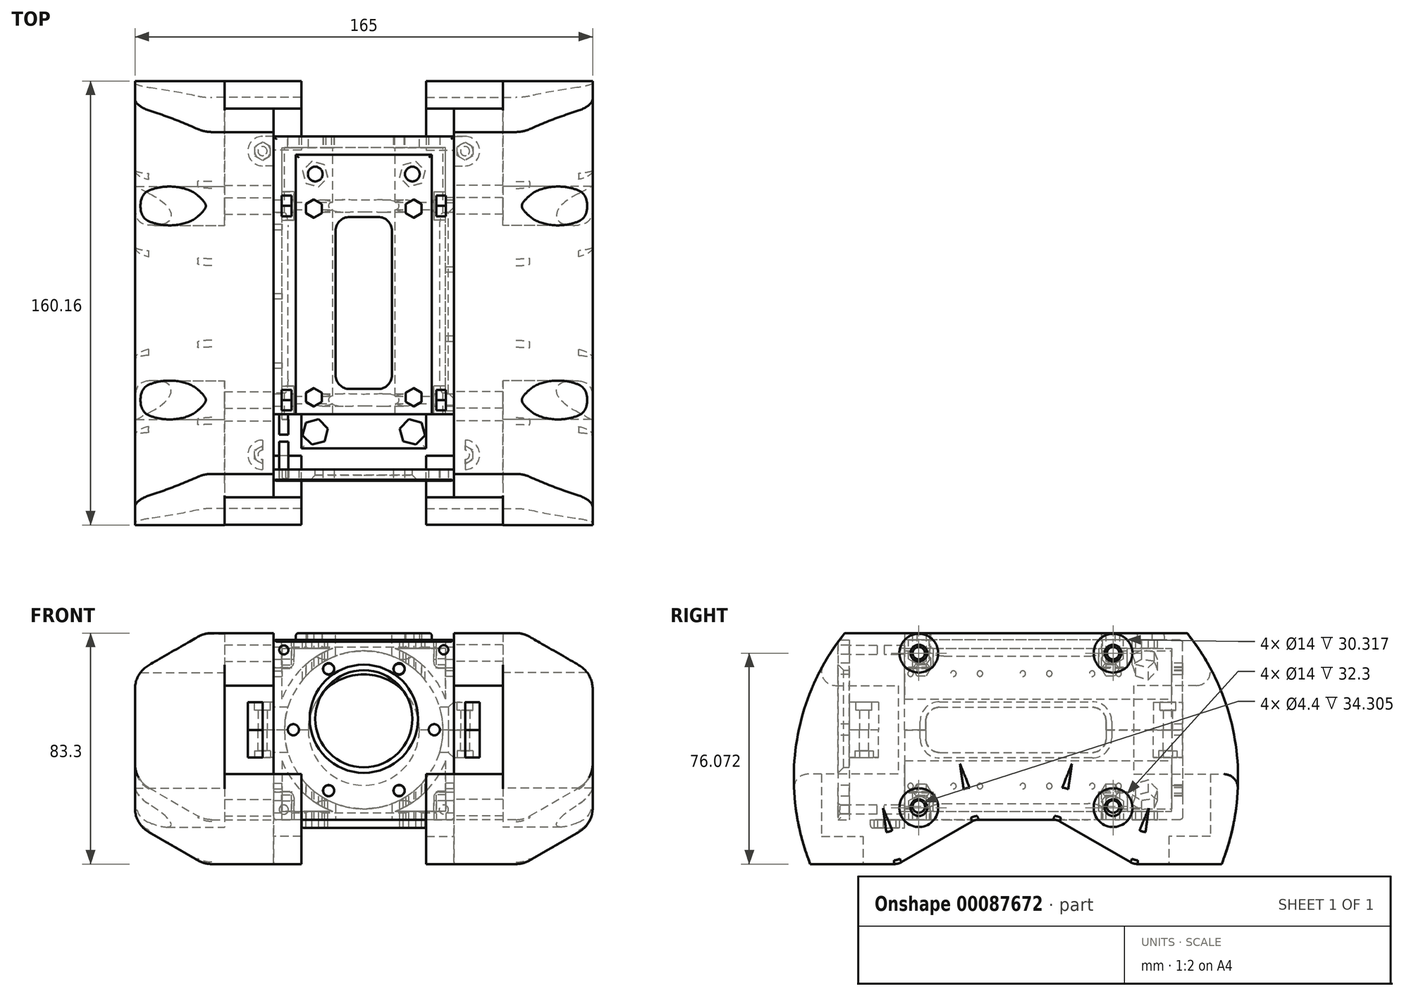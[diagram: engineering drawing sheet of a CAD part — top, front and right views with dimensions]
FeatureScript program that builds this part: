
annotation { "Feature Type Name" : "Feature", "Feature Type Description" : "" }
export const myFeature = defineFeature(function(context is Context, id is Id, definition is map)
    precondition{}
    {
        {
            assignVariable(context, id + "F0", {"name" : "M3_HEX_WIDTH", "anyValue" : 5.5});
        }
        {
            assignVariable(context, id + "F1", {"name" : "M3_HEX_HEIGHT", "anyValue" : 2.4});
        }
        {
            assignVariable(context, id + "F2", {"name" : "MIN_WALL_THICKNESS", "anyValue" : 3});
        }
        {
            assignVariable(context, id + "F3", {"name" : "BACK_LIP_THICKNESS", "anyValue" : 4});
        }
        {
            assignVariable(context, id + "F4", {"name" : "FRONT_PLATE_THICKNESS", "anyValue" : 4});
        }
        {
            assignVariable(context, id + "F5", {"name" : "CASE_WIDTH", "anyValue" : 65});
        }
        {
            assignVariable(context, id + "F6", {"name" : "BASE_TOP_INTERFERENCE", "anyValue" : 0.2});
        }
        {
            assignVariable(context, id + "F7", {"name" : "SIDE_BOSS_HEIGHT", "anyValue" : 20});
        }
        {
            assignVariable(context, id + "F8", {"name" : "M3_SOCKET_HEAD_HEIGHT", "anyValue" : 3});
        }
        {
            var Q0;
            Q0=qCreatedBy(makeId("Top.planeOp"),FACE);
            var sketch = newSketch(context, id + "F9", { "sketchPlane" : qUnion([Q0])});
            skLineSegment(sketch, "E0.bottom", {"start": v(32.5, 60.08) * mm, "end": v(-32.5, 60.08) * mm});
            skLineSegment(sketch, "E0.top", {"start": v(32.5, -60.08) * mm, "end": v(-32.5, -60.08) * mm});
            skLineSegment(sketch, "E0.left", {"start": v(32.5, 60.08) * mm, "end": v(32.5, -60.08) * mm});
            skLineSegment(sketch, "E0.right", {"start": v(-32.5, 60.08) * mm, "end": v(-32.5, -60.08) * mm});
            skPoint(sketch, "E0.middle", {"position": v(0, 0) * mm});
            skSolve(sketch);
        }
        {
            var Q0;
            Q0=makeQuery(id+"F9.imprint","IMPRINT",FACE,{"disambiguationData":[TD([[makeQuery(id+"F9.imprint","IMPRINT",EDGE,{"derivedFrom":sQuery(id+"F9.wireOp",EDGE,"E0.bottom")}),1.0]])]});
            extrude(context, id + "F10", {"entities" : qUnion([Q0]), "depth" : ((getVariable(context, 'CASE_WIDTH') - getVariable(context, 'BASE_TOP_INTERFERENCE')) / 2) * mm});
        }
        {
            var Q0;
            Q0=makeQuery(id+"F10.opExtrude","SWEPT_FACE",FACE,{"disambiguationData":[OSD([sQuery(id+"F9.wireOp",EDGE,"E0.bottom")])]});
            cPlane(context, id + "F11", {"entities" : qUnion([Q0]), "cplaneType" : CPlaneType.OFFSET, "offset" : (getVariable(context, 'BACK_LIP_THICKNESS')) * mm, "oppositeDirection" : true, "width" : 150 * mm, "height" : 150 * mm});
        }
        {
            var Q0;
            Q0=qCreatedBy(id+"F11.planeOp",FACE);
            var sketch = newSketch(context, id + "F12", { "sketchPlane" : qUnion([Q0])});
            skLineSegment(sketch, "E1", {"start": v(0, 32.4) * mm, "end": v(0, 32.5) * mm, "construction": true});
            skCircle(sketch, "E2", {"center": v(0, 32.5) * mm, "radius": 28.57 * mm});
            skLineSegment(sketch, "E3.1", {"start": v(-32.5, 32.4) * mm, "end": v(32.5, 32.4) * mm, "construction": true});
            skSolve(sketch);
        }
        {
            var Q0;
            Q0=makeQuery(id+"F12.imprint","IMPRINT",FACE,{"disambiguationData":[TD([[makeQuery(id+"F12.imprint","IMPRINT",EDGE,{"derivedFrom":sQuery(id+"F12.wireOp",EDGE,"E2")}),1.0]])]});
            extrude(context, id + "F13", {"entities" : qUnion([Q0]), "operationType" : NewBodyOperationType.REMOVE, "endBound" : BoundingType.THROUGH_ALL, "oppositeDirection" : true, "depth" : 25 * mm});
        }
        {
            var Q0;
            Q0=makeQuery(id+"F10.opExtrude","SWEPT_FACE",FACE,{"disambiguationData":[OSD([sQuery(id+"F9.wireOp",EDGE,"E0.bottom")])]});
            var sketch = newSketch(context, id + "F14", { "sketchPlane" : qUnion([Q0])});
            skCircle(sketch, "E4", {"center": v(0, 32.4) * mm, "radius": 20 * mm});
            skSolve(sketch);
        }
        {
            var Q0;
            {var subQ0=sQuery(id+"F14.wireOp",EDGE,"E4");var subQ1=makeQuery(id+"F10.opExtrude","CAP_EDGE",EDGE,{"disambiguationData":[OSD([sQuery(id+"F9.wireOp",EDGE,"E0.bottom")])],"isStart":false});var subQ2=makeQuery(id+"F14.imprint","INTERSECT",VERTEX,{"disambiguationData":[OD(0.0)],"derivedFrom":[subQ1,subQ0]});Q0=makeQuery(id+"F14.imprint","IMPRINT",FACE,{"disambiguationData":[TD([[makeQuery(id+"F14.imprint","IMPRINT",EDGE,{"disambiguationData":[TD([[subQ2,-1.0]])],"derivedFrom":subQ0}),1.0]])]});}
            extrude(context, id + "F15", {"entities" : qUnion([Q0]), "operationType" : NewBodyOperationType.REMOVE, "endBound" : BoundingType.THROUGH_ALL, "oppositeDirection" : true, "depth" : 25 * mm});
        }
        {
            var Q0;
            Q0=makeQuery(id+"F13.boolean.opBoolean","COPY",FACE,{"derivedFrom":makeQuery(id+"F13.opExtrude","CAP_FACE",FACE,{"disambiguationData":[OSD([sQuery(id+"F12.wireOp",EDGE,"E2")])],"isStart":true})});
            var sketch = newSketch(context, id + "F16", { "sketchPlane" : qUnion([Q0])});
            skLineSegment(sketch, "E5", {"start": v(20, 32.4) * mm, "end": v(-20, 32.4) * mm, "construction": true});
            skLineSegment(sketch, "E6", {"start": v(0, 32.4) * mm, "end": v(0, 32.5) * mm});
            skPoint(sketch, "E6.endSnap0", {"position": v(0, 32.4) * mm});
            skCircle(sketch, "E7", {"center": v(0, 32.5) * mm, "radius": 25.4 * mm, "construction": true});
            skCircle(sketch, "E8", {"center": v(-12.66, 10.48) * mm, "radius": 2 * mm});
            skCircle(sketch, "E9.1.0", {"center": v(12.74, 10.53) * mm, "radius": 2 * mm});
            skCircle(sketch, "E9.2.0", {"center": v(25.4, 32.55) * mm, "radius": 2 * mm});
            skCircle(sketch, "E10.1.3.0", {"center": v(12.66, 54.52) * mm, "radius": 2 * mm});
            skCircle(sketch, "E10.1.4.0", {"center": v(-12.74, 54.47) * mm, "radius": 2 * mm});
            skCircle(sketch, "E10.1.5.0", {"center": v(-25.4, 32.45) * mm, "radius": 2 * mm});
            skLineSegment(sketch, "E11", {"start": v(0, 32.4) * mm, "end": v(0, 21) * mm, "construction": true});
            skLineSegment(sketch, "E12", {"start": v(0, 32.4) * mm, "end": v(-12.66, 10.48) * mm, "construction": true});
            skSolve(sketch);
        }
        {
            var Q0;
            Q0 = qSketchRegion(id + "F16", true);
            extrude(context, id + "F17", {"entities" : qUnion([Q0]), "operationType" : NewBodyOperationType.REMOVE, "endBound" : BoundingType.THROUGH_ALL, "oppositeDirection" : true, "depth" : 25 * mm});
        }
        {
            var Q0;
            {var subQ0=sQuery(id+"F9.wireOp",EDGE,"E0.left");var subQ2=sQuery(id+"F9.wireOp",EDGE,"E0.top");var subQ3=sQuery(id+"F9.wireOp",EDGE,"E0.bottom");Q0=makeQuery(id+"F15.boolean.opBoolean","SPLIT",FACE,{"disambiguationData":[TD([makeQuery(id+"F10.opExtrude","SWEPT_FACE",FACE,{"disambiguationData":[OSD([subQ0])]})])],"derivedFrom":makeQuery(id+"F10.opExtrude","CAP_FACE",FACE,{"disambiguationData":[OSD([subQ3,subQ2,subQ0,sQuery(id+"F9.wireOp",EDGE,"E0.right")])],"isStart":false})});}
            var sketch = newSketch(context, id + "F18", { "sketchPlane" : qUnion([Q0])});
            skLineSegment(sketch, "E13.0", {"start": v(-32.5, 60.08) * mm, "end": v(-32.5, -60.08) * mm, "construction": true});
            skLineSegment(sketch, "E14", {"start": v(32.5, -54.77) * mm, "end": v(-32.5, -54.77) * mm, "construction": true});
            skLineSegment(sketch, "E15", {"start": v(32.5, -49.48) * mm, "end": v(32.5, -54.77) * mm});
            skLineSegment(sketch, "E16", {"start": v(32.5, -49.48) * mm, "end": v(36.5, -49.48) * mm});
            skLineSegment(sketch, "E17.MirrorCS", {"start": v(32.5, -60.07) * mm, "end": v(36.5, -60.07) * mm});
            skLineSegment(sketch, "E18.MirrorCS", {"start": v(32.5, -60.08) * mm, "end": v(32.5, -54.77) * mm});
            skArc(sketch, "E19", {"start": v(36.5, -49.48) * mm, "mid": v(41.8, -54.78) * mm, "end": v(36.5, -60.08) * mm});
            skLineSegment(sketch, "E20", {"start": v(0, -60.07) * mm, "end": v(0, 0) * mm, "construction": true});
            skPoint(sketch, "E20.endSnap0", {"position": v(0, 0) * mm});
            skLineSegment(sketch, "E21.MirrorCS", {"start": v(-32.5, -49.48) * mm, "end": v(-36.5, -49.48) * mm});
            skArc(sketch, "E22.MirrorCS", {"start": v(-36.5, -49.48) * mm, "mid": v(-41.8, -54.78) * mm, "end": v(-36.5, -60.08) * mm});
            skLineSegment(sketch, "E23.MirrorCS", {"start": v(-32.5, -49.48) * mm, "end": v(-32.5, -54.77) * mm});
            skLineSegment(sketch, "E24.MirrorCS", {"start": v(-32.5, -60.08) * mm, "end": v(-32.5, -54.77) * mm});
            skLineSegment(sketch, "E25.MirrorCS", {"start": v(-32.5, -60.08) * mm, "end": v(-36.5, -60.08) * mm});
            skLineSegment(sketch, "E26", {"start": v(32.5, -60.07) * mm, "end": v(-32.5, -60.07) * mm, "construction": true});
            skLineSegment(sketch, "E27", {"start": v(0, 0) * mm, "end": v(32.5, 0) * mm, "construction": true});
            skLineSegment(sketch, "E28.MirrorCS", {"start": v(32.5, 49.48) * mm, "end": v(36.5, 49.48) * mm});
            skLineSegment(sketch, "E29.MirrorCS", {"start": v(32.5, 60.07) * mm, "end": v(36.5, 60.07) * mm});
            skArc(sketch, "E30.MirrorCS", {"start": v(36.5, 49.48) * mm, "mid": v(41.8, 54.77) * mm, "end": v(36.5, 60.07) * mm});
            skLineSegment(sketch, "E31.MirrorCS", {"start": v(32.5, 49.47) * mm, "end": v(32.5, 54.77) * mm});
            skLineSegment(sketch, "E32.MirrorCS", {"start": v(32.5, 60.08) * mm, "end": v(32.5, 54.77) * mm});
            skLineSegment(sketch, "E33.MirrorCS", {"start": v(32.5, 60.08) * mm, "end": v(-32.5, 60.07) * mm, "construction": true});
            skLineSegment(sketch, "E34.MirrorCS", {"start": v(32.5, 54.77) * mm, "end": v(-32.5, 54.77) * mm, "construction": true});
            skArc(sketch, "E35.MirrorCS", {"start": v(-36.5, 49.48) * mm, "mid": v(-41.8, 54.77) * mm, "end": v(-36.5, 60.07) * mm});
            skLineSegment(sketch, "E36.MirrorCS", {"start": v(-32.5, 60.07) * mm, "end": v(-36.5, 60.07) * mm});
            skLineSegment(sketch, "E37.MirrorCS", {"start": v(-32.5, 60.08) * mm, "end": v(-32.5, 54.77) * mm});
            skLineSegment(sketch, "E38.MirrorCS", {"start": v(-32.5, -60.08) * mm, "end": v(-32.5, 60.08) * mm, "construction": true});
            skLineSegment(sketch, "E39.MirrorCS", {"start": v(-32.5, 49.47) * mm, "end": v(-32.5, 54.77) * mm});
            skLineSegment(sketch, "E40.MirrorCS", {"start": v(-32.5, 49.48) * mm, "end": v(-36.5, 49.48) * mm});
            skSolve(sketch);
        }
        {
            var Q0;
            Q0 = qSketchRegion(id + "F18", true);
            extrude(context, id + "F19", {"entities" : qUnion([Q0]), "operationType" : NewBodyOperationType.ADD, "oppositeDirection" : true, "depth" : ((getVariable(context, 'SIDE_BOSS_HEIGHT')) / 2) * mm});
        }
        {
            var Q0;
            Q0=sQuery(id+"F18.wireOp",VERTEX,"E22.MirrorCS.center");
            var Q1;
            Q1=sQuery(id+"F18.wireOp",VERTEX,"E19.center");
            var Q2;
            Q2=sQuery(id+"F18.wireOp",VERTEX,"E35.MirrorCS.center");
            var Q3;
            Q3=sQuery(id+"F18.wireOp",VERTEX,"E30.MirrorCS.center");
            var Q4;
            Q4=makeQuery(id+"F10.opExtrude","SWEPT_BODY",BODY,{"disambiguationData":[OSD([sQuery(id+"F9.wireOp",EDGE,"E0.bottom"),sQuery(id+"F9.wireOp",EDGE,"E0.top"),sQuery(id+"F9.wireOp",EDGE,"E0.left"),sQuery(id+"F9.wireOp",EDGE,"E0.right")])]});
            hole(context, id + "F20", {"style" : HoleStyle.SIMPLE, "endStyle" : HoleEndStyle.THROUGH, "standardTappedOrClearance" : lookupTablePath({ "standard" : "ISO", "fit" : "Normal", "size" : "M3", "type" : "Clearance" }), "standardBlindInLast" : lookupTablePath({ "fit" : "Standard", "standard" : "ISO", "size" : "M3", "type" : "Clearance" }), "holeDiameter" : 3.3 * mm, "locations" : qUnion([Q0, Q1, Q2, Q3]), "scope" : qUnion([Q4]), "isTappedThrough" : true});
        }
        {
            var Q0;
            Q0=makeQuery(id+"F13.boolean.opBoolean","COPY",FACE,{"derivedFrom":makeQuery(id+"F13.opExtrude","CAP_FACE",FACE,{"disambiguationData":[OSD([sQuery(id+"F12.wireOp",EDGE,"E2")])],"isStart":true})});
            var sketch = newSketch(context, id + "F21", { "sketchPlane" : qUnion([Q0])});
            skLineSegment(sketch, "E41", {"start": v(0, 0) * mm, "end": v(0, 32.5) * mm, "construction": true});
            skLineSegment(sketch, "E42", {"start": v(29.5, 21.24) * mm, "end": v(29.5, 3) * mm});
            skLineSegment(sketch, "E43", {"start": v(29.5, 3) * mm, "end": v(11.26, 3) * mm});
            skArc(sketch, "E44", {"start": v(11.26, 3) * mm, "mid": v(22.33, 10.17) * mm, "end": v(29.5, 21.24) * mm});
            skArc(sketch, "E45.MirrorCS", {"start": v(-11.26, 3) * mm, "mid": v(-22.33, 10.17) * mm, "end": v(-29.5, 21.24) * mm});
            skLineSegment(sketch, "E46.MirrorCS", {"start": v(-29.5, 3) * mm, "end": v(-11.26, 3) * mm});
            skLineSegment(sketch, "E47.MirrorCS", {"start": v(-29.5, 21.24) * mm, "end": v(-29.5, 3) * mm});
            skSolve(sketch);
        }
        {
            var Q0;
            Q0 = qSketchRegion(id + "F21", true);
            extrude(context, id + "F22", {"entities" : qUnion([Q0]), "operationType" : NewBodyOperationType.REMOVE, "endBound" : BoundingType.THROUGH_ALL, "depth" : 25 * mm});
        }
        {
            var Q0;
            Q0=makeQuery(id+"F22.boolean.opBoolean","COPY",FACE,{"derivedFrom":makeQuery(id+"F22.opExtrude","SWEPT_FACE",FACE,{"disambiguationData":[OSD([sQuery(id+"F21.wireOp",EDGE,"E47.MirrorCS")])]})});
            var sketch = newSketch(context, id + "F23", { "sketchPlane" : qUnion([Q0])});
            skLineSegment(sketch, "E48", {"start": v(-60.08, 12.12) * mm, "end": v(56.08, 12.12) * mm, "construction": true});
            skCircle(sketch, "E49", {"center": v(-47.52, 12.12) * mm, "radius": 1 * mm});
            skCircle(sketch, "E50.1.0.0", {"center": v(-22.52, 12.12) * mm, "radius": 1 * mm});
            skCircle(sketch, "E50.2.0.0", {"center": v(2.48, 12.12) * mm, "radius": 1 * mm});
            skCircle(sketch, "E50.3.0.0", {"center": v(27.48, 12.12) * mm, "radius": 1 * mm});
            skLineSegment(sketch, "E50.direction1", {"start": v(-47.52, 12.12) * mm, "end": v(-22.52, 12.12) * mm, "construction": true});
            skSolve(sketch);
        }
        {
            var Q0;
            Q0=makeQuery(id+"F22.boolean.opBoolean","COPY",FACE,{"derivedFrom":makeQuery(id+"F22.opExtrude","SWEPT_FACE",FACE,{"disambiguationData":[OSD([sQuery(id+"F21.wireOp",EDGE,"E42")])]})});
            var sketch = newSketch(context, id + "F24", { "sketchPlane" : qUnion([Q0])});
            skLineSegment(sketch, "E51", {"start": v(60.08, 12.12) * mm, "end": v(-56.08, 12.12) * mm, "construction": true});
            skCircle(sketch, "E52", {"center": v(37.97, 12.12) * mm, "radius": 1 * mm});
            skCircle(sketch, "E53.1.0.0", {"center": v(12.97, 12.12) * mm, "radius": 1 * mm});
            skCircle(sketch, "E53.2.0.0", {"center": v(-12.03, 12.12) * mm, "radius": 1 * mm});
            skCircle(sketch, "E53.3.0.0", {"center": v(-37.03, 12.12) * mm, "radius": 1 * mm});
            skLineSegment(sketch, "E53.direction1", {"start": v(37.97, 12.12) * mm, "end": v(12.97, 12.12) * mm, "construction": true});
            skSolve(sketch);
        }
        {
            var Q0;
            Q0 = qSketchRegion(id + "F23", true);
            extrude(context, id + "F25", {"entities" : qUnion([Q0]), "operationType" : NewBodyOperationType.REMOVE, "endBound" : BoundingType.THROUGH_ALL, "oppositeDirection" : true, "depth" : 25 * mm});
        }
        {
            var Q0;
            Q0 = qSketchRegion(id + "F24", true);
            extrude(context, id + "F26", {"entities" : qUnion([Q0]), "operationType" : NewBodyOperationType.REMOVE, "endBound" : BoundingType.THROUGH_ALL, "oppositeDirection" : true, "depth" : 25 * mm});
        }
        {
            var Q0;
            Q0=makeQuery(id+"F10.opExtrude","SWEPT_FACE",FACE,{"disambiguationData":[OSD([sQuery(id+"F9.wireOp",EDGE,"E0.top")])]});
            var sketch = newSketch(context, id + "F27", { "sketchPlane" : qUnion([Q0])});
            skLineSegment(sketch, "E54.bottom", {"start": v(32.5, 0) * mm, "end": v(25.2, 0) * mm});
            skLineSegment(sketch, "E54.top", {"start": v(32.5, 7.3) * mm, "end": v(25.2, 7.3) * mm});
            skLineSegment(sketch, "E54.left", {"start": v(32.5, 0) * mm, "end": v(32.5, 7.3) * mm});
            skLineSegment(sketch, "E54.right", {"start": v(25.2, 0) * mm, "end": v(25.2, 7.3) * mm});
            skLineSegment(sketch, "E55", {"start": v(0, 0) * mm, "end": v(0, 33.35) * mm, "construction": true});
            skLineSegment(sketch, "E56.MirrorCS", {"start": v(-25.2, 0) * mm, "end": v(-25.2, 7.3) * mm});
            skLineSegment(sketch, "E57.MirrorCS", {"start": v(-32.5, 0) * mm, "end": v(-25.2, 0) * mm});
            skLineSegment(sketch, "E58.MirrorCS", {"start": v(-32.5, 0) * mm, "end": v(-32.5, 7.3) * mm});
            skLineSegment(sketch, "E59.MirrorCS", {"start": v(-32.5, 7.3) * mm, "end": v(-25.2, 7.3) * mm});
            skSolve(sketch);
        }
        {
            var Q0;
            Q0 = qSketchRegion(id + "F27", true);
            extrude(context, id + "F28", {"entities" : qUnion([Q0]), "operationType" : NewBodyOperationType.ADD, "oppositeDirection" : true, "depth" : 18 * mm});
        }
        {
            var Q0;
            Q0=makeQuery(id+"F28.boolean.opBoolean","MERGE",FACE,{"derivedFrom":[makeQuery(id+"F10.opExtrude","SWEPT_FACE",FACE,{"disambiguationData":[OSD([sQuery(id+"F9.wireOp",EDGE,"E0.top")])]}),makeQuery(id+"F28.opExtrude","CAP_FACE",FACE,{"disambiguationData":[OSD([sQuery(id+"F27.wireOp",EDGE,"E54.bottom"),sQuery(id+"F27.wireOp",EDGE,"E54.top"),sQuery(id+"F27.wireOp",EDGE,"E54.left"),sQuery(id+"F27.wireOp",EDGE,"E54.right")])],"isStart":true}),makeQuery(id+"F28.opExtrude","CAP_FACE",FACE,{"disambiguationData":[OSD([sQuery(id+"F27.wireOp",EDGE,"E57.MirrorCS"),sQuery(id+"F27.wireOp",EDGE,"E58.MirrorCS"),sQuery(id+"F27.wireOp",EDGE,"E59.MirrorCS"),sQuery(id+"F27.wireOp",EDGE,"E56.MirrorCS")])],"isStart":true})]});
            var sketch = newSketch(context, id + "F29", { "sketchPlane" : qUnion([Q0])});
            skLineSegment(sketch, "E60", {"start": v(32.5, 0) * mm, "end": v(25.2, 7.3) * mm, "construction": true});
            skCircle(sketch, "E61", {"center": v(28.85, 3.65) * mm, "radius": 1.65 * mm});
            skLineSegment(sketch, "E62", {"start": v(0, 0) * mm, "end": v(0, 32.4) * mm, "construction": true});
            skCircle(sketch, "E63.MirrorC", {"center": v(-28.85, 3.65) * mm, "radius": 1.65 * mm});
            skSolve(sketch);
        }
        {
            var Q0;
            Q0=makeQuery(id+"F29.imprint","IMPRINT",FACE,{"disambiguationData":[TD([[makeQuery(id+"F29.imprint","IMPRINT",EDGE,{"derivedFrom":sQuery(id+"F29.wireOp",EDGE,"E63.MirrorC")}),-1.0]])]});
            var Q1;
            Q1=makeQuery(id+"F29.imprint","IMPRINT",FACE,{"disambiguationData":[TD([[makeQuery(id+"F29.imprint","IMPRINT",EDGE,{"derivedFrom":sQuery(id+"F29.wireOp",EDGE,"E61")}),1.0]])]});
            extrude(context, id + "F30", {"entities" : qUnion([Q0, Q1]), "operationType" : NewBodyOperationType.REMOVE, "oppositeDirection" : true, "depth" : 20 * mm});
        }
        {
            var Q0;
            Q0=makeQuery(id+"F28.boolean.opBoolean","MERGE",FACE,{"derivedFrom":[makeQuery(id+"F10.opExtrude","SWEPT_FACE",FACE,{"disambiguationData":[OSD([sQuery(id+"F9.wireOp",EDGE,"E0.top")])]}),makeQuery(id+"F28.opExtrude","CAP_FACE",FACE,{"disambiguationData":[OSD([sQuery(id+"F27.wireOp",EDGE,"E54.bottom"),sQuery(id+"F27.wireOp",EDGE,"E54.top"),sQuery(id+"F27.wireOp",EDGE,"E54.left"),sQuery(id+"F27.wireOp",EDGE,"E54.right")])],"isStart":true}),makeQuery(id+"F28.opExtrude","CAP_FACE",FACE,{"disambiguationData":[OSD([sQuery(id+"F27.wireOp",EDGE,"E57.MirrorCS"),sQuery(id+"F27.wireOp",EDGE,"E58.MirrorCS"),sQuery(id+"F27.wireOp",EDGE,"E59.MirrorCS"),sQuery(id+"F27.wireOp",EDGE,"E56.MirrorCS")])],"isStart":true})]});
            cPlane(context, id + "F31", {"entities" : qUnion([Q0]), "cplaneType" : CPlaneType.OFFSET, "offset" : 10 * mm, "oppositeDirection" : true, "width" : 150 * mm, "height" : 150 * mm});
        }
        {
            var Q0;
            Q0=qCreatedBy(id+"F31.planeOp",FACE);
            var sketch = newSketch(context, id + "F32", { "sketchPlane" : qUnion([Q0])});
            skCircle(sketch, "E64.0", {"center": v(28.85, 3.65) * mm, "radius": 1.65 * mm, "construction": true});
            skCircle(sketch, "E65.cCircle", {"center": v(28.85, 3.65) * mm, "radius": 2.85 * mm, "construction": true});
            skLineSegment(sketch, "E65.0", {"start": v(28.85, 6.94) * mm, "end": v(31.7, 5.3) * mm});
            skLineSegment(sketch, "E65.1", {"start": v(31.7, 5.3) * mm, "end": v(31.7, 2) * mm});
            skLineSegment(sketch, "E65.2", {"start": v(31.7, 2) * mm, "end": v(28.85, 0.36) * mm});
            skLineSegment(sketch, "E65.3", {"start": v(28.85, 0.36) * mm, "end": v(26, 2) * mm});
            skLineSegment(sketch, "E65.4", {"start": v(26, 2) * mm, "end": v(26, 5.3) * mm});
            skLineSegment(sketch, "E65.5", {"start": v(26, 5.3) * mm, "end": v(28.85, 6.94) * mm});
            skPoint(sketch, "E65.0.midPoint", {"position": v(30.28, 6.12) * mm});
            skLineSegment(sketch, "E66", {"start": v(0, 0) * mm, "end": v(0, 24.89) * mm, "construction": true});
            skLineSegment(sketch, "E67.MirrorCS", {"start": v(-26, 5.3) * mm, "end": v(-28.85, 6.94) * mm});
            skLineSegment(sketch, "E68.MirrorCS", {"start": v(-26, 2) * mm, "end": v(-26, 5.3) * mm});
            skLineSegment(sketch, "E69.MirrorCS", {"start": v(-28.85, 0.36) * mm, "end": v(-26, 2) * mm});
            skLineSegment(sketch, "E70.MirrorCS", {"start": v(-31.7, 2) * mm, "end": v(-28.85, 0.36) * mm});
            skLineSegment(sketch, "E71.MirrorCS", {"start": v(-31.7, 5.3) * mm, "end": v(-31.7, 2) * mm});
            skLineSegment(sketch, "E72.MirrorCS", {"start": v(-28.85, 6.94) * mm, "end": v(-31.7, 5.3) * mm});
            skCircle(sketch, "E73.MirrorC", {"center": v(-28.85, 3.65) * mm, "radius": 2.85 * mm, "construction": true});
            skCircle(sketch, "E74.MirrorC", {"center": v(-28.85, 3.65) * mm, "radius": 1.65 * mm, "construction": true});
            skPoint(sketch, "E75.MirrorP", {"position": v(-30.28, 6.12) * mm});
            skSolve(sketch);
        }
        {
            var Q0;
            Q0 = qSketchRegion(id + "F32", true);
            extrude(context, id + "F33", {"entities" : qUnion([Q0]), "operationType" : NewBodyOperationType.REMOVE, "oppositeDirection" : true, "depth" : (getVariable(context, 'M3_HEX_HEIGHT') + 0.2) * mm});
        }
        {
            var Q0;
            Q0=makeQuery(id+"F10.opExtrude","CAP_FACE",FACE,{"disambiguationData":[OSD([sQuery(id+"F9.wireOp",EDGE,"E0.bottom"),sQuery(id+"F9.wireOp",EDGE,"E0.top"),sQuery(id+"F9.wireOp",EDGE,"E0.left"),sQuery(id+"F9.wireOp",EDGE,"E0.right")])],"isStart":true});
            var sketch = newSketch(context, id + "F34", { "sketchPlane" : qUnion([Q0])});
            skLineSegment(sketch, "E76.0", {"start": v(31.7, 47.48) * mm, "end": v(31.7, 50.08) * mm});
            skLineSegment(sketch, "E76.1", {"start": v(26, 47.48) * mm, "end": v(26, 50.08) * mm});
            skLineSegment(sketch, "E77", {"start": v(31.7, 50.08) * mm, "end": v(26, 50.08) * mm});
            skLineSegment(sketch, "E78", {"start": v(31.7, 47.48) * mm, "end": v(26, 47.48) * mm});
            skLineSegment(sketch, "E79", {"start": v(0, 0) * mm, "end": v(0, 60.08) * mm, "construction": true});
            skLineSegment(sketch, "E80.MirrorCS", {"start": v(-31.7, 47.47) * mm, "end": v(-31.7, 50.07) * mm});
            skLineSegment(sketch, "E81.MirrorCS", {"start": v(-31.7, 47.47) * mm, "end": v(-26, 47.47) * mm});
            skLineSegment(sketch, "E82.MirrorCS", {"start": v(-31.7, 50.07) * mm, "end": v(-26, 50.07) * mm});
            skLineSegment(sketch, "E83.MirrorCS", {"start": v(-26, 47.47) * mm, "end": v(-26, 50.07) * mm});
            skSolve(sketch);
        }
        {
            var Q0;
            Q0 = qSketchRegion(id + "F34", true);
            extrude(context, id + "F35", {"entities" : qUnion([Q0]), "operationType" : NewBodyOperationType.REMOVE, "oppositeDirection" : true, "depth" : (getVariable(context, 'M3_HEX_WIDTH')) * mm});
        }
        {
            var Q0;
            Q0=makeQuery(id+"F10.opExtrude","CAP_FACE",FACE,{"disambiguationData":[OSD([sQuery(id+"F9.wireOp",EDGE,"E0.bottom"),sQuery(id+"F9.wireOp",EDGE,"E0.top"),sQuery(id+"F9.wireOp",EDGE,"E0.left"),sQuery(id+"F9.wireOp",EDGE,"E0.right")])],"isStart":true});
            var sketch = newSketch(context, id + "F36", { "sketchPlane" : qUnion([Q0])});
            skLineSegment(sketch, "E84.bottom", {"start": v(27.85, 35) * mm, "end": v(-27.85, 35) * mm, "construction": true});
            skLineSegment(sketch, "E84.top", {"start": v(27.85, -35) * mm, "end": v(-27.85, -35) * mm, "construction": true});
            skLineSegment(sketch, "E84.left", {"start": v(27.85, 35) * mm, "end": v(27.85, -35) * mm, "construction": true});
            skLineSegment(sketch, "E84.right", {"start": v(-27.85, 35) * mm, "end": v(-27.85, -35) * mm, "construction": true});
            skPoint(sketch, "E84.middle", {"position": v(0, 0) * mm});
            skLineSegment(sketch, "E85.bottom", {"start": v(32.5, 40.1) * mm, "end": v(23.2, 40.1) * mm, "construction": true});
            skLineSegment(sketch, "E85.top", {"start": v(32.5, 29.9) * mm, "end": v(23.2, 29.9) * mm, "construction": true});
            skLineSegment(sketch, "E85.left", {"start": v(32.5, 40.1) * mm, "end": v(32.5, 29.9) * mm});
            skLineSegment(sketch, "E85.right", {"start": v(23.2, 40.1) * mm, "end": v(23.2, 29.9) * mm, "construction": true});
            skPoint(sketch, "E85.middle", {"position": v(27.85, 35) * mm});
            skLineSegment(sketch, "E86", {"start": v(25.2, 40.1) * mm, "end": v(25.2, 29.9) * mm});
            skLineSegment(sketch, "E87", {"start": v(25.2, 40.1) * mm, "end": v(32.5, 40.1) * mm});
            skLineSegment(sketch, "E88", {"start": v(32.5, 29.9) * mm, "end": v(25.2, 29.9) * mm});
            skLineSegment(sketch, "E89", {"start": v(0, 0) * mm, "end": v(0, 35) * mm, "construction": true});
            skLineSegment(sketch, "E90", {"start": v(0, 0) * mm, "end": v(27.85, 0) * mm, "construction": true});
            skLineSegment(sketch, "E91.MirrorCS", {"start": v(-32.5, 40.1) * mm, "end": v(-23.2, 40.1) * mm, "construction": true});
            skLineSegment(sketch, "E92.MirrorCS", {"start": v(-32.5, 29.9) * mm, "end": v(-23.2, 29.9) * mm, "construction": true});
            skLineSegment(sketch, "E93.MirrorCS", {"start": v(-23.2, 40.1) * mm, "end": v(-23.2, 29.9) * mm, "construction": true});
            skLineSegment(sketch, "E94.MirrorCS", {"start": v(-25.2, 40.1) * mm, "end": v(-32.5, 40.1) * mm});
            skLineSegment(sketch, "E95.MirrorCS", {"start": v(-32.5, 29.9) * mm, "end": v(-25.2, 29.9) * mm});
            skPoint(sketch, "E96.MirrorP", {"position": v(-27.85, 35) * mm});
            skLineSegment(sketch, "E97.MirrorCS", {"start": v(-32.5, 40.1) * mm, "end": v(-32.5, 29.9) * mm});
            skLineSegment(sketch, "E98.MirrorCS", {"start": v(-25.2, 40.1) * mm, "end": v(-25.2, 29.9) * mm});
            skLineSegment(sketch, "E99.MirrorCS", {"start": v(-32.5, -29.9) * mm, "end": v(-23.2, -29.9) * mm, "construction": true});
            skLineSegment(sketch, "E100.MirrorCS", {"start": v(-32.5, -40.1) * mm, "end": v(-23.2, -40.1) * mm, "construction": true});
            skLineSegment(sketch, "E101.MirrorCS", {"start": v(-23.2, -40.1) * mm, "end": v(-23.2, -29.9) * mm, "construction": true});
            skLineSegment(sketch, "E102.MirrorCS", {"start": v(-32.5, -40.1) * mm, "end": v(-32.5, -29.9) * mm});
            skLineSegment(sketch, "E103.MirrorCS", {"start": v(-25.2, -40.1) * mm, "end": v(-32.5, -40.1) * mm});
            skLineSegment(sketch, "E104.MirrorCS", {"start": v(-32.5, -29.9) * mm, "end": v(-25.2, -29.9) * mm});
            skPoint(sketch, "E105.MirrorP", {"position": v(-27.85, -35) * mm});
            skLineSegment(sketch, "E106.MirrorCS", {"start": v(-25.2, -40.1) * mm, "end": v(-25.2, -29.9) * mm});
            skLineSegment(sketch, "E107.MirrorCS", {"start": v(32.5, -40.1) * mm, "end": v(23.2, -40.1) * mm, "construction": true});
            skLineSegment(sketch, "E108.MirrorCS", {"start": v(32.5, -29.9) * mm, "end": v(23.2, -29.9) * mm, "construction": true});
            skLineSegment(sketch, "E109.MirrorCS", {"start": v(32.5, -29.9) * mm, "end": v(25.2, -29.9) * mm});
            skLineSegment(sketch, "E110.MirrorCS", {"start": v(25.2, -40.1) * mm, "end": v(32.5, -40.1) * mm});
            skLineSegment(sketch, "E111.MirrorCS", {"start": v(32.5, -40.1) * mm, "end": v(32.5, -29.9) * mm});
            skLineSegment(sketch, "E112.MirrorCS", {"start": v(23.2, -40.1) * mm, "end": v(23.2, -29.9) * mm, "construction": true});
            skLineSegment(sketch, "E113.MirrorCS", {"start": v(25.2, -40.1) * mm, "end": v(25.2, -29.9) * mm});
            skPoint(sketch, "E114.MirrorP", {"position": v(27.85, -35) * mm});
            skLineSegment(sketch, "E115.bottom", {"start": v(29.6, 38.7) * mm, "end": v(26.1, 38.7) * mm});
            skLineSegment(sketch, "E115.top", {"start": v(29.6, 31.3) * mm, "end": v(26.1, 31.3) * mm});
            skLineSegment(sketch, "E115.left", {"start": v(29.6, 38.7) * mm, "end": v(29.6, 31.3) * mm});
            skLineSegment(sketch, "E115.right", {"start": v(26.1, 38.7) * mm, "end": v(26.1, 31.3) * mm});
            skLineSegment(sketch, "E116.MirrorCS", {"start": v(-29.6, 31.3) * mm, "end": v(-26.1, 31.3) * mm});
            skLineSegment(sketch, "E117.MirrorCS", {"start": v(-29.6, 38.7) * mm, "end": v(-26.1, 38.7) * mm});
            skLineSegment(sketch, "E118.MirrorCS", {"start": v(-29.6, 38.7) * mm, "end": v(-29.6, 31.3) * mm});
            skLineSegment(sketch, "E119.MirrorCS", {"start": v(-26.1, 38.7) * mm, "end": v(-26.1, 31.3) * mm});
            skLineSegment(sketch, "E120.MirrorCS", {"start": v(-27.85, 35) * mm, "end": v(27.85, 35) * mm, "construction": true});
            skLineSegment(sketch, "E121.MirrorCS", {"start": v(-26.1, -38.7) * mm, "end": v(-26.1, -31.3) * mm});
            skLineSegment(sketch, "E122.MirrorCS", {"start": v(-29.6, -31.3) * mm, "end": v(-26.1, -31.3) * mm});
            skLineSegment(sketch, "E123.MirrorCS", {"start": v(-29.6, -38.7) * mm, "end": v(-29.6, -31.3) * mm});
            skLineSegment(sketch, "E124.MirrorCS", {"start": v(-29.6, -38.7) * mm, "end": v(-26.1, -38.7) * mm});
            skLineSegment(sketch, "E125.MirrorCS", {"start": v(29.6, -31.3) * mm, "end": v(26.1, -31.3) * mm});
            skLineSegment(sketch, "E126.MirrorCS", {"start": v(26.1, -38.7) * mm, "end": v(26.1, -31.3) * mm});
            skLineSegment(sketch, "E127.MirrorCS", {"start": v(29.6, -38.7) * mm, "end": v(26.1, -38.7) * mm});
            skLineSegment(sketch, "E128.MirrorCS", {"start": v(29.6, -38.7) * mm, "end": v(29.6, -31.3) * mm});
            skSolve(sketch);
        }
        {
            var Q0;
            Q0 = qSketchRegion(id + "F36", true);
            var Q1;
            Q1=makeQuery(id+"F36.imprint","IMPRINT",FACE,{"disambiguationData":[TD([[makeQuery(id+"F36.imprint","IMPRINT",EDGE,{"derivedFrom":sQuery(id+"F36.wireOp",EDGE,"E116.MirrorCS")}),1.0]])]});
            var Q2;
            Q2=makeQuery(id+"F36.imprint","IMPRINT",FACE,{"disambiguationData":[TD([[makeQuery(id+"F36.imprint","IMPRINT",EDGE,{"derivedFrom":sQuery(id+"F36.wireOp",EDGE,"E115.bottom")}),1.0]])]});
            var Q3;
            Q3=makeQuery(id+"F36.imprint","IMPRINT",FACE,{"disambiguationData":[TD([[makeQuery(id+"F36.imprint","IMPRINT",EDGE,{"derivedFrom":sQuery(id+"F36.wireOp",EDGE,"E125.MirrorCS")}),1.0]])]});
            var Q4;
            Q4=makeQuery(id+"F36.imprint","IMPRINT",FACE,{"disambiguationData":[TD([[makeQuery(id+"F36.imprint","IMPRINT",EDGE,{"derivedFrom":sQuery(id+"F36.wireOp",EDGE,"E121.MirrorCS")}),1.0]])]});
            extrude(context, id + "F37", {"entities" : qUnion([Q0, Q1, Q2, Q3, Q4]), "operationType" : NewBodyOperationType.ADD, "oppositeDirection" : true, "depth" : 10 * mm});
        }
        {
            var Q0;
            Q0=makeQuery(id+"F36.imprint","IMPRINT",FACE,{"disambiguationData":[TD([[makeQuery(id+"F36.imprint","IMPRINT",EDGE,{"derivedFrom":sQuery(id+"F36.wireOp",EDGE,"E115.bottom")}),1.0]])]});
            var Q1;
            Q1=makeQuery(id+"F36.imprint","IMPRINT",FACE,{"disambiguationData":[TD([[makeQuery(id+"F36.imprint","IMPRINT",EDGE,{"derivedFrom":sQuery(id+"F36.wireOp",EDGE,"E125.MirrorCS")}),1.0]])]});
            var Q2;
            Q2=makeQuery(id+"F36.imprint","IMPRINT",FACE,{"disambiguationData":[TD([[makeQuery(id+"F36.imprint","IMPRINT",EDGE,{"derivedFrom":sQuery(id+"F36.wireOp",EDGE,"E121.MirrorCS")}),1.0]])]});
            var Q3;
            Q3=makeQuery(id+"F36.imprint","IMPRINT",FACE,{"disambiguationData":[TD([[makeQuery(id+"F36.imprint","IMPRINT",EDGE,{"derivedFrom":sQuery(id+"F36.wireOp",EDGE,"E116.MirrorCS")}),1.0]])]});
            var Q4;
            Q4=makeQuery(id+"F37.opExtrude","CAP_FACE",FACE,{"disambiguationData":[OSD([sQuery(id+"F36.wireOp",EDGE,"E94.MirrorCS"),sQuery(id+"F36.wireOp",EDGE,"E95.MirrorCS"),sQuery(id+"F36.wireOp",EDGE,"E97.MirrorCS"),sQuery(id+"F36.wireOp",EDGE,"E98.MirrorCS")])],"isStart":false});
            extrude(context, id + "F38", {"entities" : qUnion([Q0, Q1, Q2, Q3]), "operationType" : NewBodyOperationType.REMOVE, "endBound" : BoundingType.UP_TO_SURFACE, "oppositeDirection" : true, "endBoundEntityFace" : qUnion([Q4]), "depth" : 25 * mm});
        }
        {
            var Q0;
            Q0=makeQuery(id+"F38.boolean.opBoolean","COPY",FACE,{"derivedFrom":makeQuery(id+"F38.opExtrude","SWEPT_FACE",FACE,{"disambiguationData":[OSD([sQuery(id+"F36.wireOp",EDGE,"E119.MirrorCS")])]})});
            var sketch = newSketch(context, id + "F39", { "sketchPlane" : qUnion([Q0])});
            skLineSegment(sketch, "E129", {"start": v(35, 10) * mm, "end": v(35, 0) * mm, "construction": true});
            skLineSegment(sketch, "E130", {"start": v(0, 0) * mm, "end": v(0, 32.2) * mm, "construction": true});
            skCircle(sketch, "E131.cCircle", {"center": v(35, 4.73) * mm, "radius": 3.7 * mm, "construction": true});
            skLineSegment(sketch, "E131.0", {"start": v(35, 9) * mm, "end": v(38.7, 6.86) * mm});
            skLineSegment(sketch, "E131.1", {"start": v(38.7, 6.86) * mm, "end": v(38.7, 2.6) * mm, "construction": true});
            skLineSegment(sketch, "E131.2", {"start": v(38.7, 2.6) * mm, "end": v(35, 0.46) * mm, "construction": true});
            skLineSegment(sketch, "E131.3", {"start": v(35, 0.46) * mm, "end": v(31.3, 2.6) * mm, "construction": true});
            skLineSegment(sketch, "E131.4", {"start": v(31.3, 2.6) * mm, "end": v(31.3, 6.86) * mm, "construction": true});
            skLineSegment(sketch, "E131.5", {"start": v(31.3, 6.86) * mm, "end": v(35, 9) * mm});
            skPoint(sketch, "E131.0.midPoint", {"position": v(36.85, 7.93) * mm});
            skLineSegment(sketch, "E132", {"start": v(38.7, 6.86) * mm, "end": v(38.7, 10.2) * mm});
            skLineSegment(sketch, "E133", {"start": v(38.7, 10.2) * mm, "end": v(31.3, 10.2) * mm});
            skLineSegment(sketch, "E134", {"start": v(31.3, 10.2) * mm, "end": v(31.3, 6.86) * mm});
            skLineSegment(sketch, "E135.MirrorCS", {"start": v(-31.3, 10.2) * mm, "end": v(-31.3, 6.86) * mm});
            skLineSegment(sketch, "E136.MirrorCS", {"start": v(-31.3, 6.86) * mm, "end": v(-35, 9) * mm});
            skLineSegment(sketch, "E137.MirrorCS", {"start": v(-35, 9) * mm, "end": v(-38.7, 6.86) * mm});
            skLineSegment(sketch, "E138.MirrorCS", {"start": v(-38.7, 6.86) * mm, "end": v(-38.7, 10.2) * mm});
            skLineSegment(sketch, "E139.MirrorCS", {"start": v(-38.7, 10.2) * mm, "end": v(-31.3, 10.2) * mm});
            skPoint(sketch, "E140.MirrorP", {"position": v(-35, 4.73) * mm});
            skSolve(sketch);
        }
        {
            var Q0;
            Q0 = qSketchRegion(id + "F39", true);
            var Q1;
            Q1=makeQuery(id+"F38.boolean.opBoolean","COPY",FACE,{"derivedFrom":makeQuery(id+"F38.opExtrude","SWEPT_FACE",FACE,{"disambiguationData":[OSD([sQuery(id+"F36.wireOp",EDGE,"E123.MirrorCS")])]})});
            extrude(context, id + "F40", {"entities" : qUnion([Q0]), "operationType" : NewBodyOperationType.ADD, "endBound" : BoundingType.UP_TO_SURFACE, "endBoundEntityFace" : qUnion([Q1]), "depth" : 25 * mm});
        }
        {
            var Q0;
            Q0=makeQuery(id+"F38.boolean.opBoolean","COPY",FACE,{"derivedFrom":makeQuery(id+"F38.opExtrude","SWEPT_FACE",FACE,{"disambiguationData":[OSD([sQuery(id+"F36.wireOp",EDGE,"E115.right")])]})});
            var sketch = newSketch(context, id + "F41", { "sketchPlane" : qUnion([Q0])});
            skLineSegment(sketch, "E141", {"start": v(-35, 10) * mm, "end": v(-35, 0) * mm, "construction": true});
            skLineSegment(sketch, "E142", {"start": v(0, 0) * mm, "end": v(0, 63.23) * mm, "construction": true});
            skCircle(sketch, "E143.cCircle", {"center": v(-35, 4.73) * mm, "radius": 3.7 * mm, "construction": true});
            skLineSegment(sketch, "E143.0", {"start": v(-35, 9) * mm, "end": v(-31.3, 6.86) * mm});
            skLineSegment(sketch, "E143.1", {"start": v(-31.3, 6.86) * mm, "end": v(-31.3, 2.6) * mm, "construction": true});
            skLineSegment(sketch, "E143.2", {"start": v(-31.3, 2.6) * mm, "end": v(-35, 0.46) * mm, "construction": true});
            skLineSegment(sketch, "E143.3", {"start": v(-35, 0.46) * mm, "end": v(-38.7, 2.6) * mm, "construction": true});
            skLineSegment(sketch, "E143.4", {"start": v(-38.7, 2.6) * mm, "end": v(-38.7, 6.86) * mm, "construction": true});
            skLineSegment(sketch, "E143.5", {"start": v(-38.7, 6.86) * mm, "end": v(-35, 9) * mm});
            skPoint(sketch, "E143.0.midPoint", {"position": v(-33.15, 7.93) * mm});
            skLineSegment(sketch, "E144", {"start": v(-31.3, 6.86) * mm, "end": v(-31.3, 10.2) * mm});
            skLineSegment(sketch, "E145", {"start": v(-31.3, 10.2) * mm, "end": v(-38.7, 10.2) * mm});
            skLineSegment(sketch, "E146", {"start": v(-38.7, 10.2) * mm, "end": v(-38.7, 6.86) * mm});
            skLineSegment(sketch, "E147.MirrorCS", {"start": v(38.7, 10.2) * mm, "end": v(38.7, 6.86) * mm});
            skLineSegment(sketch, "E148.MirrorCS", {"start": v(38.7, 6.86) * mm, "end": v(35, 9) * mm});
            skLineSegment(sketch, "E149.MirrorCS", {"start": v(35, 9) * mm, "end": v(31.3, 6.86) * mm});
            skLineSegment(sketch, "E150.MirrorCS", {"start": v(31.3, 6.86) * mm, "end": v(31.3, 10.2) * mm});
            skLineSegment(sketch, "E151.MirrorCS", {"start": v(31.3, 10.2) * mm, "end": v(38.7, 10.2) * mm});
            skPoint(sketch, "E152.MirrorP", {"position": v(35, 4.73) * mm});
            skSolve(sketch);
        }
        {
            var Q0;
            {var subQ5=sQuery(id+"F41.wireOp",EDGE,"E143.0");Q0=makeQuery(id+"F41.imprint","IMPRINT",FACE,{"disambiguationData":[TD([[makeQuery(id+"F41.imprint","IMPRINT",EDGE,{"derivedFrom":subQ5}),1.0]])]});}
            var Q1;
            Q1=makeQuery(id+"F41.imprint","IMPRINT",FACE,{"disambiguationData":[TD([[makeQuery(id+"F41.imprint","IMPRINT",EDGE,{"derivedFrom":sQuery(id+"F41.wireOp",EDGE,"E147.MirrorCS")}),-1.0]])]});
            var Q2;
            Q2=makeQuery(id+"F10.opExtrude","SWEPT_FACE",FACE,{"disambiguationData":[OSD([sQuery(id+"F9.wireOp",EDGE,"E0.left")])]});
            extrude(context, id + "F42", {"entities" : qUnion([Q0, Q1]), "operationType" : NewBodyOperationType.ADD, "endBound" : BoundingType.UP_TO_SURFACE, "endBoundEntityFace" : qUnion([Q2]), "depth" : 25 * mm});
        }
        {
            var Q0;
            Q0=makeQuery(id+"F10.opExtrude","SWEPT_FACE",FACE,{"disambiguationData":[OSD([sQuery(id+"F9.wireOp",EDGE,"E0.left")])]});
            var sketch = newSketch(context, id + "F43", { "sketchPlane" : qUnion([Q0])});
            skPoint(sketch, "E153.0", {"position": v(-35, 4.73) * mm});
            skPoint(sketch, "E153.1", {"position": v(35, 4.73) * mm});
            skSolve(sketch);
        }
        {
            var Q0;
            Q0=sQuery(id+"F43.wireOp",VERTEX,"E153.0");
            var Q1;
            Q1=sQuery(id+"F43.wireOp",VERTEX,"E153.1");
            var Q2;
            Q2=makeQuery(id+"F10.opExtrude","SWEPT_BODY",BODY,{"disambiguationData":[OSD([sQuery(id+"F9.wireOp",EDGE,"E0.bottom"),sQuery(id+"F9.wireOp",EDGE,"E0.top"),sQuery(id+"F9.wireOp",EDGE,"E0.left"),sQuery(id+"F9.wireOp",EDGE,"E0.right")])]});
            hole(context, id + "F44", {"style" : HoleStyle.SIMPLE, "endStyle" : HoleEndStyle.THROUGH, "standardTappedOrClearance" : lookupTablePath({ "standard" : "ISO", "fit" : "Normal", "size" : "M4", "type" : "Clearance" }), "standardBlindInLast" : lookupTablePath({ "fit" : "Standard", "standard" : "ISO", "size" : "M4", "type" : "Clearance" }), "holeDiameter" : 4.4 * mm, "locations" : qUnion([Q0, Q1]), "scope" : qUnion([Q2]), "isTappedThrough" : true});
        }
        {
            var Q0;
            Q0=makeQuery(id+"F10.opExtrude","CAP_FACE",FACE,{"disambiguationData":[OSD([sQuery(id+"F9.wireOp",EDGE,"E0.bottom"),sQuery(id+"F9.wireOp",EDGE,"E0.top"),sQuery(id+"F9.wireOp",EDGE,"E0.left"),sQuery(id+"F9.wireOp",EDGE,"E0.right")])],"isStart":true});
            var sketch = newSketch(context, id + "F45", { "sketchPlane" : qUnion([Q0])});
            skLineSegment(sketch, "E154.bottom", {"start": v(5.14, 31.03) * mm, "end": v(-5.14, 31.03) * mm});
            skLineSegment(sketch, "E154.top", {"start": v(5.14, -31.03) * mm, "end": v(-5.14, -31.03) * mm});
            skLineSegment(sketch, "E154.left", {"start": v(10.14, 26.03) * mm, "end": v(10.14, -26.03) * mm});
            skLineSegment(sketch, "E154.right", {"start": v(-10.14, 26.03) * mm, "end": v(-10.14, -26.03) * mm});
            skPoint(sketch, "E154.middle", {"position": v(0, 0) * mm});
            skPoint(sketch, "E155.visualSharp", {"position": v(-10.14, 31.03) * mm});
            skArc(sketch, "E155.filletArc", {"start": v(-5.14, 31.03) * mm, "mid": v(-8.68, 29.57) * mm, "end": v(-10.14, 26.03) * mm});
            skPoint(sketch, "E156.visualSharp", {"position": v(10.14, 31.03) * mm});
            skArc(sketch, "E156.filletArc", {"start": v(10.14, 26.03) * mm, "mid": v(8.68, 29.57) * mm, "end": v(5.14, 31.03) * mm});
            skPoint(sketch, "E157.visualSharp", {"position": v(10.14, -31.03) * mm});
            skArc(sketch, "E157.filletArc", {"start": v(5.14, -31.03) * mm, "mid": v(8.68, -29.57) * mm, "end": v(10.14, -26.03) * mm});
            skPoint(sketch, "E158.visualSharp", {"position": v(-10.14, -31.03) * mm});
            skArc(sketch, "E158.filletArc", {"start": v(-10.14, -26.03) * mm, "mid": v(-8.68, -29.57) * mm, "end": v(-5.14, -31.03) * mm});
            skSolve(sketch);
        }
        {
            var Q0;
            Q0=makeQuery(id+"F45.imprint","IMPRINT",FACE,{"disambiguationData":[TD([[makeQuery(id+"F45.imprint","IMPRINT",EDGE,{"derivedFrom":sQuery(id+"F45.wireOp",EDGE,"E154.bottom")}),1.0]])]});
            extrude(context, id + "F46", {"entities" : qUnion([Q0]), "operationType" : NewBodyOperationType.REMOVE, "endBound" : BoundingType.THROUGH_ALL, "oppositeDirection" : true, "depth" : 25 * mm});
        }
        {
            var Q0;
            Q0=makeQuery(id+"F10.opExtrude","SWEPT_FACE",FACE,{"disambiguationData":[OSD([sQuery(id+"F9.wireOp",EDGE,"E0.right")])]});
            var sketch = newSketch(context, id + "F47", { "sketchPlane" : qUnion([Q0])});
            skLineSegment(sketch, "E159.bottom", {"start": v(32.5, 40.56) * mm, "end": v(-32.5, 40.56) * mm});
            skLineSegment(sketch, "E159.top", {"start": v(27.5, 24.24) * mm, "end": v(-27.5, 24.24) * mm});
            skLineSegment(sketch, "E159.left", {"start": v(32.5, 40.56) * mm, "end": v(32.5, 29.24) * mm});
            skLineSegment(sketch, "E159.right", {"start": v(-32.5, 40.56) * mm, "end": v(-32.5, 29.24) * mm});
            skPoint(sketch, "E159.middle", {"position": v(0, 32.4) * mm});
            skPoint(sketch, "E160.visualSharp", {"position": v(-32.5, 24.24) * mm});
            skArc(sketch, "E160.filletArc", {"start": v(-32.5, 29.24) * mm, "mid": v(-31.04, 25.7) * mm, "end": v(-27.5, 24.24) * mm});
            skPoint(sketch, "E161.visualSharp", {"position": v(32.5, 24.24) * mm});
            skArc(sketch, "E161.filletArc", {"start": v(27.5, 24.24) * mm, "mid": v(31.04, 25.7) * mm, "end": v(32.5, 29.24) * mm});
            skSolve(sketch);
        }
        {
            var Q0;
            Q0=makeQuery(id+"F47.imprint","IMPRINT",FACE,{"disambiguationData":[TD([[makeQuery(id+"F47.imprint","IMPRINT",EDGE,{"derivedFrom":sQuery(id+"F47.wireOp",EDGE,"E159.top")}),-1.0]])]});
            extrude(context, id + "F48", {"entities" : qUnion([Q0]), "operationType" : NewBodyOperationType.REMOVE, "endBound" : BoundingType.THROUGH_ALL, "oppositeDirection" : true, "depth" : 25 * mm});
        }
        {
            var Q0;
            Q0=makeQuery(id+"F28.opExtrude","SWEPT_EDGE",EDGE,{"disambiguationData":[OSD([sQuery(id+"F27.wireOp",EDGE,"E59.MirrorCS"),sQuery(id+"F27.wireOp",EDGE,"E56.MirrorCS")])]});
            var Q1;
            Q1=makeQuery(id+"F28.opExtrude","SWEPT_EDGE",EDGE,{"disambiguationData":[OSD([sQuery(id+"F27.wireOp",EDGE,"E54.top"),sQuery(id+"F27.wireOp",EDGE,"E54.right")])]});
            var Q2;
            Q2=makeQuery(id+"F37.opExtrude","CAP_EDGE",EDGE,{"disambiguationData":[OSD([sQuery(id+"F36.wireOp",EDGE,"E113.MirrorCS")])],"isStart":false});
            var Q3;
            Q3=makeQuery(id+"F37.opExtrude","CAP_EDGE",EDGE,{"disambiguationData":[OSD([sQuery(id+"F36.wireOp",EDGE,"E86")])],"isStart":false});
            var Q4;
            Q4=makeQuery(id+"F37.opExtrude","CAP_EDGE",EDGE,{"disambiguationData":[OSD([sQuery(id+"F36.wireOp",EDGE,"E98.MirrorCS")])],"isStart":false});
            var Q5;
            Q5=makeQuery(id+"F37.opExtrude","CAP_EDGE",EDGE,{"disambiguationData":[OSD([sQuery(id+"F36.wireOp",EDGE,"E106.MirrorCS")])],"isStart":false});
            fillet(context, id + "F49", {"entities" : qUnion([Q0, Q1, Q2, Q3, Q4, Q5]), "radius" : 2 * mm, "tangentPropagation" : true, "allowEdgeOverflow" : false});
        }
        {
            var Q0;
            Q0=makeQuery(id+"F10.opExtrude","SWEPT_BODY",BODY,{"disambiguationData":[OSD([sQuery(id+"F9.wireOp",EDGE,"E0.bottom"),sQuery(id+"F9.wireOp",EDGE,"E0.top"),sQuery(id+"F9.wireOp",EDGE,"E0.left"),sQuery(id+"F9.wireOp",EDGE,"E0.right")])]});
            var Q1;
            {var subQ0=sQuery(id+"F9.wireOp",EDGE,"E0.right");var subQ1=sQuery(id+"F9.wireOp",EDGE,"E0.top");var subQ3=sQuery(id+"F9.wireOp",EDGE,"E0.bottom");Q1=makeQuery(id+"F19.boolean.opBoolean","MERGE",FACE,{"derivedFrom":[makeQuery(id+"F15.boolean.opBoolean","SPLIT",FACE,{"disambiguationData":[TD([makeQuery(id+"F10.opExtrude","SWEPT_FACE",FACE,{"disambiguationData":[OSD([subQ0])]})])],"derivedFrom":makeQuery(id+"F10.opExtrude","CAP_FACE",FACE,{"disambiguationData":[OSD([subQ3,subQ1,sQuery(id+"F9.wireOp",EDGE,"E0.left"),subQ0])],"isStart":false})}),makeQuery(id+"F19.opExtrude","CAP_FACE",FACE,{"disambiguationData":[OSD([sQuery(id+"F18.wireOp",EDGE,"E21.MirrorCS"),sQuery(id+"F18.wireOp",EDGE,"E22.MirrorCS"),sQuery(id+"F18.wireOp",EDGE,"E23.MirrorCS"),sQuery(id+"F18.wireOp",EDGE,"E24.MirrorCS"),sQuery(id+"F18.wireOp",EDGE,"E25.MirrorCS")])],"isStart":true})]});}
            mirror(context, id + "F50", {"entities" : qUnion([Q0]), "mirrorPlane" : qUnion([Q1])});
        }
        {
            var Q0;
            Q0=makeQuery(id+"F10.opExtrude","CAP_FACE",FACE,{"disambiguationData":[OSD([sQuery(id+"F9.wireOp",EDGE,"E0.bottom"),sQuery(id+"F9.wireOp",EDGE,"E0.top"),sQuery(id+"F9.wireOp",EDGE,"E0.left"),sQuery(id+"F9.wireOp",EDGE,"E0.right")])],"isStart":true});
            var sketch = newSketch(context, id + "F51", { "sketchPlane" : qUnion([Q0])});
            skLineSegment(sketch, "E162.bottom", {"start": v(-22.5, 52.5) * mm, "end": v(22.5, 52.5) * mm});
            skLineSegment(sketch, "E162.top", {"start": v(-22.5, -52.5) * mm, "end": v(22.5, -52.5) * mm});
            skLineSegment(sketch, "E162.left", {"start": v(-22.5, 52.5) * mm, "end": v(-22.5, -52.5) * mm});
            skLineSegment(sketch, "E162.right", {"start": v(22.5, 52.5) * mm, "end": v(22.5, -52.5) * mm});
            skPoint(sketch, "E162.middle", {"position": v(0, 0) * mm});
            skSolve(sketch);
        }
        {
            var Q0;
            Q0=makeQuery(id+"F51.imprint","IMPRINT",FACE,{"disambiguationData":[TD([[makeQuery(id+"F51.imprint","IMPRINT",EDGE,{"derivedFrom":sQuery(id+"F51.wireOp",EDGE,"E162.bottom")}),-1.0]])]});
            extrude(context, id + "F52", {"entities" : qUnion([Q0]), "operationType" : NewBodyOperationType.ADD, "depth" : 3 * mm});
        }
        {
            var Q0;
            Q0=makeQuery(id+"F52.opExtrude","CAP_FACE",FACE,{"disambiguationData":[OSD([sQuery(id+"F51.wireOp",EDGE,"E162.bottom"),sQuery(id+"F51.wireOp",EDGE,"E162.top"),sQuery(id+"F51.wireOp",EDGE,"E162.left"),sQuery(id+"F51.wireOp",EDGE,"E162.right")])],"isStart":false});
            cPlane(context, id + "F53", {"entities" : qUnion([Q0]), "cplaneType" : CPlaneType.OFFSET, "offset" : (getVariable(context, 'MIN_WALL_THICKNESS')) * mm, "oppositeDirection" : true, "width" : 150 * mm, "height" : 150 * mm});
        }
        {
            var Q0;
            Q0=qCreatedBy(id+"F53.planeOp",FACE);
            var sketch = newSketch(context, id + "F54", { "sketchPlane" : qUnion([Q0])});
            skLineSegment(sketch, "E163.bottom", {"start": v(-18, 34) * mm, "end": v(18, 34) * mm, "construction": true});
            skLineSegment(sketch, "E163.top", {"start": v(-18, -34) * mm, "end": v(18, -34) * mm, "construction": true});
            skLineSegment(sketch, "E163.left", {"start": v(-18, 34) * mm, "end": v(-18, -34) * mm, "construction": true});
            skLineSegment(sketch, "E163.right", {"start": v(18, 34) * mm, "end": v(18, -34) * mm, "construction": true});
            skPoint(sketch, "E163.middle", {"position": v(0, 0) * mm});
            skLineSegment(sketch, "E164", {"start": v(-18, 0) * mm, "end": v(18, 0) * mm, "construction": true});
            skLineSegment(sketch, "E165", {"start": v(0, 34) * mm, "end": v(0, -34) * mm, "construction": true});
            skCircle(sketch, "E166.cCircle", {"center": v(-18, 34) * mm, "radius": 2.85 * mm, "construction": true});
            skLineSegment(sketch, "E166.0", {"start": v(-20.85, 35.65) * mm, "end": v(-18, 37.3) * mm});
            skLineSegment(sketch, "E166.1", {"start": v(-18, 37.3) * mm, "end": v(-15.15, 35.65) * mm});
            skLineSegment(sketch, "E166.2", {"start": v(-15.15, 35.65) * mm, "end": v(-15.15, 32.35) * mm});
            skLineSegment(sketch, "E166.3", {"start": v(-15.15, 32.35) * mm, "end": v(-18, 30.7) * mm});
            skLineSegment(sketch, "E166.4", {"start": v(-18, 30.7) * mm, "end": v(-20.85, 32.35) * mm});
            skLineSegment(sketch, "E166.5", {"start": v(-20.85, 32.35) * mm, "end": v(-20.85, 35.65) * mm});
            skCircle(sketch, "E167.MirrorC", {"center": v(-18, -34) * mm, "radius": 2.85 * mm, "construction": true});
            skLineSegment(sketch, "E168.MirrorCS", {"start": v(-20.85, -35.65) * mm, "end": v(-18, -37.3) * mm});
            skLineSegment(sketch, "E169.MirrorCS", {"start": v(-18, -37.3) * mm, "end": v(-15.15, -35.65) * mm});
            skLineSegment(sketch, "E170.MirrorCS", {"start": v(-15.15, -35.65) * mm, "end": v(-15.15, -32.35) * mm});
            skLineSegment(sketch, "E171.MirrorCS", {"start": v(-15.15, -32.35) * mm, "end": v(-18, -30.7) * mm});
            skLineSegment(sketch, "E172.MirrorCS", {"start": v(-20.85, -32.35) * mm, "end": v(-20.85, -35.65) * mm});
            skLineSegment(sketch, "E173.MirrorCS", {"start": v(-18, -30.7) * mm, "end": v(-20.85, -32.35) * mm});
            skLineSegment(sketch, "E174.MirrorCS", {"start": v(18, 30.7) * mm, "end": v(20.85, 32.35) * mm});
            skPoint(sketch, "E175.MirrorP", {"position": v(18, 34) * mm});
            skLineSegment(sketch, "E176.MirrorCS", {"start": v(20.85, 32.35) * mm, "end": v(20.85, 35.65) * mm});
            skCircle(sketch, "E177.MirrorC", {"center": v(18, 34) * mm, "radius": 2.85 * mm, "construction": true});
            skLineSegment(sketch, "E178.MirrorCS", {"start": v(15.15, 35.65) * mm, "end": v(15.15, 32.35) * mm});
            skLineSegment(sketch, "E179.MirrorCS", {"start": v(20.85, 35.65) * mm, "end": v(18, 37.3) * mm});
            skLineSegment(sketch, "E180.MirrorCS", {"start": v(15.15, 32.35) * mm, "end": v(18, 30.7) * mm});
            skLineSegment(sketch, "E181.MirrorCS", {"start": v(18, 37.3) * mm, "end": v(15.15, 35.65) * mm});
            skLineSegment(sketch, "E182.MirrorCS", {"start": v(18, -30.7) * mm, "end": v(20.85, -32.35) * mm});
            skLineSegment(sketch, "E183.MirrorCS", {"start": v(15.15, -35.65) * mm, "end": v(15.15, -32.35) * mm});
            skLineSegment(sketch, "E184.MirrorCS", {"start": v(20.85, -32.35) * mm, "end": v(20.85, -35.65) * mm});
            skLineSegment(sketch, "E185.MirrorCS", {"start": v(18, -37.3) * mm, "end": v(15.15, -35.65) * mm});
            skCircle(sketch, "E186.MirrorC", {"center": v(18, -34) * mm, "radius": 2.85 * mm, "construction": true});
            skLineSegment(sketch, "E187.MirrorCS", {"start": v(20.85, -35.65) * mm, "end": v(18, -37.3) * mm});
            skLineSegment(sketch, "E188.MirrorCS", {"start": v(15.15, -32.35) * mm, "end": v(18, -30.7) * mm});
            skSolve(sketch);
        }
        {
            var Q0;
            Q0 = qSketchRegion(id + "F54", true);
            extrude(context, id + "F55", {"entities" : qUnion([Q0]), "operationType" : NewBodyOperationType.REMOVE, "endBound" : BoundingType.THROUGH_ALL, "oppositeDirection" : true, "depth" : 25 * mm});
        }
        {
            var Q0;
            Q0=sQuery(id+"F54.wireOp",VERTEX,"E166.cCircle.center");
            var Q1;
            Q1=sQuery(id+"F54.wireOp",VERTEX,"E167.MirrorC.center");
            var Q2;
            Q2=sQuery(id+"F54.wireOp",VERTEX,"E186.MirrorC.center");
            var Q3;
            Q3=sQuery(id+"F54.wireOp",VERTEX,"E175.MirrorP");
            var Q4;
            Q4=makeQuery(id+"F10.opExtrude","SWEPT_BODY",BODY,{"disambiguationData":[OSD([sQuery(id+"F9.wireOp",EDGE,"E0.bottom"),sQuery(id+"F9.wireOp",EDGE,"E0.top"),sQuery(id+"F9.wireOp",EDGE,"E0.left"),sQuery(id+"F9.wireOp",EDGE,"E0.right")])]});
            hole(context, id + "F56", {"style" : HoleStyle.SIMPLE, "endStyle" : HoleEndStyle.THROUGH, "oppositeDirection" : true, "standardTappedOrClearance" : lookupTablePath({ "standard" : "ISO", "fit" : "Normal", "size" : "M3", "type" : "Clearance" }), "standardBlindInLast" : lookupTablePath({ "fit" : "Standard", "standard" : "ISO", "size" : "M3", "type" : "Clearance" }), "holeDiameter" : 3.3 * mm, "locations" : qUnion([Q0, Q1, Q2, Q3]), "scope" : qUnion([Q4]), "isTappedThrough" : true});
        }
        {
            var Q0;
            Q0=makeQuery(id+"F10.opExtrude","SWEPT_FACE",FACE,{"disambiguationData":[OSD([sQuery(id+"F9.wireOp",EDGE,"E0.top")])]});
            var sketch = newSketch(context, id + "F57", { "sketchPlane" : qUnion([Q0])});
            skLineSegment(sketch, "E189.0", {"start": v(32.5, 64.8) * mm, "end": v(-32.5, 64.8) * mm, "construction": true});
            skLineSegment(sketch, "E190", {"start": v(0, 64.8) * mm, "end": v(0, 0) * mm, "construction": true});
            skLineSegment(sketch, "E191.bottom", {"start": v(32.5, 64.9) * mm, "end": v(-32.5, 64.9) * mm});
            skLineSegment(sketch, "E191.top", {"start": v(32.5, -0.1) * mm, "end": v(-32.5, -0.1) * mm});
            skLineSegment(sketch, "E191.left", {"start": v(32.5, 64.9) * mm, "end": v(32.5, -0.1) * mm});
            skLineSegment(sketch, "E191.right", {"start": v(-32.5, 64.9) * mm, "end": v(-32.5, -0.1) * mm});
            skPoint(sketch, "E191.middle", {"position": v(0, 32.4) * mm});
            skLineSegment(sketch, "E192", {"start": v(0, 64.9) * mm, "end": v(0, 36.4) * mm, "construction": true});
            skCircle(sketch, "E193", {"center": v(0, 36.4) * mm, "radius": 17.5 * mm});
            skSolve(sketch);
        }
        {
            var Q0;
            {var subQ9=sQuery(id+"F57.wireOp",EDGE,"E191.bottom");Q0=makeQuery(id+"F57.imprint","IMPRINT",FACE,{"disambiguationData":[TD([[makeQuery(id+"F57.imprint","IMPRINT",EDGE,{"derivedFrom":subQ9}),1.0]])]});}
            var Q1;
            {var subQ0=sQuery(id+"F9.wireOp",EDGE,"E0.top");var subQ11=makeQuery(id+"F10.opExtrude","CAP_EDGE",EDGE,{"disambiguationData":[OSD([subQ0])],"isStart":true});Q1=makeQuery(id+"F57.imprint","IMPRINT",FACE,{"disambiguationData":[TD([[makeQuery(id+"F57.imprint","IMPRINT",EDGE,{"derivedFrom":subQ11}),-1.0]])]});}
            var Q2;
            {var subQ0=makeQuery(id+"F10.opExtrude","SWEPT_FACE",FACE,{"disambiguationData":[OSD([sQuery(id+"F9.wireOp",EDGE,"E0.top")])]});Q2=makeQuery(id+"F57.imprint","IMPRINT",FACE,{"disambiguationData":[TD([[makeQuery(id+"F57.imprint","IMPRINT",EDGE,{"derivedFrom":makeQuery(id+"F22.boolean.opBoolean","INTERSECT",EDGE,{"derivedFrom":[subQ0,makeQuery(id+"F22.opExtrude","SWEPT_FACE",FACE,{"disambiguationData":[OSD([sQuery(id+"F21.wireOp",EDGE,"E42")])]})]})}),1.0]])]});}
            var Q3;
            {var subQ0=makeQuery(id+"F10.opExtrude","SWEPT_FACE",FACE,{"disambiguationData":[OSD([sQuery(id+"F9.wireOp",EDGE,"E0.top")])]});Q3=makeQuery(id+"F57.imprint","IMPRINT",FACE,{"disambiguationData":[TD([[makeQuery(id+"F57.imprint","IMPRINT",EDGE,{"derivedFrom":makeQuery(id+"F22.boolean.opBoolean","INTERSECT",EDGE,{"derivedFrom":[subQ0,makeQuery(id+"F22.opExtrude","SWEPT_FACE",FACE,{"disambiguationData":[OSD([sQuery(id+"F21.wireOp",EDGE,"E45.MirrorCS")])]})]})}),-1.0]])]});}
            extrude(context, id + "F58", {"entities" : qUnion([Q0, Q1, Q2, Q3]), "depth" : (getVariable(context, 'FRONT_PLATE_THICKNESS')) * mm});
        }
        {
            var Q0;
            Q0=makeQuery(id+"F58.opExtrude","CAP_FACE",FACE,{"disambiguationData":[OSD([sQuery(id+"F9.wireOp",EDGE,"E0.top"),sQuery(id+"F57.wireOp",EDGE,"E191.bottom"),sQuery(id+"F57.wireOp",EDGE,"E191.left"),sQuery(id+"F57.wireOp",EDGE,"E191.right"),sQuery(id+"F57.wireOp",EDGE,"E193")])],"isStart":false});
            var sketch = newSketch(context, id + "F59", { "sketchPlane" : qUnion([Q0])});
            skLineSegment(sketch, "E194", {"start": v(32.5, 0) * mm, "end": v(-32.5, 64.9) * mm, "construction": true});
            skCircle(sketch, "E195", {"center": v(0, 32.45) * mm, "radius": 40.74 * mm, "construction": true});
            skPoint(sketch, "E196", {"position": v(-28.83, 61.23) * mm});
            skPoint(sketch, "E197.1.0", {"position": v(-28.78, 3.62) * mm});
            skPoint(sketch, "E197.2.0", {"position": v(28.83, 3.67) * mm});
            skPoint(sketch, "E197.3.0", {"position": v(28.78, 61.28) * mm});
            skSolve(sketch);
        }
        {
            var Q0;
            Q0=sQuery(id+"F59.wireOp",VERTEX,"E196");
            var Q1;
            Q1=sQuery(id+"F59.wireOp",VERTEX,"E197.3.0");
            var Q2;
            Q2=sQuery(id+"F59.wireOp",VERTEX,"E197.2.0");
            var Q3;
            Q3=sQuery(id+"F59.wireOp",VERTEX,"E197.1.0");
            var Q4;
            Q4=makeQuery(id+"F58.opExtrude","SWEPT_BODY",BODY,{"disambiguationData":[OSD([sQuery(id+"F9.wireOp",EDGE,"E0.top"),sQuery(id+"F57.wireOp",EDGE,"E191.bottom"),sQuery(id+"F57.wireOp",EDGE,"E191.left"),sQuery(id+"F57.wireOp",EDGE,"E191.right"),sQuery(id+"F57.wireOp",EDGE,"E193")])]});
            hole(context, id + "F60", {"style" : HoleStyle.SIMPLE, "endStyle" : HoleEndStyle.THROUGH, "standardTappedOrClearance" : lookupTablePath({ "standard" : "ISO", "fit" : "Normal", "size" : "M3", "type" : "Clearance" }), "standardBlindInLast" : lookupTablePath({ "fit" : "Standard", "standard" : "ISO", "size" : "M3", "type" : "Clearance" }), "holeDiameter" : 3.3 * mm, "locations" : qUnion([Q0, Q1, Q2, Q3]), "scope" : qUnion([Q4]), "isTappedThrough" : true});
        }
        {
            var Q0;
            Q0=makeQuery(id+"F58.opExtrude","CAP_FACE",FACE,{"disambiguationData":[OSD([sQuery(id+"F9.wireOp",EDGE,"E0.top"),sQuery(id+"F57.wireOp",EDGE,"E191.bottom"),sQuery(id+"F57.wireOp",EDGE,"E191.left"),sQuery(id+"F57.wireOp",EDGE,"E191.right"),sQuery(id+"F57.wireOp",EDGE,"E193")])],"isStart":false});
            var sketch = newSketch(context, id + "F61", { "sketchPlane" : qUnion([Q0])});
            skLineSegment(sketch, "E198", {"start": v(-32.5, 64.9) * mm, "end": v(32.5, 0) * mm, "construction": true});
            skCircle(sketch, "E199", {"center": v(0, 32.45) * mm, "radius": 25.4 * mm, "construction": true});
            skLineSegment(sketch, "E200", {"start": v(0, 32.45) * mm, "end": v(12.7, 54.45) * mm, "construction": true});
            skCircle(sketch, "E201", {"center": v(12.7, 54.45) * mm, "radius": 2 * mm});
            skCircle(sketch, "E202.1.0", {"center": v(-12.7, 54.45) * mm, "radius": 2 * mm});
            skCircle(sketch, "E202.2.0", {"center": v(-25.4, 32.45) * mm, "radius": 2 * mm});
            skCircle(sketch, "E202.3.0", {"center": v(-12.7, 10.45) * mm, "radius": 2 * mm});
            skCircle(sketch, "E202.4.0", {"center": v(12.7, 10.45) * mm, "radius": 2 * mm});
            skCircle(sketch, "E202.5.0", {"center": v(25.4, 32.45) * mm, "radius": 2 * mm});
            skLineSegment(sketch, "E203", {"start": v(0, 32.45) * mm, "end": v(0, 69.63) * mm, "construction": true});
            skSolve(sketch);
        }
        {
            var Q0;
            Q0 = qSketchRegion(id + "F61", true);
            extrude(context, id + "F62", {"entities" : qUnion([Q0]), "operationType" : NewBodyOperationType.REMOVE, "endBound" : BoundingType.THROUGH_ALL, "oppositeDirection" : true, "depth" : 25 * mm});
        }
        {
            var Q0;
            Q0=makeQuery(id+"F58.opExtrude","CAP_EDGE",EDGE,{"disambiguationData":[OSD([sQuery(id+"F57.wireOp",EDGE,"E193")])],"isStart":false});
            var Q1;
            Q1=makeQuery(id+"F50.opPattern","COPY",EDGE,{"derivedFrom":makeQuery(id+"F15.boolean.opBoolean","COPY",EDGE,{"derivedFrom":makeQuery(id+"F15.opExtrude","CAP_EDGE",EDGE,{"disambiguationData":[OSD([sQuery(id+"F14.wireOp",EDGE,"E4")])],"isStart":true})}),"instanceName":"1"});
            var Q2;
            Q2=makeQuery(id+"F15.boolean.opBoolean","COPY",EDGE,{"derivedFrom":makeQuery(id+"F15.opExtrude","CAP_EDGE",EDGE,{"disambiguationData":[OSD([sQuery(id+"F14.wireOp",EDGE,"E4")])],"isStart":true})});
            var Q3;
            Q3=makeQuery(id+"F50.opPattern","COPY",EDGE,{"derivedFrom":makeQuery(id+"F46.boolean.opBoolean","COPY",EDGE,{"derivedFrom":makeQuery(id+"F46.opExtrude","CAP_EDGE",EDGE,{"disambiguationData":[OSD([sQuery(id+"F45.wireOp",EDGE,"E155.filletArc")])],"isStart":true})}),"instanceName":"1"});
            var Q4;
            Q4=makeQuery(id+"F50.opPattern","COPY",EDGE,{"derivedFrom":makeQuery(id+"F48.boolean.opBoolean","COPY",EDGE,{"derivedFrom":makeQuery(id+"F48.opExtrude","CAP_EDGE",EDGE,{"disambiguationData":[OSD([sQuery(id+"F47.wireOp",EDGE,"E159.top")])],"isStart":true})}),"instanceName":"1"});
            var Q5;
            Q5=makeQuery(id+"F48.boolean.opBoolean","COPY",EDGE,{"derivedFrom":makeQuery(id+"F48.opExtrude","CAP_EDGE",EDGE,{"disambiguationData":[OSD([sQuery(id+"F47.wireOp",EDGE,"E159.top")])],"isStart":true})});
            var Q6;
            Q6=makeQuery(id+"F50.opPattern","COPY",EDGE,{"derivedFrom":makeQuery(id+"F48.boolean.opBoolean","INTERSECT",EDGE,{"derivedFrom":[makeQuery(id+"F10.opExtrude","SWEPT_FACE",FACE,{"disambiguationData":[OSD([sQuery(id+"F9.wireOp",EDGE,"E0.left")])]}),makeQuery(id+"F48.opExtrude","SWEPT_FACE",FACE,{"disambiguationData":[OSD([sQuery(id+"F47.wireOp",EDGE,"E159.top")])]})]}),"instanceName":"1"});
            var Q7;
            Q7=makeQuery(id+"F48.boolean.opBoolean","INTERSECT",EDGE,{"derivedFrom":[makeQuery(id+"F10.opExtrude","SWEPT_FACE",FACE,{"disambiguationData":[OSD([sQuery(id+"F9.wireOp",EDGE,"E0.left")])]}),makeQuery(id+"F48.opExtrude","SWEPT_FACE",FACE,{"disambiguationData":[OSD([sQuery(id+"F47.wireOp",EDGE,"E159.top")])]})]});
            var Q8;
            Q8=makeQuery(id+"F52.opExtrude","CAP_EDGE",EDGE,{"disambiguationData":[OSD([sQuery(id+"F45.wireOp",EDGE,"E154.right")])],"isStart":false});
            chamfer(context, id + "F63", {"entities" : qUnion([Q0, Q1, Q2, Q3, Q4, Q5, Q6, Q7, Q8]), "width" : 2 * mm, "tangentPropagation" : true});
        }
        {
            var Q0;
            Q0=makeQuery(id+"F50.opPattern","COPY",FACE,{"derivedFrom":makeQuery(id+"F10.opExtrude","CAP_FACE",FACE,{"disambiguationData":[OSD([sQuery(id+"F9.wireOp",EDGE,"E0.bottom"),sQuery(id+"F9.wireOp",EDGE,"E0.top"),sQuery(id+"F9.wireOp",EDGE,"E0.left"),sQuery(id+"F9.wireOp",EDGE,"E0.right")])],"isStart":true}),"instanceName":"1"});
            var sketch = newSketch(context, id + "F64", { "sketchPlane" : qUnion([Q0])});
            skLineSegment(sketch, "E204.bottom", {"start": v(17.5, 46.5) * mm, "end": v(-17.5, 46.5) * mm, "construction": true});
            skLineSegment(sketch, "E204.top", {"start": v(17.5, -46.5) * mm, "end": v(-17.5, -46.5) * mm, "construction": true});
            skLineSegment(sketch, "E204.left", {"start": v(17.5, 46.5) * mm, "end": v(17.5, -46.5) * mm, "construction": true});
            skLineSegment(sketch, "E204.right", {"start": v(-17.5, 46.5) * mm, "end": v(-17.5, -46.5) * mm, "construction": true});
            skPoint(sketch, "E204.middle", {"position": v(0, 0) * mm});
            skCircle(sketch, "E205", {"center": v(-17.5, 46.5) * mm, "radius": 2.65 * mm});
            skCircle(sketch, "E206", {"center": v(17.5, 46.5) * mm, "radius": 2.65 * mm});
            skLineSegment(sketch, "E207", {"start": v(0, 0) * mm, "end": v(17.5, 0) * mm, "construction": true});
            skCircle(sketch, "E208.MirrorC", {"center": v(17.5, -46.5) * mm, "radius": 2.65 * mm});
            skCircle(sketch, "E209.MirrorC", {"center": v(-17.5, -46.5) * mm, "radius": 2.65 * mm});
            skSolve(sketch);
        }
        {
            var Q0;
            Q0 = qSketchRegion(id + "F64", true);
            extrude(context, id + "F65", {"entities" : qUnion([Q0]), "operationType" : NewBodyOperationType.REMOVE, "endBound" : BoundingType.THROUGH_ALL, "oppositeDirection" : true, "depth" : 25 * mm});
        }
        {
            var Q0;
            Q0=makeQuery(id+"F50.opPattern","COPY",FACE,{"derivedFrom":makeQuery(id+"F10.opExtrude","CAP_FACE",FACE,{"disambiguationData":[OSD([sQuery(id+"F9.wireOp",EDGE,"E0.bottom"),sQuery(id+"F9.wireOp",EDGE,"E0.top"),sQuery(id+"F9.wireOp",EDGE,"E0.left"),sQuery(id+"F9.wireOp",EDGE,"E0.right")])],"isStart":true}),"instanceName":"1"});
            var sketch = newSketch(context, id + "F66", { "sketchPlane" : qUnion([Q0])});
            skLineSegment(sketch, "E210.bottom", {"start": v(24.5, 53.5) * mm, "end": v(-24.5, 53.5) * mm});
            skLineSegment(sketch, "E210.top", {"start": v(24.5, -53.5) * mm, "end": v(-24.5, -53.5) * mm});
            skLineSegment(sketch, "E210.left", {"start": v(24.5, 53.5) * mm, "end": v(24.5, -53.5) * mm});
            skLineSegment(sketch, "E210.right", {"start": v(-24.5, 53.5) * mm, "end": v(-24.5, -53.5) * mm});
            skPoint(sketch, "E210.middle", {"position": v(0, 0) * mm});
            skSolve(sketch);
        }
        {
            var Q0;
            Q0=makeQuery(id+"F66.imprint","IMPRINT",FACE,{"disambiguationData":[TD([[makeQuery(id+"F66.imprint","IMPRINT",EDGE,{"derivedFrom":sQuery(id+"F66.wireOp",EDGE,"E210.bottom")}),1.0]])]});
            extrude(context, id + "F67", {"entities" : qUnion([Q0]), "operationType" : NewBodyOperationType.ADD, "depth" : 2.5 * mm});
        }
        {
            var Q0;
            Q0=makeQuery(id+"F50.opPattern","COPY",FACE,{"derivedFrom":makeQuery(id+"F10.opExtrude","CAP_FACE",FACE,{"disambiguationData":[OSD([sQuery(id+"F9.wireOp",EDGE,"E0.bottom"),sQuery(id+"F9.wireOp",EDGE,"E0.top"),sQuery(id+"F9.wireOp",EDGE,"E0.left"),sQuery(id+"F9.wireOp",EDGE,"E0.right")])],"isStart":true}),"instanceName":"1"});
            var sketch = newSketch(context, id + "F68", { "sketchPlane" : qUnion([Q0])});
            skCircle(sketch, "E211.0", {"center": v(17.5, 46.5) * mm, "radius": 2.65 * mm, "construction": true});
            skCircle(sketch, "E212.cCircle", {"center": v(17.5, 46.5) * mm, "radius": 4.1 * mm, "construction": true});
            skLineSegment(sketch, "E212.0", {"start": v(14.15, 49.85) * mm, "end": v(18.73, 51.07) * mm});
            skLineSegment(sketch, "E212.1", {"start": v(18.73, 51.07) * mm, "end": v(22.07, 47.73) * mm});
            skLineSegment(sketch, "E212.2", {"start": v(22.07, 47.73) * mm, "end": v(20.85, 43.15) * mm});
            skLineSegment(sketch, "E212.3", {"start": v(20.85, 43.15) * mm, "end": v(16.27, 41.93) * mm});
            skLineSegment(sketch, "E212.4", {"start": v(16.27, 41.93) * mm, "end": v(12.93, 45.27) * mm});
            skLineSegment(sketch, "E212.5", {"start": v(12.93, 45.27) * mm, "end": v(14.15, 49.85) * mm});
            skPoint(sketch, "E212.0.midPoint", {"position": v(16.44, 50.46) * mm});
            skLineSegment(sketch, "E213", {"start": v(0, 53.5) * mm, "end": v(0, 0) * mm, "construction": true});
            skLineSegment(sketch, "E214", {"start": v(0, 0) * mm, "end": v(24.5, 0) * mm, "construction": true});
            skLineSegment(sketch, "E215.MirrorCS", {"start": v(-14.15, 49.85) * mm, "end": v(-18.73, 51.07) * mm});
            skLineSegment(sketch, "E216.MirrorCS", {"start": v(-22.07, 47.73) * mm, "end": v(-20.85, 43.15) * mm});
            skLineSegment(sketch, "E217.MirrorCS", {"start": v(-20.85, 43.15) * mm, "end": v(-16.27, 41.93) * mm});
            skLineSegment(sketch, "E218.MirrorCS", {"start": v(-16.27, 41.93) * mm, "end": v(-12.93, 45.27) * mm});
            skLineSegment(sketch, "E219.MirrorCS", {"start": v(-12.93, 45.27) * mm, "end": v(-14.15, 49.85) * mm});
            skCircle(sketch, "E220.MirrorC", {"center": v(-17.5, 46.5) * mm, "radius": 4.1 * mm, "construction": true});
            skCircle(sketch, "E221.MirrorC", {"center": v(-17.5, 46.5) * mm, "radius": 2.65 * mm, "construction": true});
            skLineSegment(sketch, "E222.MirrorCS", {"start": v(-18.73, 51.07) * mm, "end": v(-22.07, 47.73) * mm});
            skPoint(sketch, "E223.MirrorP", {"position": v(-16.44, 50.46) * mm});
            skLineSegment(sketch, "E224.MirrorCS", {"start": v(-14.15, -49.85) * mm, "end": v(-18.73, -51.07) * mm});
            skLineSegment(sketch, "E225.MirrorCS", {"start": v(14.15, -49.85) * mm, "end": v(18.73, -51.07) * mm});
            skLineSegment(sketch, "E226.MirrorCS", {"start": v(-20.85, -43.15) * mm, "end": v(-16.27, -41.93) * mm});
            skLineSegment(sketch, "E227.MirrorCS", {"start": v(-22.07, -47.73) * mm, "end": v(-20.85, -43.15) * mm});
            skLineSegment(sketch, "E228.MirrorCS", {"start": v(-18.73, -51.07) * mm, "end": v(-22.07, -47.73) * mm});
            skLineSegment(sketch, "E229.MirrorCS", {"start": v(18.73, -51.07) * mm, "end": v(22.07, -47.73) * mm});
            skCircle(sketch, "E230.MirrorC", {"center": v(17.5, -46.5) * mm, "radius": 2.65 * mm, "construction": true});
            skCircle(sketch, "E231.MirrorC", {"center": v(17.5, -46.5) * mm, "radius": 4.1 * mm, "construction": true});
            skCircle(sketch, "E232.MirrorC", {"center": v(-17.5, -46.5) * mm, "radius": 4.1 * mm, "construction": true});
            skLineSegment(sketch, "E233.MirrorCS", {"start": v(-16.27, -41.93) * mm, "end": v(-12.93, -45.27) * mm});
            skLineSegment(sketch, "E234.MirrorCS", {"start": v(12.93, -45.27) * mm, "end": v(14.15, -49.85) * mm});
            skLineSegment(sketch, "E235.MirrorCS", {"start": v(16.27, -41.93) * mm, "end": v(12.93, -45.27) * mm});
            skLineSegment(sketch, "E236.MirrorCS", {"start": v(22.07, -47.73) * mm, "end": v(20.85, -43.15) * mm});
            skLineSegment(sketch, "E237.MirrorCS", {"start": v(20.85, -43.15) * mm, "end": v(16.27, -41.93) * mm});
            skPoint(sketch, "E238.MirrorP", {"position": v(16.44, -50.46) * mm});
            skPoint(sketch, "E239.MirrorP", {"position": v(-16.44, -50.46) * mm});
            skLineSegment(sketch, "E240.MirrorCS", {"start": v(-12.93, -45.27) * mm, "end": v(-14.15, -49.85) * mm});
            skCircle(sketch, "E241.MirrorC", {"center": v(-17.5, -46.5) * mm, "radius": 2.65 * mm, "construction": true});
            skLineSegment(sketch, "E242", {"start": v(17.5, 46.5) * mm, "end": v(17.5, 53.5) * mm, "construction": true});
            skLineSegment(sketch, "E243", {"start": v(17.5, 46.5) * mm, "end": v(20.4, 49.4) * mm, "construction": true});
            skSolve(sketch);
        }
        {
            var Q0;
            Q0 = qSketchRegion(id + "F68", true);
            extrude(context, id + "F69", {"entities" : qUnion([Q0]), "operationType" : NewBodyOperationType.REMOVE, "endBound" : BoundingType.THROUGH_ALL, "oppositeDirection" : true, "depth" : 25 * mm});
        }
        {
            var Q0;
            Q0=makeQuery(id+"F19.opExtrude","CAP_FACE",FACE,{"disambiguationData":[OSD([sQuery(id+"F18.wireOp",EDGE,"E15"),sQuery(id+"F18.wireOp",EDGE,"E16"),sQuery(id+"F18.wireOp",EDGE,"E17.MirrorCS"),sQuery(id+"F18.wireOp",EDGE,"E18.MirrorCS"),sQuery(id+"F18.wireOp",EDGE,"E19")])],"isStart":false});
            var sketch = newSketch(context, id + "F70", { "sketchPlane" : qUnion([Q0])});
            skCircle(sketch, "E244.cCircle", {"center": v(36.5, 54.78) * mm, "radius": 2.85 * mm, "construction": true});
            skLineSegment(sketch, "E244.0", {"start": v(36.5, 58.07) * mm, "end": v(39.35, 56.42) * mm});
            skLineSegment(sketch, "E244.1", {"start": v(39.35, 56.42) * mm, "end": v(39.35, 53.13) * mm});
            skLineSegment(sketch, "E244.2", {"start": v(39.35, 53.13) * mm, "end": v(36.5, 51.48) * mm});
            skLineSegment(sketch, "E244.3", {"start": v(36.5, 51.48) * mm, "end": v(33.65, 53.13) * mm});
            skLineSegment(sketch, "E244.4", {"start": v(33.65, 53.13) * mm, "end": v(33.65, 56.42) * mm});
            skLineSegment(sketch, "E244.5", {"start": v(33.65, 56.42) * mm, "end": v(36.5, 58.07) * mm});
            skPoint(sketch, "E244.0.midPoint", {"position": v(37.93, 57.24) * mm});
            skCircle(sketch, "E245.0", {"center": v(-36.5, 54.78) * mm, "radius": 1.65 * mm, "construction": true});
            skCircle(sketch, "E245.1", {"center": v(36.5, -54.77) * mm, "radius": 1.65 * mm, "construction": true});
            skLineSegment(sketch, "E246", {"start": v(-36.5, 54.78) * mm, "end": v(36.5, -54.78) * mm, "construction": true});
            skLineSegment(sketch, "E247", {"start": v(0, 0) * mm, "end": v(0, 46.24) * mm, "construction": true});
            skLineSegment(sketch, "E248", {"start": v(0, 0) * mm, "end": v(20.95, 0) * mm, "construction": true});
            skLineSegment(sketch, "E249.MirrorCS", {"start": v(-36.5, 58.07) * mm, "end": v(-39.35, 56.42) * mm});
            skCircle(sketch, "E250.MirrorC", {"center": v(-36.5, 54.78) * mm, "radius": 2.85 * mm, "construction": true});
            skLineSegment(sketch, "E251.MirrorCS", {"start": v(-33.65, 53.13) * mm, "end": v(-33.65, 56.42) * mm});
            skLineSegment(sketch, "E252.MirrorCS", {"start": v(-36.5, 51.48) * mm, "end": v(-33.65, 53.13) * mm});
            skLineSegment(sketch, "E253.MirrorCS", {"start": v(-33.65, 56.42) * mm, "end": v(-36.5, 58.07) * mm});
            skLineSegment(sketch, "E254.MirrorCS", {"start": v(-39.35, 56.42) * mm, "end": v(-39.35, 53.13) * mm});
            skPoint(sketch, "E255.MirrorP", {"position": v(-37.93, 57.24) * mm});
            skLineSegment(sketch, "E256.MirrorCS", {"start": v(-39.35, 53.13) * mm, "end": v(-36.5, 51.48) * mm});
            skLineSegment(sketch, "E257.MirrorCS", {"start": v(39.35, -53.13) * mm, "end": v(36.5, -51.48) * mm});
            skLineSegment(sketch, "E258.MirrorCS", {"start": v(39.35, -56.42) * mm, "end": v(39.35, -53.13) * mm});
            skPoint(sketch, "E259.MirrorP", {"position": v(37.93, -57.24) * mm});
            skCircle(sketch, "E260.MirrorC", {"center": v(36.5, -54.77) * mm, "radius": 2.85 * mm, "construction": true});
            skLineSegment(sketch, "E261.MirrorCS", {"start": v(36.5, -58.07) * mm, "end": v(39.35, -56.42) * mm});
            skLineSegment(sketch, "E262.MirrorCS", {"start": v(33.65, -56.42) * mm, "end": v(36.5, -58.07) * mm});
            skLineSegment(sketch, "E263.MirrorCS", {"start": v(36.5, -51.48) * mm, "end": v(33.65, -53.13) * mm});
            skLineSegment(sketch, "E264.MirrorCS", {"start": v(33.65, -53.13) * mm, "end": v(33.65, -56.42) * mm});
            skLineSegment(sketch, "E265.MirrorCS", {"start": v(-39.35, -56.42) * mm, "end": v(-39.35, -53.13) * mm});
            skLineSegment(sketch, "E266.MirrorCS", {"start": v(-39.35, -53.13) * mm, "end": v(-36.5, -51.48) * mm});
            skLineSegment(sketch, "E267.MirrorCS", {"start": v(-36.5, -58.07) * mm, "end": v(-39.35, -56.42) * mm});
            skLineSegment(sketch, "E268.MirrorCS", {"start": v(-33.65, -53.13) * mm, "end": v(-33.65, -56.42) * mm});
            skPoint(sketch, "E269.MirrorP", {"position": v(-37.93, -57.24) * mm});
            skCircle(sketch, "E270.MirrorC", {"center": v(-36.5, -54.77) * mm, "radius": 2.85 * mm, "construction": true});
            skLineSegment(sketch, "E271.MirrorCS", {"start": v(-36.5, -51.48) * mm, "end": v(-33.65, -53.13) * mm});
            skLineSegment(sketch, "E272.MirrorCS", {"start": v(-33.65, -56.42) * mm, "end": v(-36.5, -58.07) * mm});
            skCircle(sketch, "E273.MirrorC", {"center": v(-36.5, -54.77) * mm, "radius": 1.65 * mm, "construction": true});
            skSolve(sketch);
        }
        {
            var Q0;
            Q0 = qSketchRegion(id + "F70", true);
            extrude(context, id + "F71", {"entities" : qUnion([Q0]), "operationType" : NewBodyOperationType.REMOVE, "oppositeDirection" : true, "depth" : (getVariable(context, 'M3_HEX_HEIGHT')) * mm});
        }
        {
            var Q0;
            Q0=makeQuery(id+"F50.opPattern","COPY",FACE,{"derivedFrom":makeQuery(id+"F19.opExtrude","CAP_FACE",FACE,{"disambiguationData":[OSD([sQuery(id+"F18.wireOp",EDGE,"E15"),sQuery(id+"F18.wireOp",EDGE,"E16"),sQuery(id+"F18.wireOp",EDGE,"E17.MirrorCS"),sQuery(id+"F18.wireOp",EDGE,"E18.MirrorCS"),sQuery(id+"F18.wireOp",EDGE,"E19")])],"isStart":false}),"instanceName":"1"});
            var sketch = newSketch(context, id + "F72", { "sketchPlane" : qUnion([Q0])});
            skCircle(sketch, "E274", {"center": v(36.5, -54.78) * mm, "radius": 2.85 * mm});
            skCircle(sketch, "E275.0", {"center": v(36.5, 54.77) * mm, "radius": 1.65 * mm, "construction": true});
            skCircle(sketch, "E275.1", {"center": v(-36.5, -54.78) * mm, "radius": 1.65 * mm, "construction": true});
            skLineSegment(sketch, "E276", {"start": v(36.5, 54.78) * mm, "end": v(-36.5, -54.78) * mm, "construction": true});
            skLineSegment(sketch, "E277", {"start": v(0, 0) * mm, "end": v(50.94, 0) * mm, "construction": true});
            skLineSegment(sketch, "E278", {"start": v(0, 0) * mm, "end": v(0, -37.98) * mm, "construction": true});
            skCircle(sketch, "E279.MirrorC", {"center": v(36.5, 54.78) * mm, "radius": 2.85 * mm});
            skCircle(sketch, "E280.MirrorC", {"center": v(-36.5, 54.78) * mm, "radius": 2.85 * mm});
            skCircle(sketch, "E281.MirrorC", {"center": v(-36.5, -54.78) * mm, "radius": 2.85 * mm});
            skSolve(sketch);
        }
        {
            var Q0;
            Q0 = qSketchRegion(id + "F72", true);
            extrude(context, id + "F73", {"entities" : qUnion([Q0]), "operationType" : NewBodyOperationType.REMOVE, "oppositeDirection" : true, "depth" : (getVariable(context, 'M3_SOCKET_HEAD_HEIGHT')) * mm});
        }
        {
            var Q0;
            Q0=makeQuery(id+"F10.opExtrude","CAP_EDGE",EDGE,{"disambiguationData":[OSD([sQuery(id+"F9.wireOp",EDGE,"E0.left")])],"isStart":true});
            var Q1;
            Q1=makeQuery(id+"F10.opExtrude","CAP_EDGE",EDGE,{"disambiguationData":[OSD([sQuery(id+"F9.wireOp",EDGE,"E0.right")])],"isStart":true});
            var Q2;
            Q2=makeQuery(id+"F10.opExtrude","CAP_EDGE",EDGE,{"disambiguationData":[OSD([sQuery(id+"F9.wireOp",EDGE,"E0.bottom")])],"isStart":true});
            var Q3;
            Q3=makeQuery(id+"F50.opPattern","COPY",EDGE,{"derivedFrom":makeQuery(id+"F10.opExtrude","CAP_EDGE",EDGE,{"disambiguationData":[OSD([sQuery(id+"F9.wireOp",EDGE,"E0.left")])],"isStart":true}),"instanceName":"1"});
            var Q4;
            Q4=makeQuery(id+"F50.opPattern","COPY",EDGE,{"derivedFrom":makeQuery(id+"F10.opExtrude","CAP_EDGE",EDGE,{"disambiguationData":[OSD([sQuery(id+"F9.wireOp",EDGE,"E0.right")])],"isStart":true}),"instanceName":"1"});
            var Q5;
            Q5=makeQuery(id+"F50.opPattern","COPY",EDGE,{"derivedFrom":makeQuery(id+"F10.opExtrude","CAP_EDGE",EDGE,{"disambiguationData":[OSD([sQuery(id+"F9.wireOp",EDGE,"E0.bottom")])],"isStart":true}),"instanceName":"1"});
            var Q6;
            Q6=makeQuery(id+"F67.opExtrude","CAP_EDGE",EDGE,{"disambiguationData":[OSD([sQuery(id+"F66.wireOp",EDGE,"E210.bottom")])],"isStart":false});
            var Q7;
            Q7=makeQuery(id+"F67.opExtrude","CAP_EDGE",EDGE,{"disambiguationData":[OSD([sQuery(id+"F66.wireOp",EDGE,"E210.left")])],"isStart":false});
            var Q8;
            Q8=makeQuery(id+"F67.opExtrude","CAP_EDGE",EDGE,{"disambiguationData":[OSD([sQuery(id+"F66.wireOp",EDGE,"E210.top")])],"isStart":false});
            var Q9;
            Q9=makeQuery(id+"F67.opExtrude","CAP_EDGE",EDGE,{"disambiguationData":[OSD([sQuery(id+"F66.wireOp",EDGE,"E210.right")])],"isStart":false});
            var Q10;
            Q10=makeQuery(id+"F52.opExtrude","CAP_EDGE",EDGE,{"disambiguationData":[OSD([sQuery(id+"F51.wireOp",EDGE,"E162.right")])],"isStart":false});
            var Q11;
            Q11=makeQuery(id+"F52.opExtrude","CAP_EDGE",EDGE,{"disambiguationData":[OSD([sQuery(id+"F51.wireOp",EDGE,"E162.top")])],"isStart":false});
            var Q12;
            Q12=makeQuery(id+"F52.opExtrude","CAP_EDGE",EDGE,{"disambiguationData":[OSD([sQuery(id+"F51.wireOp",EDGE,"E162.left")])],"isStart":false});
            var Q13;
            Q13=makeQuery(id+"F52.opExtrude","CAP_EDGE",EDGE,{"disambiguationData":[OSD([sQuery(id+"F51.wireOp",EDGE,"E162.bottom")])],"isStart":false});
            var Q14;
            Q14=makeQuery(id+"F19.opExtrude","SWEPT_EDGE",EDGE,{"disambiguationData":[OSD([sQuery(id+"F9.wireOp",EDGE,"E0.left"),sQuery(id+"F18.wireOp",EDGE,"E28.MirrorCS"),sQuery(id+"F18.wireOp",EDGE,"E31.MirrorCS")])]});
            var Q15;
            Q15=makeQuery(id+"F50.opPattern","COPY",EDGE,{"derivedFrom":makeQuery(id+"F19.opExtrude","SWEPT_EDGE",EDGE,{"disambiguationData":[OSD([sQuery(id+"F9.wireOp",EDGE,"E0.left"),sQuery(id+"F18.wireOp",EDGE,"E28.MirrorCS"),sQuery(id+"F18.wireOp",EDGE,"E31.MirrorCS")])]}),"instanceName":"1"});
            var Q16;
            Q16=makeQuery(id+"F19.opExtrude","SWEPT_EDGE",EDGE,{"disambiguationData":[OSD([sQuery(id+"F9.wireOp",EDGE,"E0.left"),sQuery(id+"F18.wireOp",EDGE,"E15"),sQuery(id+"F18.wireOp",EDGE,"E16")])]});
            var Q17;
            Q17=makeQuery(id+"F50.opPattern","COPY",EDGE,{"derivedFrom":makeQuery(id+"F19.opExtrude","SWEPT_EDGE",EDGE,{"disambiguationData":[OSD([sQuery(id+"F9.wireOp",EDGE,"E0.left"),sQuery(id+"F18.wireOp",EDGE,"E15"),sQuery(id+"F18.wireOp",EDGE,"E16")])]}),"instanceName":"1"});
            var Q18;
            Q18=makeQuery(id+"F19.opExtrude","SWEPT_EDGE",EDGE,{"disambiguationData":[OSD([sQuery(id+"F18.wireOp",EDGE,"E21.MirrorCS"),sQuery(id+"F18.wireOp",EDGE,"E23.MirrorCS")])]});
            var Q19;
            Q19=makeQuery(id+"F50.opPattern","COPY",EDGE,{"derivedFrom":makeQuery(id+"F19.opExtrude","SWEPT_EDGE",EDGE,{"disambiguationData":[OSD([sQuery(id+"F18.wireOp",EDGE,"E21.MirrorCS"),sQuery(id+"F18.wireOp",EDGE,"E23.MirrorCS")])]}),"instanceName":"1"});
            var Q20;
            Q20=makeQuery(id+"F19.opExtrude","SWEPT_EDGE",EDGE,{"disambiguationData":[OSD([sQuery(id+"F18.wireOp",EDGE,"E39.MirrorCS"),sQuery(id+"F18.wireOp",EDGE,"E40.MirrorCS")])]});
            var Q21;
            Q21=makeQuery(id+"F50.opPattern","COPY",EDGE,{"derivedFrom":makeQuery(id+"F19.opExtrude","SWEPT_EDGE",EDGE,{"disambiguationData":[OSD([sQuery(id+"F18.wireOp",EDGE,"E39.MirrorCS"),sQuery(id+"F18.wireOp",EDGE,"E40.MirrorCS")])]}),"instanceName":"1"});
            var Q22;
            Q22=makeQuery(id+"F58.opExtrude","SWEPT_EDGE",EDGE,{"disambiguationData":[OSD([sQuery(id+"F57.wireOp",EDGE,"E191.bottom"),sQuery(id+"F57.wireOp",EDGE,"E191.right")])]});
            var Q23;
            Q23=makeQuery(id+"F58.opExtrude","SWEPT_EDGE",EDGE,{"disambiguationData":[OSD([sQuery(id+"F57.wireOp",EDGE,"E191.bottom"),sQuery(id+"F57.wireOp",EDGE,"E191.left")])]});
            var Q24;
            Q24=makeQuery(id+"F58.opExtrude","SWEPT_EDGE",EDGE,{"disambiguationData":[OSD([sQuery(id+"F9.wireOp",EDGE,"E0.top"),sQuery(id+"F57.wireOp",EDGE,"E191.left")])]});
            var Q25;
            Q25=makeQuery(id+"F58.opExtrude","SWEPT_EDGE",EDGE,{"disambiguationData":[OSD([sQuery(id+"F9.wireOp",EDGE,"E0.top"),sQuery(id+"F57.wireOp",EDGE,"E191.right")])]});
            var Q26;
            Q26=makeQuery(id+"F58.opExtrude","CAP_EDGE",EDGE,{"disambiguationData":[OSD([sQuery(id+"F9.wireOp",EDGE,"E0.top")])],"isStart":false});
            var Q27;
            Q27=makeQuery(id+"F58.opExtrude","CAP_EDGE",EDGE,{"disambiguationData":[OSD([sQuery(id+"F57.wireOp",EDGE,"E191.right")])],"isStart":false});
            var Q28;
            Q28=makeQuery(id+"F58.opExtrude","CAP_EDGE",EDGE,{"disambiguationData":[OSD([sQuery(id+"F57.wireOp",EDGE,"E191.bottom")])],"isStart":false});
            var Q29;
            Q29=makeQuery(id+"F58.opExtrude","CAP_EDGE",EDGE,{"disambiguationData":[OSD([sQuery(id+"F57.wireOp",EDGE,"E191.left")])],"isStart":false});
            fillet(context, id + "F74", {"entities" : qUnion([Q0, Q1, Q2, Q3, Q4, Q5, Q6, Q7, Q8, Q9, Q10, Q11, Q12, Q13, Q14, Q15, Q16, Q17, Q18, Q19, Q20, Q21, Q22, Q23, Q24, Q25, Q26, Q27, Q28, Q29]), "radius" : 1 * mm, "tangentPropagation" : true, "allowEdgeOverflow" : false});
        }
        {
            var Q0;
            Q0=makeQuery(id+"F50.opPattern","COPY",FACE,{"derivedFrom":makeQuery(id+"F10.opExtrude","SWEPT_FACE",FACE,{"disambiguationData":[OSD([sQuery(id+"F9.wireOp",EDGE,"E0.left")])]}),"instanceName":"1"});
            var sketch = newSketch(context, id + "F75", { "sketchPlane" : qUnion([Q0])});
            skLineSegment(sketch, "E282", {"start": v(-34.5, 32.4) * mm, "end": v(34.5, 32.4) * mm, "construction": true});
            skLineSegment(sketch, "E283", {"start": v(0, 32.4) * mm, "end": v(0, 89.59) * mm, "construction": true});
            skPoint(sketch, "E283.endSnap0", {"position": v(0, 32.4) * mm});
            skLineSegment(sketch, "E284", {"start": v(0, 67.3) * mm, "end": v(-80.08, 67.3) * mm});
            skLineSegment(sketch, "E285", {"start": v(-80.08, 67.3) * mm, "end": v(-80.08, 48.4) * mm});
            skLineSegment(sketch, "E286", {"start": v(-80.08, 48.4) * mm, "end": v(-42.48, 48.4) * mm});
            skLineSegment(sketch, "E287", {"start": v(-42.48, 48.4) * mm, "end": v(-42.48, 16.4) * mm});
            skLineSegment(sketch, "E288", {"start": v(-42.48, 16.4) * mm, "end": v(-80.07, 16.4) * mm});
            skLineSegment(sketch, "E289", {"start": v(-80.07, 16.4) * mm, "end": v(-80.07, -16) * mm});
            skLineSegment(sketch, "E290", {"start": v(-80.07, -16) * mm, "end": v(-42.48, -16) * mm});
            skLineSegment(sketch, "E291", {"start": v(-42.48, -16) * mm, "end": v(-14.76, 0) * mm});
            skLineSegment(sketch, "E292", {"start": v(-14.76, 0) * mm, "end": v(0, 0) * mm});
            skLineSegment(sketch, "E293.0", {"start": v(-49.48, 22.4) * mm, "end": v(-60.08, 22.4) * mm, "construction": true});
            skLineSegment(sketch, "E294.0", {"start": v(-52.5, 0) * mm, "end": v(52.5, 0) * mm, "construction": true});
            skLineSegment(sketch, "E295.0", {"start": v(53.5, 66.3) * mm, "end": v(-53.5, 66.3) * mm, "construction": true});
            skLineSegment(sketch, "E296.MirrorCS", {"start": v(0, 67.3) * mm, "end": v(80.07, 67.3) * mm});
            skLineSegment(sketch, "E297.MirrorCS", {"start": v(80.07, 67.3) * mm, "end": v(80.07, 48.4) * mm});
            skLineSegment(sketch, "E298.MirrorCS", {"start": v(80.07, 48.4) * mm, "end": v(42.47, 48.4) * mm});
            skLineSegment(sketch, "E299.MirrorCS", {"start": v(42.47, 48.4) * mm, "end": v(42.47, 16.4) * mm});
            skLineSegment(sketch, "E300.MirrorCS", {"start": v(42.47, 16.4) * mm, "end": v(80.07, 16.4) * mm});
            skLineSegment(sketch, "E301.MirrorCS", {"start": v(80.07, 16.4) * mm, "end": v(80.07, -16) * mm});
            skLineSegment(sketch, "E302.MirrorCS", {"start": v(80.07, -16) * mm, "end": v(42.47, -16) * mm});
            skLineSegment(sketch, "E303.MirrorCS", {"start": v(42.47, -16) * mm, "end": v(14.76, 0) * mm});
            skLineSegment(sketch, "E304.MirrorCS", {"start": v(14.76, 0) * mm, "end": v(0, 0) * mm});
            skLineSegment(sketch, "E305", {"start": v(0, 32.4) * mm, "end": v(0, 32.2) * mm, "construction": true});
            skLineSegment(sketch, "E306", {"start": v(0, 32.2) * mm, "end": v(14.3, 32.2) * mm, "construction": true});
            skCircle(sketch, "E307.0", {"center": v(35, 60.07) * mm, "radius": 3 * mm});
            skCircle(sketch, "E307.1", {"center": v(-35, 60.07) * mm, "radius": 3 * mm});
            skCircle(sketch, "E308.MirrorC", {"center": v(-35, 4.33) * mm, "radius": 3 * mm});
            skCircle(sketch, "E309.MirrorC", {"center": v(35, 4.33) * mm, "radius": 3 * mm});
            skSolve(sketch);
        }
        {
            var Q0;
            Q0 = qSketchRegion(id + "F75", true);
            extrude(context, id + "F76", {"entities" : qUnion([Q0]), "depth" : 50 * mm});
        }
        {
            var Q0;
            Q0=makeQuery(id+"F76.opExtrude","CAP_FACE",FACE,{"disambiguationData":[OSD([sQuery(id+"F75.wireOp",EDGE,"E284"),sQuery(id+"F75.wireOp",EDGE,"E285"),sQuery(id+"F75.wireOp",EDGE,"E286"),sQuery(id+"F75.wireOp",EDGE,"E287"),sQuery(id+"F75.wireOp",EDGE,"E288"),sQuery(id+"F75.wireOp",EDGE,"E289"),sQuery(id+"F75.wireOp",EDGE,"E290"),sQuery(id+"F75.wireOp",EDGE,"E291"),sQuery(id+"F75.wireOp",EDGE,"E292"),sQuery(id+"F75.wireOp",EDGE,"E296.MirrorCS"),sQuery(id+"F75.wireOp",EDGE,"E297.MirrorCS"),sQuery(id+"F75.wireOp",EDGE,"E298.MirrorCS"),sQuery(id+"F75.wireOp",EDGE,"E299.MirrorCS"),sQuery(id+"F75.wireOp",EDGE,"E300.MirrorCS"),sQuery(id+"F75.wireOp",EDGE,"E301.MirrorCS"),sQuery(id+"F75.wireOp",EDGE,"E302.MirrorCS"),sQuery(id+"F75.wireOp",EDGE,"E303.MirrorCS"),sQuery(id+"F75.wireOp",EDGE,"E304.MirrorCS"),sQuery(id+"F75.wireOp",EDGE,"E307.0"),sQuery(id+"F75.wireOp",EDGE,"E307.1"),sQuery(id+"F75.wireOp",EDGE,"E308.MirrorC"),sQuery(id+"F75.wireOp",EDGE,"E309.MirrorC")])],"isStart":true});
            var sketch = newSketch(context, id + "F77", { "sketchPlane" : qUnion([Q0])});
            skLineSegment(sketch, "E310", {"start": v(70.08, 48.4) * mm, "end": v(70.08, 57.3) * mm});
            skLineSegment(sketch, "E311", {"start": v(70.08, 57.3) * mm, "end": v(55.08, 57.3) * mm});
            skLineSegment(sketch, "E312", {"start": v(55.08, 57.3) * mm, "end": v(55.08, 67.3) * mm});
            skLineSegment(sketch, "E313", {"start": v(55.08, 67.3) * mm, "end": v(80.08, 67.3) * mm});
            skLineSegment(sketch, "E314", {"start": v(80.08, 67.3) * mm, "end": v(80.08, 48.4) * mm});
            skLineSegment(sketch, "E315", {"start": v(80.08, 48.4) * mm, "end": v(70.08, 48.4) * mm});
            skLineSegment(sketch, "E316", {"start": v(70.08, 16.4) * mm, "end": v(70.08, -6) * mm});
            skLineSegment(sketch, "E317", {"start": v(70.08, -6) * mm, "end": v(55.08, -6) * mm});
            skLineSegment(sketch, "E318", {"start": v(55.08, -6) * mm, "end": v(55.08, -16) * mm});
            skLineSegment(sketch, "E319", {"start": v(0, 67.3) * mm, "end": v(0, 0) * mm, "construction": true});
            skLineSegment(sketch, "E320.MirrorCS", {"start": v(-70.08, 57.3) * mm, "end": v(-55.08, 57.3) * mm});
            skLineSegment(sketch, "E321.MirrorCS", {"start": v(-55.08, 57.3) * mm, "end": v(-55.08, 67.3) * mm});
            skLineSegment(sketch, "E322.MirrorCS", {"start": v(-80.08, 48.4) * mm, "end": v(-70.08, 48.4) * mm});
            skLineSegment(sketch, "E323.MirrorCS", {"start": v(-70.08, 48.4) * mm, "end": v(-70.08, 57.3) * mm});
            skLineSegment(sketch, "E324.MirrorCS", {"start": v(-55.08, 67.3) * mm, "end": v(-80.07, 67.3) * mm});
            skLineSegment(sketch, "E325.MirrorCS", {"start": v(-80.08, 67.3) * mm, "end": v(-80.08, 48.4) * mm});
            skLineSegment(sketch, "E326", {"start": v(70.08, 16.4) * mm, "end": v(80.07, 16.4) * mm, "construction": true});
            skLineSegment(sketch, "E327", {"start": v(80.07, -16) * mm, "end": v(55.08, -16) * mm});
            skLineSegment(sketch, "E328.MirrorCS", {"start": v(-80.07, -16) * mm, "end": v(-55.07, -16) * mm});
            skLineSegment(sketch, "E329.MirrorCS", {"start": v(-70.08, -6) * mm, "end": v(-55.07, -6) * mm});
            skLineSegment(sketch, "E330.MirrorCS", {"start": v(-55.07, -6) * mm, "end": v(-55.07, -16) * mm});
            skLineSegment(sketch, "E331.MirrorCS", {"start": v(-70.07, 16.4) * mm, "end": v(-70.07, -6) * mm});
            skLineSegment(sketch, "E332.MirrorCS", {"start": v(-70.08, 16.4) * mm, "end": v(-80.07, 16.4) * mm, "construction": true});
            skLineSegment(sketch, "E333", {"start": v(80.08, 16.4) * mm, "end": v(80.08, -16) * mm});
            skLineSegment(sketch, "E334", {"start": v(-80.07, 16.4) * mm, "end": v(-80.07, -16) * mm});
            skSolve(sketch);
        }
        {
            var Q0;
            Q0=makeQuery(id+"F77.imprint","IMPRINT",FACE,{"disambiguationData":[TD([[makeQuery(id+"F77.imprint","IMPRINT",EDGE,{"derivedFrom":sQuery(id+"F77.wireOp",EDGE,"E328.MirrorCS")}),1.0]])]});
            var Q1;
            {var subQ0=sQuery(id+"F77.wireOp",EDGE,"E316");Q1=makeQuery(id+"F77.imprint","IMPRINT",FACE,{"disambiguationData":[TD([[makeQuery(id+"F77.imprint","IMPRINT",EDGE,{"derivedFrom":subQ0}),1.0]])]});}
            extrude(context, id + "F78", {"entities" : qUnion([Q0, Q1]), "operationType" : NewBodyOperationType.ADD, "depth" : 10 * mm});
        }
        {
            var Q0;
            Q0=makeQuery(id+"F50.opPattern","COPY",FACE,{"derivedFrom":makeQuery(id+"F37.opExtrude","SWEPT_FACE",FACE,{"disambiguationData":[OSD([sQuery(id+"F36.wireOp",EDGE,"E86")])]}),"instanceName":"1"});
            cPlane(context, id + "F79", {"entities" : qUnion([Q0]), "cplaneType" : CPlaneType.OFFSET, "offset" : 25 * mm, "oppositeDirection" : true, "width" : 150 * mm, "height" : 150 * mm});
        }
        {
            var Q0;
            Q0=qCreatedBy(id+"F79.planeOp",FACE);
            var sketch = newSketch(context, id + "F80", { "sketchPlane" : qUnion([Q0])});
            skLineSegment(sketch, "E335.0", {"start": v(-80.07, 48.4) * mm, "end": v(-42.47, 48.4) * mm});
            skLineSegment(sketch, "E335.1", {"start": v(-42.47, 48.4) * mm, "end": v(-42.47, 16.4) * mm});
            skLineSegment(sketch, "E335.2", {"start": v(-42.47, 16.4) * mm, "end": v(-80.07, 16.4) * mm});
            skLineSegment(sketch, "E336", {"start": v(-80.07, 48.4) * mm, "end": v(-80.07, 16.4) * mm});
            skCircle(sketch, "E337.0", {"center": v(-35, 60.07) * mm, "radius": 3 * mm, "construction": true});
            skCircle(sketch, "E337.1", {"center": v(35, 60.07) * mm, "radius": 3 * mm, "construction": true});
            skLineSegment(sketch, "E338", {"start": v(-35, 60.07) * mm, "end": v(35, 60.07) * mm, "construction": true});
            skLineSegment(sketch, "E339", {"start": v(0, 60.07) * mm, "end": v(0, 0) * mm, "construction": true});
            skLineSegment(sketch, "E340.MirrorCS", {"start": v(80.07, 48.4) * mm, "end": v(42.47, 48.4) * mm});
            skLineSegment(sketch, "E341.MirrorCS", {"start": v(80.07, 48.4) * mm, "end": v(80.07, 16.4) * mm});
            skLineSegment(sketch, "E342.MirrorCS", {"start": v(42.47, 16.4) * mm, "end": v(80.07, 16.4) * mm});
            skLineSegment(sketch, "E343.MirrorCS", {"start": v(42.47, 48.4) * mm, "end": v(42.47, 16.4) * mm});
            skSolve(sketch);
        }
        {
            var Q0;
            Q0=makeQuery(id+"F80.imprint","IMPRINT",FACE,{"disambiguationData":[TD([[makeQuery(id+"F80.imprint","IMPRINT",EDGE,{"derivedFrom":sQuery(id+"F80.wireOp",EDGE,"E340.MirrorCS")}),1.0]])]});
            var Q1;
            Q1=makeQuery(id+"F80.imprint","IMPRINT",FACE,{"disambiguationData":[TD([[makeQuery(id+"F80.imprint","IMPRINT",EDGE,{"derivedFrom":sQuery(id+"F80.wireOp",EDGE,"E335.0")}),-1.0]])]});
            var Q2;
            Q2=makeQuery(id+"F76.opExtrude","CAP_FACE",FACE,{"disambiguationData":[OSD([sQuery(id+"F75.wireOp",EDGE,"E284"),sQuery(id+"F75.wireOp",EDGE,"E285"),sQuery(id+"F75.wireOp",EDGE,"E286"),sQuery(id+"F75.wireOp",EDGE,"E287"),sQuery(id+"F75.wireOp",EDGE,"E288"),sQuery(id+"F75.wireOp",EDGE,"E289"),sQuery(id+"F75.wireOp",EDGE,"E290"),sQuery(id+"F75.wireOp",EDGE,"E291"),sQuery(id+"F75.wireOp",EDGE,"E292"),sQuery(id+"F75.wireOp",EDGE,"E296.MirrorCS"),sQuery(id+"F75.wireOp",EDGE,"E297.MirrorCS"),sQuery(id+"F75.wireOp",EDGE,"E298.MirrorCS"),sQuery(id+"F75.wireOp",EDGE,"E299.MirrorCS"),sQuery(id+"F75.wireOp",EDGE,"E300.MirrorCS"),sQuery(id+"F75.wireOp",EDGE,"E301.MirrorCS"),sQuery(id+"F75.wireOp",EDGE,"E302.MirrorCS"),sQuery(id+"F75.wireOp",EDGE,"E303.MirrorCS"),sQuery(id+"F75.wireOp",EDGE,"E304.MirrorCS"),sQuery(id+"F75.wireOp",EDGE,"E307.0"),sQuery(id+"F75.wireOp",EDGE,"E307.1"),sQuery(id+"F75.wireOp",EDGE,"E308.MirrorC"),sQuery(id+"F75.wireOp",EDGE,"E309.MirrorC")])],"isStart":false});
            extrude(context, id + "F81", {"entities" : qUnion([Q0, Q1]), "operationType" : NewBodyOperationType.ADD, "endBound" : BoundingType.UP_TO_SURFACE, "oppositeDirection" : true, "endBoundEntityFace" : qUnion([Q2]), "depth" : 25 * mm});
        }
        {
            var Q0;
            Q0=makeQuery(id+"F81.boolean.opBoolean","MERGE",FACE,{"derivedFrom":[makeQuery(id+"F76.opExtrude","CAP_FACE",FACE,{"disambiguationData":[OSD([sQuery(id+"F75.wireOp",EDGE,"E284"),sQuery(id+"F75.wireOp",EDGE,"E285"),sQuery(id+"F75.wireOp",EDGE,"E286"),sQuery(id+"F75.wireOp",EDGE,"E287"),sQuery(id+"F75.wireOp",EDGE,"E288"),sQuery(id+"F75.wireOp",EDGE,"E289"),sQuery(id+"F75.wireOp",EDGE,"E290"),sQuery(id+"F75.wireOp",EDGE,"E291"),sQuery(id+"F75.wireOp",EDGE,"E292"),sQuery(id+"F75.wireOp",EDGE,"E296.MirrorCS"),sQuery(id+"F75.wireOp",EDGE,"E297.MirrorCS"),sQuery(id+"F75.wireOp",EDGE,"E298.MirrorCS"),sQuery(id+"F75.wireOp",EDGE,"E299.MirrorCS"),sQuery(id+"F75.wireOp",EDGE,"E300.MirrorCS"),sQuery(id+"F75.wireOp",EDGE,"E301.MirrorCS"),sQuery(id+"F75.wireOp",EDGE,"E302.MirrorCS"),sQuery(id+"F75.wireOp",EDGE,"E303.MirrorCS"),sQuery(id+"F75.wireOp",EDGE,"E304.MirrorCS"),sQuery(id+"F75.wireOp",EDGE,"E307.0"),sQuery(id+"F75.wireOp",EDGE,"E307.1"),sQuery(id+"F75.wireOp",EDGE,"E308.MirrorC"),sQuery(id+"F75.wireOp",EDGE,"E309.MirrorC")])],"isStart":false}),makeQuery(id+"F81.opExtrude","CAP_FACE",FACE,{"disambiguationData":[OSD([sQuery(id+"F80.wireOp",EDGE,"E335.0"),sQuery(id+"F80.wireOp",EDGE,"E335.1"),sQuery(id+"F80.wireOp",EDGE,"E335.2"),sQuery(id+"F80.wireOp",EDGE,"E336")])],"isStart":false}),makeQuery(id+"F81.opExtrude","CAP_FACE",FACE,{"disambiguationData":[OSD([sQuery(id+"F80.wireOp",EDGE,"E340.MirrorCS"),sQuery(id+"F80.wireOp",EDGE,"E341.MirrorCS"),sQuery(id+"F80.wireOp",EDGE,"E342.MirrorCS"),sQuery(id+"F80.wireOp",EDGE,"E343.MirrorCS")])],"isStart":false})]});
            var sketch = newSketch(context, id + "F82", { "sketchPlane" : qUnion([Q0])});
            skLineSegment(sketch, "E344", {"start": v(0, 0) * mm, "end": v(0, 15) * mm, "construction": true});
            skEllipse(sketch, "E345", {"center": v(0, 15) * mm, "majorRadius": 80.08 * mm, "minorRadius": 81.98 * mm, "majorAxis": v(1, 0)});
            skLineSegment(sketch, "E346", {"start": v(80.08, 15) * mm, "end": v(0, 15) * mm, "construction": true});
            skLineSegment(sketch, "E347.bottom", {"start": v(80.07, 96.98) * mm, "end": v(-80.08, 96.98) * mm});
            skLineSegment(sketch, "E347.top", {"start": v(80.08, -66.98) * mm, "end": v(-80.07, -66.98) * mm});
            skLineSegment(sketch, "E347.left", {"start": v(80.08, 96.98) * mm, "end": v(80.08, -66.98) * mm});
            skLineSegment(sketch, "E347.right", {"start": v(-80.08, 96.98) * mm, "end": v(-80.08, -66.98) * mm});
            skSolve(sketch);
        }
        {
            var Q0;
            {var subQ0=sQuery(id+"F82.wireOp",EDGE,"E347.right");var subQ1=sQuery(id+"F82.wireOp",EDGE,"E345");var subQ2=makeQuery(id+"F82.imprint","INTERSECT",VERTEX,{"derivedFrom":[subQ1,subQ0]});Q0=makeQuery(id+"F82.imprint","IMPRINT",FACE,{"disambiguationData":[TD([[makeQuery(id+"F82.imprint","IMPRINT",EDGE,{"disambiguationData":[TD([[subQ2,1.0]])],"derivedFrom":subQ1}),-1.0]])]});}
            var Q1;
            {var subQ0=sQuery(id+"F82.wireOp",EDGE,"E347.left");var subQ1=sQuery(id+"F82.wireOp",EDGE,"E345");var subQ2=makeQuery(id+"F82.imprint","INTERSECT",VERTEX,{"derivedFrom":[subQ1,subQ0]});Q1=makeQuery(id+"F82.imprint","IMPRINT",FACE,{"disambiguationData":[TD([[makeQuery(id+"F82.imprint","IMPRINT",EDGE,{"disambiguationData":[TD([[subQ2,-1.0]])],"derivedFrom":subQ1}),-1.0]])]});}
            var Q2;
            {var subQ0=sQuery(id+"F82.wireOp",EDGE,"E347.left");var subQ1=sQuery(id+"F82.wireOp",EDGE,"E345");var subQ2=makeQuery(id+"F82.imprint","INTERSECT",VERTEX,{"derivedFrom":[subQ1,subQ0]});Q2=makeQuery(id+"F82.imprint","IMPRINT",FACE,{"disambiguationData":[TD([[makeQuery(id+"F82.imprint","IMPRINT",EDGE,{"disambiguationData":[TD([[subQ2,1.0]])],"derivedFrom":subQ1}),-1.0]])]});}
            var Q3;
            {var subQ0=sQuery(id+"F82.wireOp",EDGE,"E347.right");var subQ1=sQuery(id+"F82.wireOp",EDGE,"E345");var subQ2=makeQuery(id+"F82.imprint","INTERSECT",VERTEX,{"derivedFrom":[subQ1,subQ0]});Q3=makeQuery(id+"F82.imprint","IMPRINT",FACE,{"disambiguationData":[TD([[makeQuery(id+"F82.imprint","IMPRINT",EDGE,{"disambiguationData":[TD([[subQ2,-1.0]])],"derivedFrom":subQ1}),-1.0]])]});}
            extrude(context, id + "F83", {"entities" : qUnion([Q0, Q1, Q2, Q3]), "operationType" : NewBodyOperationType.REMOVE, "endBound" : BoundingType.THROUGH_ALL, "oppositeDirection" : true, "depth" : 25 * mm});
        }
        {
            var Q0;
            Q0=makeQuery(id+"F76.opExtrude","CAP_EDGE",EDGE,{"disambiguationData":[OSD([sQuery(id+"F75.wireOp",EDGE,"E284"),sQuery(id+"F75.wireOp",EDGE,"E296.MirrorCS")])],"isStart":false});
            var Q1;
            {var subQ0=sQuery(id+"F82.wireOp",EDGE,"E345");var subQ1=makeQuery(id+"F82.imprint","INTERSECT",VERTEX,{"derivedFrom":[subQ0,sQuery(id+"F82.wireOp",EDGE,"E347.right")]});Q1=makeQuery(id+"F83.boolean.opBoolean","TWEAK_EDGE",EDGE,{"derivedFrom":[makeQuery(id+"F83.opExtrude","CAP_EDGE",EDGE,{"disambiguationData":[OSD([subQ0]),TDD([makeQuery(id+"F82.imprint","IMPRINT",EDGE,{"disambiguationData":[TD([[subQ1,1.0]])],"derivedFrom":subQ0})])],"isStart":true}),makeQuery(id+"F83.opExtrude","CAP_EDGE",EDGE,{"disambiguationData":[OSD([subQ0]),TDD([makeQuery(id+"F82.imprint","IMPRINT",EDGE,{"disambiguationData":[TD([[subQ1,-1.0]])],"derivedFrom":subQ0})])],"isStart":true})]});}
            var Q2;
            Q2=makeQuery(id+"F76.opExtrude","CAP_EDGE",EDGE,{"disambiguationData":[OSD([sQuery(id+"F75.wireOp",EDGE,"E290")])],"isStart":false});
            var Q3;
            Q3=makeQuery(id+"F76.opExtrude","CAP_EDGE",EDGE,{"disambiguationData":[OSD([sQuery(id+"F75.wireOp",EDGE,"E291")])],"isStart":false});
            var Q4;
            Q4=makeQuery(id+"F76.opExtrude","CAP_EDGE",EDGE,{"disambiguationData":[OSD([sQuery(id+"F75.wireOp",EDGE,"E292"),sQuery(id+"F75.wireOp",EDGE,"E304.MirrorCS")])],"isStart":false});
            var Q5;
            Q5=makeQuery(id+"F76.opExtrude","CAP_EDGE",EDGE,{"disambiguationData":[OSD([sQuery(id+"F75.wireOp",EDGE,"E303.MirrorCS")])],"isStart":false});
            var Q6;
            {var subQ0=sQuery(id+"F82.wireOp",EDGE,"E345");var subQ1=makeQuery(id+"F82.imprint","INTERSECT",VERTEX,{"derivedFrom":[subQ0,sQuery(id+"F82.wireOp",EDGE,"E347.left")]});Q6=makeQuery(id+"F83.boolean.opBoolean","TWEAK_EDGE",EDGE,{"derivedFrom":[makeQuery(id+"F83.opExtrude","CAP_EDGE",EDGE,{"disambiguationData":[OSD([subQ0]),TDD([makeQuery(id+"F82.imprint","IMPRINT",EDGE,{"disambiguationData":[TD([[subQ1,1.0]])],"derivedFrom":subQ0})])],"isStart":true}),makeQuery(id+"F83.opExtrude","CAP_EDGE",EDGE,{"disambiguationData":[OSD([subQ0]),TDD([makeQuery(id+"F82.imprint","IMPRINT",EDGE,{"disambiguationData":[TD([[subQ1,-1.0]])],"derivedFrom":subQ0})])],"isStart":true})]});}
            var Q7;
            Q7=makeQuery(id+"F76.opExtrude","CAP_EDGE",EDGE,{"disambiguationData":[OSD([sQuery(id+"F75.wireOp",EDGE,"E302.MirrorCS")])],"isStart":false});
            chamfer(context, id + "F84", {"entities" : qUnion([Q0, Q1, Q2, Q3, Q4, Q5, Q6, Q7]), "chamferType" : ChamferType.OFFSET_ANGLE, "width" : 25 * mm, "oppositeDirection" : false, "angle" : 30 * degree, "tangentPropagation" : true});
        }
        {
            var Q0;
            {var subQ0=sQuery(id+"F75.wireOp",EDGE,"E296.MirrorCS");var subQ1=sQuery(id+"F75.wireOp",EDGE,"E284");Q0=makeQuery(id+"F84.opChamfer","BLEND_EDGE",EDGE,{"blendedFrom":[makeQuery(id+"F76.opExtrude","CAP_EDGE",EDGE,{"disambiguationData":[OSD([subQ1,subQ0])],"isStart":false}),makeQuery(id+"F81.boolean.opBoolean","MERGE",FACE,{"derivedFrom":[makeQuery(id+"F76.opExtrude","CAP_FACE",FACE,{"disambiguationData":[OSD([subQ1,sQuery(id+"F75.wireOp",EDGE,"E285"),sQuery(id+"F75.wireOp",EDGE,"E286"),sQuery(id+"F75.wireOp",EDGE,"E287"),sQuery(id+"F75.wireOp",EDGE,"E288"),sQuery(id+"F75.wireOp",EDGE,"E289"),sQuery(id+"F75.wireOp",EDGE,"E290"),sQuery(id+"F75.wireOp",EDGE,"E291"),sQuery(id+"F75.wireOp",EDGE,"E292"),subQ0,sQuery(id+"F75.wireOp",EDGE,"E297.MirrorCS"),sQuery(id+"F75.wireOp",EDGE,"E298.MirrorCS"),sQuery(id+"F75.wireOp",EDGE,"E299.MirrorCS"),sQuery(id+"F75.wireOp",EDGE,"E300.MirrorCS"),sQuery(id+"F75.wireOp",EDGE,"E301.MirrorCS"),sQuery(id+"F75.wireOp",EDGE,"E302.MirrorCS"),sQuery(id+"F75.wireOp",EDGE,"E303.MirrorCS"),sQuery(id+"F75.wireOp",EDGE,"E304.MirrorCS"),sQuery(id+"F75.wireOp",EDGE,"E307.0"),sQuery(id+"F75.wireOp",EDGE,"E307.1"),sQuery(id+"F75.wireOp",EDGE,"E308.MirrorC"),sQuery(id+"F75.wireOp",EDGE,"E309.MirrorC")])],"isStart":false}),makeQuery(id+"F81.opExtrude","CAP_FACE",FACE,{"disambiguationData":[OSD([sQuery(id+"F80.wireOp",EDGE,"E335.0"),sQuery(id+"F80.wireOp",EDGE,"E335.1"),sQuery(id+"F80.wireOp",EDGE,"E335.2"),sQuery(id+"F80.wireOp",EDGE,"E336")])],"isStart":false}),makeQuery(id+"F81.opExtrude","CAP_FACE",FACE,{"disambiguationData":[OSD([sQuery(id+"F80.wireOp",EDGE,"E340.MirrorCS"),sQuery(id+"F80.wireOp",EDGE,"E341.MirrorCS"),sQuery(id+"F80.wireOp",EDGE,"E342.MirrorCS"),sQuery(id+"F80.wireOp",EDGE,"E343.MirrorCS")])],"isStart":false})]})],"blendedInto":[makeQuery(id+"F81.boolean.opBoolean","MERGE",FACE,{"derivedFrom":[makeQuery(id+"F76.opExtrude","CAP_FACE",FACE,{"disambiguationData":[OSD([subQ1,sQuery(id+"F75.wireOp",EDGE,"E285"),sQuery(id+"F75.wireOp",EDGE,"E286"),sQuery(id+"F75.wireOp",EDGE,"E287"),sQuery(id+"F75.wireOp",EDGE,"E288"),sQuery(id+"F75.wireOp",EDGE,"E289"),sQuery(id+"F75.wireOp",EDGE,"E290"),sQuery(id+"F75.wireOp",EDGE,"E291"),sQuery(id+"F75.wireOp",EDGE,"E292"),subQ0,sQuery(id+"F75.wireOp",EDGE,"E297.MirrorCS"),sQuery(id+"F75.wireOp",EDGE,"E298.MirrorCS"),sQuery(id+"F75.wireOp",EDGE,"E299.MirrorCS"),sQuery(id+"F75.wireOp",EDGE,"E300.MirrorCS"),sQuery(id+"F75.wireOp",EDGE,"E301.MirrorCS"),sQuery(id+"F75.wireOp",EDGE,"E302.MirrorCS"),sQuery(id+"F75.wireOp",EDGE,"E303.MirrorCS"),sQuery(id+"F75.wireOp",EDGE,"E304.MirrorCS"),sQuery(id+"F75.wireOp",EDGE,"E307.0"),sQuery(id+"F75.wireOp",EDGE,"E307.1"),sQuery(id+"F75.wireOp",EDGE,"E308.MirrorC"),sQuery(id+"F75.wireOp",EDGE,"E309.MirrorC")])],"isStart":false}),makeQuery(id+"F81.opExtrude","CAP_FACE",FACE,{"disambiguationData":[OSD([sQuery(id+"F80.wireOp",EDGE,"E335.0"),sQuery(id+"F80.wireOp",EDGE,"E335.1"),sQuery(id+"F80.wireOp",EDGE,"E335.2"),sQuery(id+"F80.wireOp",EDGE,"E336")])],"isStart":false}),makeQuery(id+"F81.opExtrude","CAP_FACE",FACE,{"disambiguationData":[OSD([sQuery(id+"F80.wireOp",EDGE,"E340.MirrorCS"),sQuery(id+"F80.wireOp",EDGE,"E341.MirrorCS"),sQuery(id+"F80.wireOp",EDGE,"E342.MirrorCS"),sQuery(id+"F80.wireOp",EDGE,"E343.MirrorCS")])],"isStart":false})]})]});}
            var Q1;
            {var subQ0=sQuery(id+"F75.wireOp",EDGE,"E296.MirrorCS");var subQ1=sQuery(id+"F75.wireOp",EDGE,"E290");var subQ2=sQuery(id+"F75.wireOp",EDGE,"E284");var subQ3=sQuery(id+"F82.wireOp",EDGE,"E345");var subQ4=makeQuery(id+"F82.imprint","INTERSECT",VERTEX,{"derivedFrom":[subQ3,sQuery(id+"F82.wireOp",EDGE,"E347.right")]});Q1=makeQuery(id+"F84.opChamfer","BLEND_EDGE",EDGE,{"blendedFrom":[makeQuery(id+"F83.boolean.opBoolean","TWEAK_EDGE",EDGE,{"derivedFrom":[makeQuery(id+"F83.opExtrude","CAP_EDGE",EDGE,{"disambiguationData":[OSD([subQ3]),TDD([makeQuery(id+"F82.imprint","IMPRINT",EDGE,{"disambiguationData":[TD([[subQ4,1.0]])],"derivedFrom":subQ3})])],"isStart":true}),makeQuery(id+"F83.opExtrude","CAP_EDGE",EDGE,{"disambiguationData":[OSD([subQ3]),TDD([makeQuery(id+"F82.imprint","IMPRINT",EDGE,{"disambiguationData":[TD([[subQ4,-1.0]])],"derivedFrom":subQ3})])],"isStart":true})]}),makeQuery(id+"F81.boolean.opBoolean","MERGE",FACE,{"derivedFrom":[makeQuery(id+"F76.opExtrude","CAP_FACE",FACE,{"disambiguationData":[OSD([subQ2,sQuery(id+"F75.wireOp",EDGE,"E285"),sQuery(id+"F75.wireOp",EDGE,"E286"),sQuery(id+"F75.wireOp",EDGE,"E287"),sQuery(id+"F75.wireOp",EDGE,"E288"),sQuery(id+"F75.wireOp",EDGE,"E289"),subQ1,sQuery(id+"F75.wireOp",EDGE,"E291"),sQuery(id+"F75.wireOp",EDGE,"E292"),subQ0,sQuery(id+"F75.wireOp",EDGE,"E297.MirrorCS"),sQuery(id+"F75.wireOp",EDGE,"E298.MirrorCS"),sQuery(id+"F75.wireOp",EDGE,"E299.MirrorCS"),sQuery(id+"F75.wireOp",EDGE,"E300.MirrorCS"),sQuery(id+"F75.wireOp",EDGE,"E301.MirrorCS"),sQuery(id+"F75.wireOp",EDGE,"E302.MirrorCS"),sQuery(id+"F75.wireOp",EDGE,"E303.MirrorCS"),sQuery(id+"F75.wireOp",EDGE,"E304.MirrorCS"),sQuery(id+"F75.wireOp",EDGE,"E307.0"),sQuery(id+"F75.wireOp",EDGE,"E307.1"),sQuery(id+"F75.wireOp",EDGE,"E308.MirrorC"),sQuery(id+"F75.wireOp",EDGE,"E309.MirrorC")])],"isStart":false}),makeQuery(id+"F81.opExtrude","CAP_FACE",FACE,{"disambiguationData":[OSD([sQuery(id+"F80.wireOp",EDGE,"E335.0"),sQuery(id+"F80.wireOp",EDGE,"E335.1"),sQuery(id+"F80.wireOp",EDGE,"E335.2"),sQuery(id+"F80.wireOp",EDGE,"E336")])],"isStart":false}),makeQuery(id+"F81.opExtrude","CAP_FACE",FACE,{"disambiguationData":[OSD([sQuery(id+"F80.wireOp",EDGE,"E340.MirrorCS"),sQuery(id+"F80.wireOp",EDGE,"E341.MirrorCS"),sQuery(id+"F80.wireOp",EDGE,"E342.MirrorCS"),sQuery(id+"F80.wireOp",EDGE,"E343.MirrorCS")])],"isStart":false})]})],"blendedInto":[makeQuery(id+"F81.boolean.opBoolean","MERGE",FACE,{"derivedFrom":[makeQuery(id+"F76.opExtrude","CAP_FACE",FACE,{"disambiguationData":[OSD([subQ2,sQuery(id+"F75.wireOp",EDGE,"E285"),sQuery(id+"F75.wireOp",EDGE,"E286"),sQuery(id+"F75.wireOp",EDGE,"E287"),sQuery(id+"F75.wireOp",EDGE,"E288"),sQuery(id+"F75.wireOp",EDGE,"E289"),subQ1,sQuery(id+"F75.wireOp",EDGE,"E291"),sQuery(id+"F75.wireOp",EDGE,"E292"),subQ0,sQuery(id+"F75.wireOp",EDGE,"E297.MirrorCS"),sQuery(id+"F75.wireOp",EDGE,"E298.MirrorCS"),sQuery(id+"F75.wireOp",EDGE,"E299.MirrorCS"),sQuery(id+"F75.wireOp",EDGE,"E300.MirrorCS"),sQuery(id+"F75.wireOp",EDGE,"E301.MirrorCS"),sQuery(id+"F75.wireOp",EDGE,"E302.MirrorCS"),sQuery(id+"F75.wireOp",EDGE,"E303.MirrorCS"),sQuery(id+"F75.wireOp",EDGE,"E304.MirrorCS"),sQuery(id+"F75.wireOp",EDGE,"E307.0"),sQuery(id+"F75.wireOp",EDGE,"E307.1"),sQuery(id+"F75.wireOp",EDGE,"E308.MirrorC"),sQuery(id+"F75.wireOp",EDGE,"E309.MirrorC")])],"isStart":false}),makeQuery(id+"F81.opExtrude","CAP_FACE",FACE,{"disambiguationData":[OSD([sQuery(id+"F80.wireOp",EDGE,"E335.0"),sQuery(id+"F80.wireOp",EDGE,"E335.1"),sQuery(id+"F80.wireOp",EDGE,"E335.2"),sQuery(id+"F80.wireOp",EDGE,"E336")])],"isStart":false}),makeQuery(id+"F81.opExtrude","CAP_FACE",FACE,{"disambiguationData":[OSD([sQuery(id+"F80.wireOp",EDGE,"E340.MirrorCS"),sQuery(id+"F80.wireOp",EDGE,"E341.MirrorCS"),sQuery(id+"F80.wireOp",EDGE,"E342.MirrorCS"),sQuery(id+"F80.wireOp",EDGE,"E343.MirrorCS")])],"isStart":false})]})]});}
            var Q2;
            {var subQ0=sQuery(id+"F75.wireOp",EDGE,"E290");Q2=makeQuery(id+"F84.opChamfer","BLEND_EDGE",EDGE,{"blendedFrom":[makeQuery(id+"F76.opExtrude","CAP_EDGE",EDGE,{"disambiguationData":[OSD([subQ0])],"isStart":false}),makeQuery(id+"F81.boolean.opBoolean","MERGE",FACE,{"derivedFrom":[makeQuery(id+"F76.opExtrude","CAP_FACE",FACE,{"disambiguationData":[OSD([sQuery(id+"F75.wireOp",EDGE,"E284"),sQuery(id+"F75.wireOp",EDGE,"E285"),sQuery(id+"F75.wireOp",EDGE,"E286"),sQuery(id+"F75.wireOp",EDGE,"E287"),sQuery(id+"F75.wireOp",EDGE,"E288"),sQuery(id+"F75.wireOp",EDGE,"E289"),subQ0,sQuery(id+"F75.wireOp",EDGE,"E291"),sQuery(id+"F75.wireOp",EDGE,"E292"),sQuery(id+"F75.wireOp",EDGE,"E296.MirrorCS"),sQuery(id+"F75.wireOp",EDGE,"E297.MirrorCS"),sQuery(id+"F75.wireOp",EDGE,"E298.MirrorCS"),sQuery(id+"F75.wireOp",EDGE,"E299.MirrorCS"),sQuery(id+"F75.wireOp",EDGE,"E300.MirrorCS"),sQuery(id+"F75.wireOp",EDGE,"E301.MirrorCS"),sQuery(id+"F75.wireOp",EDGE,"E302.MirrorCS"),sQuery(id+"F75.wireOp",EDGE,"E303.MirrorCS"),sQuery(id+"F75.wireOp",EDGE,"E304.MirrorCS"),sQuery(id+"F75.wireOp",EDGE,"E307.0"),sQuery(id+"F75.wireOp",EDGE,"E307.1"),sQuery(id+"F75.wireOp",EDGE,"E308.MirrorC"),sQuery(id+"F75.wireOp",EDGE,"E309.MirrorC")])],"isStart":false}),makeQuery(id+"F81.opExtrude","CAP_FACE",FACE,{"disambiguationData":[OSD([sQuery(id+"F80.wireOp",EDGE,"E335.0"),sQuery(id+"F80.wireOp",EDGE,"E335.1"),sQuery(id+"F80.wireOp",EDGE,"E335.2"),sQuery(id+"F80.wireOp",EDGE,"E336")])],"isStart":false}),makeQuery(id+"F81.opExtrude","CAP_FACE",FACE,{"disambiguationData":[OSD([sQuery(id+"F80.wireOp",EDGE,"E340.MirrorCS"),sQuery(id+"F80.wireOp",EDGE,"E341.MirrorCS"),sQuery(id+"F80.wireOp",EDGE,"E342.MirrorCS"),sQuery(id+"F80.wireOp",EDGE,"E343.MirrorCS")])],"isStart":false})]})],"blendedInto":[makeQuery(id+"F81.boolean.opBoolean","MERGE",FACE,{"derivedFrom":[makeQuery(id+"F76.opExtrude","CAP_FACE",FACE,{"disambiguationData":[OSD([sQuery(id+"F75.wireOp",EDGE,"E284"),sQuery(id+"F75.wireOp",EDGE,"E285"),sQuery(id+"F75.wireOp",EDGE,"E286"),sQuery(id+"F75.wireOp",EDGE,"E287"),sQuery(id+"F75.wireOp",EDGE,"E288"),sQuery(id+"F75.wireOp",EDGE,"E289"),subQ0,sQuery(id+"F75.wireOp",EDGE,"E291"),sQuery(id+"F75.wireOp",EDGE,"E292"),sQuery(id+"F75.wireOp",EDGE,"E296.MirrorCS"),sQuery(id+"F75.wireOp",EDGE,"E297.MirrorCS"),sQuery(id+"F75.wireOp",EDGE,"E298.MirrorCS"),sQuery(id+"F75.wireOp",EDGE,"E299.MirrorCS"),sQuery(id+"F75.wireOp",EDGE,"E300.MirrorCS"),sQuery(id+"F75.wireOp",EDGE,"E301.MirrorCS"),sQuery(id+"F75.wireOp",EDGE,"E302.MirrorCS"),sQuery(id+"F75.wireOp",EDGE,"E303.MirrorCS"),sQuery(id+"F75.wireOp",EDGE,"E304.MirrorCS"),sQuery(id+"F75.wireOp",EDGE,"E307.0"),sQuery(id+"F75.wireOp",EDGE,"E307.1"),sQuery(id+"F75.wireOp",EDGE,"E308.MirrorC"),sQuery(id+"F75.wireOp",EDGE,"E309.MirrorC")])],"isStart":false}),makeQuery(id+"F81.opExtrude","CAP_FACE",FACE,{"disambiguationData":[OSD([sQuery(id+"F80.wireOp",EDGE,"E335.0"),sQuery(id+"F80.wireOp",EDGE,"E335.1"),sQuery(id+"F80.wireOp",EDGE,"E335.2"),sQuery(id+"F80.wireOp",EDGE,"E336")])],"isStart":false}),makeQuery(id+"F81.opExtrude","CAP_FACE",FACE,{"disambiguationData":[OSD([sQuery(id+"F80.wireOp",EDGE,"E340.MirrorCS"),sQuery(id+"F80.wireOp",EDGE,"E341.MirrorCS"),sQuery(id+"F80.wireOp",EDGE,"E342.MirrorCS"),sQuery(id+"F80.wireOp",EDGE,"E343.MirrorCS")])],"isStart":false})]})]});}
            var Q3;
            {var subQ0=sQuery(id+"F75.wireOp",EDGE,"E291");Q3=makeQuery(id+"F84.opChamfer","BLEND_EDGE",EDGE,{"blendedFrom":[makeQuery(id+"F76.opExtrude","CAP_EDGE",EDGE,{"disambiguationData":[OSD([subQ0])],"isStart":false}),makeQuery(id+"F81.boolean.opBoolean","MERGE",FACE,{"derivedFrom":[makeQuery(id+"F76.opExtrude","CAP_FACE",FACE,{"disambiguationData":[OSD([sQuery(id+"F75.wireOp",EDGE,"E284"),sQuery(id+"F75.wireOp",EDGE,"E285"),sQuery(id+"F75.wireOp",EDGE,"E286"),sQuery(id+"F75.wireOp",EDGE,"E287"),sQuery(id+"F75.wireOp",EDGE,"E288"),sQuery(id+"F75.wireOp",EDGE,"E289"),sQuery(id+"F75.wireOp",EDGE,"E290"),subQ0,sQuery(id+"F75.wireOp",EDGE,"E292"),sQuery(id+"F75.wireOp",EDGE,"E296.MirrorCS"),sQuery(id+"F75.wireOp",EDGE,"E297.MirrorCS"),sQuery(id+"F75.wireOp",EDGE,"E298.MirrorCS"),sQuery(id+"F75.wireOp",EDGE,"E299.MirrorCS"),sQuery(id+"F75.wireOp",EDGE,"E300.MirrorCS"),sQuery(id+"F75.wireOp",EDGE,"E301.MirrorCS"),sQuery(id+"F75.wireOp",EDGE,"E302.MirrorCS"),sQuery(id+"F75.wireOp",EDGE,"E303.MirrorCS"),sQuery(id+"F75.wireOp",EDGE,"E304.MirrorCS"),sQuery(id+"F75.wireOp",EDGE,"E307.0"),sQuery(id+"F75.wireOp",EDGE,"E307.1"),sQuery(id+"F75.wireOp",EDGE,"E308.MirrorC"),sQuery(id+"F75.wireOp",EDGE,"E309.MirrorC")])],"isStart":false}),makeQuery(id+"F81.opExtrude","CAP_FACE",FACE,{"disambiguationData":[OSD([sQuery(id+"F80.wireOp",EDGE,"E335.0"),sQuery(id+"F80.wireOp",EDGE,"E335.1"),sQuery(id+"F80.wireOp",EDGE,"E335.2"),sQuery(id+"F80.wireOp",EDGE,"E336")])],"isStart":false}),makeQuery(id+"F81.opExtrude","CAP_FACE",FACE,{"disambiguationData":[OSD([sQuery(id+"F80.wireOp",EDGE,"E340.MirrorCS"),sQuery(id+"F80.wireOp",EDGE,"E341.MirrorCS"),sQuery(id+"F80.wireOp",EDGE,"E342.MirrorCS"),sQuery(id+"F80.wireOp",EDGE,"E343.MirrorCS")])],"isStart":false})]})],"blendedInto":[makeQuery(id+"F81.boolean.opBoolean","MERGE",FACE,{"derivedFrom":[makeQuery(id+"F76.opExtrude","CAP_FACE",FACE,{"disambiguationData":[OSD([sQuery(id+"F75.wireOp",EDGE,"E284"),sQuery(id+"F75.wireOp",EDGE,"E285"),sQuery(id+"F75.wireOp",EDGE,"E286"),sQuery(id+"F75.wireOp",EDGE,"E287"),sQuery(id+"F75.wireOp",EDGE,"E288"),sQuery(id+"F75.wireOp",EDGE,"E289"),sQuery(id+"F75.wireOp",EDGE,"E290"),subQ0,sQuery(id+"F75.wireOp",EDGE,"E292"),sQuery(id+"F75.wireOp",EDGE,"E296.MirrorCS"),sQuery(id+"F75.wireOp",EDGE,"E297.MirrorCS"),sQuery(id+"F75.wireOp",EDGE,"E298.MirrorCS"),sQuery(id+"F75.wireOp",EDGE,"E299.MirrorCS"),sQuery(id+"F75.wireOp",EDGE,"E300.MirrorCS"),sQuery(id+"F75.wireOp",EDGE,"E301.MirrorCS"),sQuery(id+"F75.wireOp",EDGE,"E302.MirrorCS"),sQuery(id+"F75.wireOp",EDGE,"E303.MirrorCS"),sQuery(id+"F75.wireOp",EDGE,"E304.MirrorCS"),sQuery(id+"F75.wireOp",EDGE,"E307.0"),sQuery(id+"F75.wireOp",EDGE,"E307.1"),sQuery(id+"F75.wireOp",EDGE,"E308.MirrorC"),sQuery(id+"F75.wireOp",EDGE,"E309.MirrorC")])],"isStart":false}),makeQuery(id+"F81.opExtrude","CAP_FACE",FACE,{"disambiguationData":[OSD([sQuery(id+"F80.wireOp",EDGE,"E335.0"),sQuery(id+"F80.wireOp",EDGE,"E335.1"),sQuery(id+"F80.wireOp",EDGE,"E335.2"),sQuery(id+"F80.wireOp",EDGE,"E336")])],"isStart":false}),makeQuery(id+"F81.opExtrude","CAP_FACE",FACE,{"disambiguationData":[OSD([sQuery(id+"F80.wireOp",EDGE,"E340.MirrorCS"),sQuery(id+"F80.wireOp",EDGE,"E341.MirrorCS"),sQuery(id+"F80.wireOp",EDGE,"E342.MirrorCS"),sQuery(id+"F80.wireOp",EDGE,"E343.MirrorCS")])],"isStart":false})]})]});}
            var Q4;
            {var subQ0=sQuery(id+"F75.wireOp",EDGE,"E304.MirrorCS");var subQ1=sQuery(id+"F75.wireOp",EDGE,"E292");Q4=makeQuery(id+"F84.opChamfer","BLEND_EDGE",EDGE,{"blendedFrom":[makeQuery(id+"F76.opExtrude","CAP_EDGE",EDGE,{"disambiguationData":[OSD([subQ1,subQ0])],"isStart":false}),makeQuery(id+"F81.boolean.opBoolean","MERGE",FACE,{"derivedFrom":[makeQuery(id+"F76.opExtrude","CAP_FACE",FACE,{"disambiguationData":[OSD([sQuery(id+"F75.wireOp",EDGE,"E284"),sQuery(id+"F75.wireOp",EDGE,"E285"),sQuery(id+"F75.wireOp",EDGE,"E286"),sQuery(id+"F75.wireOp",EDGE,"E287"),sQuery(id+"F75.wireOp",EDGE,"E288"),sQuery(id+"F75.wireOp",EDGE,"E289"),sQuery(id+"F75.wireOp",EDGE,"E290"),sQuery(id+"F75.wireOp",EDGE,"E291"),subQ1,sQuery(id+"F75.wireOp",EDGE,"E296.MirrorCS"),sQuery(id+"F75.wireOp",EDGE,"E297.MirrorCS"),sQuery(id+"F75.wireOp",EDGE,"E298.MirrorCS"),sQuery(id+"F75.wireOp",EDGE,"E299.MirrorCS"),sQuery(id+"F75.wireOp",EDGE,"E300.MirrorCS"),sQuery(id+"F75.wireOp",EDGE,"E301.MirrorCS"),sQuery(id+"F75.wireOp",EDGE,"E302.MirrorCS"),sQuery(id+"F75.wireOp",EDGE,"E303.MirrorCS"),subQ0,sQuery(id+"F75.wireOp",EDGE,"E307.0"),sQuery(id+"F75.wireOp",EDGE,"E307.1"),sQuery(id+"F75.wireOp",EDGE,"E308.MirrorC"),sQuery(id+"F75.wireOp",EDGE,"E309.MirrorC")])],"isStart":false}),makeQuery(id+"F81.opExtrude","CAP_FACE",FACE,{"disambiguationData":[OSD([sQuery(id+"F80.wireOp",EDGE,"E335.0"),sQuery(id+"F80.wireOp",EDGE,"E335.1"),sQuery(id+"F80.wireOp",EDGE,"E335.2"),sQuery(id+"F80.wireOp",EDGE,"E336")])],"isStart":false}),makeQuery(id+"F81.opExtrude","CAP_FACE",FACE,{"disambiguationData":[OSD([sQuery(id+"F80.wireOp",EDGE,"E340.MirrorCS"),sQuery(id+"F80.wireOp",EDGE,"E341.MirrorCS"),sQuery(id+"F80.wireOp",EDGE,"E342.MirrorCS"),sQuery(id+"F80.wireOp",EDGE,"E343.MirrorCS")])],"isStart":false})]})],"blendedInto":[makeQuery(id+"F81.boolean.opBoolean","MERGE",FACE,{"derivedFrom":[makeQuery(id+"F76.opExtrude","CAP_FACE",FACE,{"disambiguationData":[OSD([sQuery(id+"F75.wireOp",EDGE,"E284"),sQuery(id+"F75.wireOp",EDGE,"E285"),sQuery(id+"F75.wireOp",EDGE,"E286"),sQuery(id+"F75.wireOp",EDGE,"E287"),sQuery(id+"F75.wireOp",EDGE,"E288"),sQuery(id+"F75.wireOp",EDGE,"E289"),sQuery(id+"F75.wireOp",EDGE,"E290"),sQuery(id+"F75.wireOp",EDGE,"E291"),subQ1,sQuery(id+"F75.wireOp",EDGE,"E296.MirrorCS"),sQuery(id+"F75.wireOp",EDGE,"E297.MirrorCS"),sQuery(id+"F75.wireOp",EDGE,"E298.MirrorCS"),sQuery(id+"F75.wireOp",EDGE,"E299.MirrorCS"),sQuery(id+"F75.wireOp",EDGE,"E300.MirrorCS"),sQuery(id+"F75.wireOp",EDGE,"E301.MirrorCS"),sQuery(id+"F75.wireOp",EDGE,"E302.MirrorCS"),sQuery(id+"F75.wireOp",EDGE,"E303.MirrorCS"),subQ0,sQuery(id+"F75.wireOp",EDGE,"E307.0"),sQuery(id+"F75.wireOp",EDGE,"E307.1"),sQuery(id+"F75.wireOp",EDGE,"E308.MirrorC"),sQuery(id+"F75.wireOp",EDGE,"E309.MirrorC")])],"isStart":false}),makeQuery(id+"F81.opExtrude","CAP_FACE",FACE,{"disambiguationData":[OSD([sQuery(id+"F80.wireOp",EDGE,"E335.0"),sQuery(id+"F80.wireOp",EDGE,"E335.1"),sQuery(id+"F80.wireOp",EDGE,"E335.2"),sQuery(id+"F80.wireOp",EDGE,"E336")])],"isStart":false}),makeQuery(id+"F81.opExtrude","CAP_FACE",FACE,{"disambiguationData":[OSD([sQuery(id+"F80.wireOp",EDGE,"E340.MirrorCS"),sQuery(id+"F80.wireOp",EDGE,"E341.MirrorCS"),sQuery(id+"F80.wireOp",EDGE,"E342.MirrorCS"),sQuery(id+"F80.wireOp",EDGE,"E343.MirrorCS")])],"isStart":false})]})]});}
            var Q5;
            {var subQ0=sQuery(id+"F75.wireOp",EDGE,"E303.MirrorCS");Q5=makeQuery(id+"F84.opChamfer","BLEND_EDGE",EDGE,{"blendedFrom":[makeQuery(id+"F76.opExtrude","CAP_EDGE",EDGE,{"disambiguationData":[OSD([subQ0])],"isStart":false}),makeQuery(id+"F81.boolean.opBoolean","MERGE",FACE,{"derivedFrom":[makeQuery(id+"F76.opExtrude","CAP_FACE",FACE,{"disambiguationData":[OSD([sQuery(id+"F75.wireOp",EDGE,"E284"),sQuery(id+"F75.wireOp",EDGE,"E285"),sQuery(id+"F75.wireOp",EDGE,"E286"),sQuery(id+"F75.wireOp",EDGE,"E287"),sQuery(id+"F75.wireOp",EDGE,"E288"),sQuery(id+"F75.wireOp",EDGE,"E289"),sQuery(id+"F75.wireOp",EDGE,"E290"),sQuery(id+"F75.wireOp",EDGE,"E291"),sQuery(id+"F75.wireOp",EDGE,"E292"),sQuery(id+"F75.wireOp",EDGE,"E296.MirrorCS"),sQuery(id+"F75.wireOp",EDGE,"E297.MirrorCS"),sQuery(id+"F75.wireOp",EDGE,"E298.MirrorCS"),sQuery(id+"F75.wireOp",EDGE,"E299.MirrorCS"),sQuery(id+"F75.wireOp",EDGE,"E300.MirrorCS"),sQuery(id+"F75.wireOp",EDGE,"E301.MirrorCS"),sQuery(id+"F75.wireOp",EDGE,"E302.MirrorCS"),subQ0,sQuery(id+"F75.wireOp",EDGE,"E304.MirrorCS"),sQuery(id+"F75.wireOp",EDGE,"E307.0"),sQuery(id+"F75.wireOp",EDGE,"E307.1"),sQuery(id+"F75.wireOp",EDGE,"E308.MirrorC"),sQuery(id+"F75.wireOp",EDGE,"E309.MirrorC")])],"isStart":false}),makeQuery(id+"F81.opExtrude","CAP_FACE",FACE,{"disambiguationData":[OSD([sQuery(id+"F80.wireOp",EDGE,"E335.0"),sQuery(id+"F80.wireOp",EDGE,"E335.1"),sQuery(id+"F80.wireOp",EDGE,"E335.2"),sQuery(id+"F80.wireOp",EDGE,"E336")])],"isStart":false}),makeQuery(id+"F81.opExtrude","CAP_FACE",FACE,{"disambiguationData":[OSD([sQuery(id+"F80.wireOp",EDGE,"E340.MirrorCS"),sQuery(id+"F80.wireOp",EDGE,"E341.MirrorCS"),sQuery(id+"F80.wireOp",EDGE,"E342.MirrorCS"),sQuery(id+"F80.wireOp",EDGE,"E343.MirrorCS")])],"isStart":false})]})],"blendedInto":[makeQuery(id+"F81.boolean.opBoolean","MERGE",FACE,{"derivedFrom":[makeQuery(id+"F76.opExtrude","CAP_FACE",FACE,{"disambiguationData":[OSD([sQuery(id+"F75.wireOp",EDGE,"E284"),sQuery(id+"F75.wireOp",EDGE,"E285"),sQuery(id+"F75.wireOp",EDGE,"E286"),sQuery(id+"F75.wireOp",EDGE,"E287"),sQuery(id+"F75.wireOp",EDGE,"E288"),sQuery(id+"F75.wireOp",EDGE,"E289"),sQuery(id+"F75.wireOp",EDGE,"E290"),sQuery(id+"F75.wireOp",EDGE,"E291"),sQuery(id+"F75.wireOp",EDGE,"E292"),sQuery(id+"F75.wireOp",EDGE,"E296.MirrorCS"),sQuery(id+"F75.wireOp",EDGE,"E297.MirrorCS"),sQuery(id+"F75.wireOp",EDGE,"E298.MirrorCS"),sQuery(id+"F75.wireOp",EDGE,"E299.MirrorCS"),sQuery(id+"F75.wireOp",EDGE,"E300.MirrorCS"),sQuery(id+"F75.wireOp",EDGE,"E301.MirrorCS"),sQuery(id+"F75.wireOp",EDGE,"E302.MirrorCS"),subQ0,sQuery(id+"F75.wireOp",EDGE,"E304.MirrorCS"),sQuery(id+"F75.wireOp",EDGE,"E307.0"),sQuery(id+"F75.wireOp",EDGE,"E307.1"),sQuery(id+"F75.wireOp",EDGE,"E308.MirrorC"),sQuery(id+"F75.wireOp",EDGE,"E309.MirrorC")])],"isStart":false}),makeQuery(id+"F81.opExtrude","CAP_FACE",FACE,{"disambiguationData":[OSD([sQuery(id+"F80.wireOp",EDGE,"E335.0"),sQuery(id+"F80.wireOp",EDGE,"E335.1"),sQuery(id+"F80.wireOp",EDGE,"E335.2"),sQuery(id+"F80.wireOp",EDGE,"E336")])],"isStart":false}),makeQuery(id+"F81.opExtrude","CAP_FACE",FACE,{"disambiguationData":[OSD([sQuery(id+"F80.wireOp",EDGE,"E340.MirrorCS"),sQuery(id+"F80.wireOp",EDGE,"E341.MirrorCS"),sQuery(id+"F80.wireOp",EDGE,"E342.MirrorCS"),sQuery(id+"F80.wireOp",EDGE,"E343.MirrorCS")])],"isStart":false})]})]});}
            var Q6;
            {var subQ0=sQuery(id+"F75.wireOp",EDGE,"E302.MirrorCS");Q6=makeQuery(id+"F84.opChamfer","BLEND_EDGE",EDGE,{"blendedFrom":[makeQuery(id+"F76.opExtrude","CAP_EDGE",EDGE,{"disambiguationData":[OSD([subQ0])],"isStart":false}),makeQuery(id+"F81.boolean.opBoolean","MERGE",FACE,{"derivedFrom":[makeQuery(id+"F76.opExtrude","CAP_FACE",FACE,{"disambiguationData":[OSD([sQuery(id+"F75.wireOp",EDGE,"E284"),sQuery(id+"F75.wireOp",EDGE,"E285"),sQuery(id+"F75.wireOp",EDGE,"E286"),sQuery(id+"F75.wireOp",EDGE,"E287"),sQuery(id+"F75.wireOp",EDGE,"E288"),sQuery(id+"F75.wireOp",EDGE,"E289"),sQuery(id+"F75.wireOp",EDGE,"E290"),sQuery(id+"F75.wireOp",EDGE,"E291"),sQuery(id+"F75.wireOp",EDGE,"E292"),sQuery(id+"F75.wireOp",EDGE,"E296.MirrorCS"),sQuery(id+"F75.wireOp",EDGE,"E297.MirrorCS"),sQuery(id+"F75.wireOp",EDGE,"E298.MirrorCS"),sQuery(id+"F75.wireOp",EDGE,"E299.MirrorCS"),sQuery(id+"F75.wireOp",EDGE,"E300.MirrorCS"),sQuery(id+"F75.wireOp",EDGE,"E301.MirrorCS"),subQ0,sQuery(id+"F75.wireOp",EDGE,"E303.MirrorCS"),sQuery(id+"F75.wireOp",EDGE,"E304.MirrorCS"),sQuery(id+"F75.wireOp",EDGE,"E307.0"),sQuery(id+"F75.wireOp",EDGE,"E307.1"),sQuery(id+"F75.wireOp",EDGE,"E308.MirrorC"),sQuery(id+"F75.wireOp",EDGE,"E309.MirrorC")])],"isStart":false}),makeQuery(id+"F81.opExtrude","CAP_FACE",FACE,{"disambiguationData":[OSD([sQuery(id+"F80.wireOp",EDGE,"E335.0"),sQuery(id+"F80.wireOp",EDGE,"E335.1"),sQuery(id+"F80.wireOp",EDGE,"E335.2"),sQuery(id+"F80.wireOp",EDGE,"E336")])],"isStart":false}),makeQuery(id+"F81.opExtrude","CAP_FACE",FACE,{"disambiguationData":[OSD([sQuery(id+"F80.wireOp",EDGE,"E340.MirrorCS"),sQuery(id+"F80.wireOp",EDGE,"E341.MirrorCS"),sQuery(id+"F80.wireOp",EDGE,"E342.MirrorCS"),sQuery(id+"F80.wireOp",EDGE,"E343.MirrorCS")])],"isStart":false})]})],"blendedInto":[makeQuery(id+"F81.boolean.opBoolean","MERGE",FACE,{"derivedFrom":[makeQuery(id+"F76.opExtrude","CAP_FACE",FACE,{"disambiguationData":[OSD([sQuery(id+"F75.wireOp",EDGE,"E284"),sQuery(id+"F75.wireOp",EDGE,"E285"),sQuery(id+"F75.wireOp",EDGE,"E286"),sQuery(id+"F75.wireOp",EDGE,"E287"),sQuery(id+"F75.wireOp",EDGE,"E288"),sQuery(id+"F75.wireOp",EDGE,"E289"),sQuery(id+"F75.wireOp",EDGE,"E290"),sQuery(id+"F75.wireOp",EDGE,"E291"),sQuery(id+"F75.wireOp",EDGE,"E292"),sQuery(id+"F75.wireOp",EDGE,"E296.MirrorCS"),sQuery(id+"F75.wireOp",EDGE,"E297.MirrorCS"),sQuery(id+"F75.wireOp",EDGE,"E298.MirrorCS"),sQuery(id+"F75.wireOp",EDGE,"E299.MirrorCS"),sQuery(id+"F75.wireOp",EDGE,"E300.MirrorCS"),sQuery(id+"F75.wireOp",EDGE,"E301.MirrorCS"),subQ0,sQuery(id+"F75.wireOp",EDGE,"E303.MirrorCS"),sQuery(id+"F75.wireOp",EDGE,"E304.MirrorCS"),sQuery(id+"F75.wireOp",EDGE,"E307.0"),sQuery(id+"F75.wireOp",EDGE,"E307.1"),sQuery(id+"F75.wireOp",EDGE,"E308.MirrorC"),sQuery(id+"F75.wireOp",EDGE,"E309.MirrorC")])],"isStart":false}),makeQuery(id+"F81.opExtrude","CAP_FACE",FACE,{"disambiguationData":[OSD([sQuery(id+"F80.wireOp",EDGE,"E335.0"),sQuery(id+"F80.wireOp",EDGE,"E335.1"),sQuery(id+"F80.wireOp",EDGE,"E335.2"),sQuery(id+"F80.wireOp",EDGE,"E336")])],"isStart":false}),makeQuery(id+"F81.opExtrude","CAP_FACE",FACE,{"disambiguationData":[OSD([sQuery(id+"F80.wireOp",EDGE,"E340.MirrorCS"),sQuery(id+"F80.wireOp",EDGE,"E341.MirrorCS"),sQuery(id+"F80.wireOp",EDGE,"E342.MirrorCS"),sQuery(id+"F80.wireOp",EDGE,"E343.MirrorCS")])],"isStart":false})]})]});}
            var Q7;
            {var subQ0=sQuery(id+"F75.wireOp",EDGE,"E302.MirrorCS");var subQ1=sQuery(id+"F75.wireOp",EDGE,"E296.MirrorCS");var subQ2=sQuery(id+"F75.wireOp",EDGE,"E284");var subQ3=sQuery(id+"F82.wireOp",EDGE,"E345");var subQ4=makeQuery(id+"F82.imprint","INTERSECT",VERTEX,{"derivedFrom":[subQ3,sQuery(id+"F82.wireOp",EDGE,"E347.left")]});Q7=makeQuery(id+"F84.opChamfer","BLEND_EDGE",EDGE,{"blendedFrom":[makeQuery(id+"F83.boolean.opBoolean","TWEAK_EDGE",EDGE,{"derivedFrom":[makeQuery(id+"F83.opExtrude","CAP_EDGE",EDGE,{"disambiguationData":[OSD([subQ3]),TDD([makeQuery(id+"F82.imprint","IMPRINT",EDGE,{"disambiguationData":[TD([[subQ4,1.0]])],"derivedFrom":subQ3})])],"isStart":true}),makeQuery(id+"F83.opExtrude","CAP_EDGE",EDGE,{"disambiguationData":[OSD([subQ3]),TDD([makeQuery(id+"F82.imprint","IMPRINT",EDGE,{"disambiguationData":[TD([[subQ4,-1.0]])],"derivedFrom":subQ3})])],"isStart":true})]}),makeQuery(id+"F81.boolean.opBoolean","MERGE",FACE,{"derivedFrom":[makeQuery(id+"F76.opExtrude","CAP_FACE",FACE,{"disambiguationData":[OSD([subQ2,sQuery(id+"F75.wireOp",EDGE,"E285"),sQuery(id+"F75.wireOp",EDGE,"E286"),sQuery(id+"F75.wireOp",EDGE,"E287"),sQuery(id+"F75.wireOp",EDGE,"E288"),sQuery(id+"F75.wireOp",EDGE,"E289"),sQuery(id+"F75.wireOp",EDGE,"E290"),sQuery(id+"F75.wireOp",EDGE,"E291"),sQuery(id+"F75.wireOp",EDGE,"E292"),subQ1,sQuery(id+"F75.wireOp",EDGE,"E297.MirrorCS"),sQuery(id+"F75.wireOp",EDGE,"E298.MirrorCS"),sQuery(id+"F75.wireOp",EDGE,"E299.MirrorCS"),sQuery(id+"F75.wireOp",EDGE,"E300.MirrorCS"),sQuery(id+"F75.wireOp",EDGE,"E301.MirrorCS"),subQ0,sQuery(id+"F75.wireOp",EDGE,"E303.MirrorCS"),sQuery(id+"F75.wireOp",EDGE,"E304.MirrorCS"),sQuery(id+"F75.wireOp",EDGE,"E307.0"),sQuery(id+"F75.wireOp",EDGE,"E307.1"),sQuery(id+"F75.wireOp",EDGE,"E308.MirrorC"),sQuery(id+"F75.wireOp",EDGE,"E309.MirrorC")])],"isStart":false}),makeQuery(id+"F81.opExtrude","CAP_FACE",FACE,{"disambiguationData":[OSD([sQuery(id+"F80.wireOp",EDGE,"E335.0"),sQuery(id+"F80.wireOp",EDGE,"E335.1"),sQuery(id+"F80.wireOp",EDGE,"E335.2"),sQuery(id+"F80.wireOp",EDGE,"E336")])],"isStart":false}),makeQuery(id+"F81.opExtrude","CAP_FACE",FACE,{"disambiguationData":[OSD([sQuery(id+"F80.wireOp",EDGE,"E340.MirrorCS"),sQuery(id+"F80.wireOp",EDGE,"E341.MirrorCS"),sQuery(id+"F80.wireOp",EDGE,"E342.MirrorCS"),sQuery(id+"F80.wireOp",EDGE,"E343.MirrorCS")])],"isStart":false})]})],"blendedInto":[makeQuery(id+"F81.boolean.opBoolean","MERGE",FACE,{"derivedFrom":[makeQuery(id+"F76.opExtrude","CAP_FACE",FACE,{"disambiguationData":[OSD([subQ2,sQuery(id+"F75.wireOp",EDGE,"E285"),sQuery(id+"F75.wireOp",EDGE,"E286"),sQuery(id+"F75.wireOp",EDGE,"E287"),sQuery(id+"F75.wireOp",EDGE,"E288"),sQuery(id+"F75.wireOp",EDGE,"E289"),sQuery(id+"F75.wireOp",EDGE,"E290"),sQuery(id+"F75.wireOp",EDGE,"E291"),sQuery(id+"F75.wireOp",EDGE,"E292"),subQ1,sQuery(id+"F75.wireOp",EDGE,"E297.MirrorCS"),sQuery(id+"F75.wireOp",EDGE,"E298.MirrorCS"),sQuery(id+"F75.wireOp",EDGE,"E299.MirrorCS"),sQuery(id+"F75.wireOp",EDGE,"E300.MirrorCS"),sQuery(id+"F75.wireOp",EDGE,"E301.MirrorCS"),subQ0,sQuery(id+"F75.wireOp",EDGE,"E303.MirrorCS"),sQuery(id+"F75.wireOp",EDGE,"E304.MirrorCS"),sQuery(id+"F75.wireOp",EDGE,"E307.0"),sQuery(id+"F75.wireOp",EDGE,"E307.1"),sQuery(id+"F75.wireOp",EDGE,"E308.MirrorC"),sQuery(id+"F75.wireOp",EDGE,"E309.MirrorC")])],"isStart":false}),makeQuery(id+"F81.opExtrude","CAP_FACE",FACE,{"disambiguationData":[OSD([sQuery(id+"F80.wireOp",EDGE,"E335.0"),sQuery(id+"F80.wireOp",EDGE,"E335.1"),sQuery(id+"F80.wireOp",EDGE,"E335.2"),sQuery(id+"F80.wireOp",EDGE,"E336")])],"isStart":false}),makeQuery(id+"F81.opExtrude","CAP_FACE",FACE,{"disambiguationData":[OSD([sQuery(id+"F80.wireOp",EDGE,"E340.MirrorCS"),sQuery(id+"F80.wireOp",EDGE,"E341.MirrorCS"),sQuery(id+"F80.wireOp",EDGE,"E342.MirrorCS"),sQuery(id+"F80.wireOp",EDGE,"E343.MirrorCS")])],"isStart":false})]})]});}
            var Q8;
            {var subQ0=sQuery(id+"F75.wireOp",EDGE,"E296.MirrorCS");var subQ1=sQuery(id+"F75.wireOp",EDGE,"E284");Q8=makeQuery(id+"F84.opChamfer","BLEND_EDGE",EDGE,{"blendedFrom":[makeQuery(id+"F76.opExtrude","CAP_EDGE",EDGE,{"disambiguationData":[OSD([subQ1,subQ0])],"isStart":false}),makeQuery(id+"F76.opExtrude","SWEPT_FACE",FACE,{"disambiguationData":[OSD([subQ1,subQ0])]})],"blendedInto":[makeQuery(id+"F76.opExtrude","SWEPT_FACE",FACE,{"disambiguationData":[OSD([subQ1,subQ0])]})]});}
            var Q9;
            {var subQ0=sQuery(id+"F82.wireOp",EDGE,"E345");var subQ1=makeQuery(id+"F82.imprint","INTERSECT",VERTEX,{"derivedFrom":[subQ0,sQuery(id+"F82.wireOp",EDGE,"E347.right")]});var subQ2=makeQuery(id+"F82.imprint","IMPRINT",EDGE,{"disambiguationData":[TD([[subQ1,-1.0]])],"derivedFrom":subQ0});var subQ3=makeQuery(id+"F82.imprint","IMPRINT",EDGE,{"disambiguationData":[TD([[subQ1,1.0]])],"derivedFrom":subQ0});Q9=makeQuery(id+"F84.opChamfer","BLEND_EDGE",EDGE,{"blendedFrom":[makeQuery(id+"F83.boolean.opBoolean","TWEAK_EDGE",EDGE,{"derivedFrom":[makeQuery(id+"F83.opExtrude","CAP_EDGE",EDGE,{"disambiguationData":[OSD([subQ0]),TDD([subQ3])],"isStart":true}),makeQuery(id+"F83.opExtrude","CAP_EDGE",EDGE,{"disambiguationData":[OSD([subQ0]),TDD([subQ2])],"isStart":true})]}),makeQuery(id+"F83.boolean.opBoolean","TWEAK_FACE",FACE,{"derivedFrom":[makeQuery(id+"F83.opExtrude","SWEPT_FACE",FACE,{"disambiguationData":[OSD([subQ0]),TDD([subQ3])]}),makeQuery(id+"F83.opExtrude","SWEPT_FACE",FACE,{"disambiguationData":[OSD([subQ0]),TDD([subQ2])]})]})],"blendedInto":[makeQuery(id+"F83.boolean.opBoolean","TWEAK_FACE",FACE,{"derivedFrom":[makeQuery(id+"F83.opExtrude","SWEPT_FACE",FACE,{"disambiguationData":[OSD([subQ0]),TDD([subQ3])]}),makeQuery(id+"F83.opExtrude","SWEPT_FACE",FACE,{"disambiguationData":[OSD([subQ0]),TDD([subQ2])]})]})]});}
            var Q10;
            {var subQ0=sQuery(id+"F75.wireOp",EDGE,"E290");Q10=makeQuery(id+"F84.opChamfer","BLEND_EDGE",EDGE,{"blendedFrom":[makeQuery(id+"F76.opExtrude","CAP_EDGE",EDGE,{"disambiguationData":[OSD([subQ0])],"isStart":false}),makeQuery(id+"F78.boolean.opBoolean","MERGE",FACE,{"derivedFrom":[makeQuery(id+"F76.opExtrude","SWEPT_FACE",FACE,{"disambiguationData":[OSD([subQ0])]}),makeQuery(id+"F78.opExtrude","SWEPT_FACE",FACE,{"disambiguationData":[OSD([sQuery(id+"F77.wireOp",EDGE,"E327")])]})]})],"blendedInto":[makeQuery(id+"F78.boolean.opBoolean","MERGE",FACE,{"derivedFrom":[makeQuery(id+"F76.opExtrude","SWEPT_FACE",FACE,{"disambiguationData":[OSD([subQ0])]}),makeQuery(id+"F78.opExtrude","SWEPT_FACE",FACE,{"disambiguationData":[OSD([sQuery(id+"F77.wireOp",EDGE,"E327")])]})]})]});}
            var Q11;
            {var subQ0=sQuery(id+"F75.wireOp",EDGE,"E291");Q11=makeQuery(id+"F84.opChamfer","BLEND_EDGE",EDGE,{"blendedFrom":[makeQuery(id+"F76.opExtrude","CAP_EDGE",EDGE,{"disambiguationData":[OSD([subQ0])],"isStart":false}),makeQuery(id+"F76.opExtrude","SWEPT_FACE",FACE,{"disambiguationData":[OSD([subQ0])]})],"blendedInto":[makeQuery(id+"F76.opExtrude","SWEPT_FACE",FACE,{"disambiguationData":[OSD([subQ0])]})]});}
            var Q12;
            {var subQ0=sQuery(id+"F75.wireOp",EDGE,"E304.MirrorCS");var subQ1=sQuery(id+"F75.wireOp",EDGE,"E292");Q12=makeQuery(id+"F84.opChamfer","BLEND_EDGE",EDGE,{"blendedFrom":[makeQuery(id+"F76.opExtrude","CAP_EDGE",EDGE,{"disambiguationData":[OSD([subQ1,subQ0])],"isStart":false}),makeQuery(id+"F76.opExtrude","SWEPT_FACE",FACE,{"disambiguationData":[OSD([subQ1,subQ0])]})],"blendedInto":[makeQuery(id+"F76.opExtrude","SWEPT_FACE",FACE,{"disambiguationData":[OSD([subQ1,subQ0])]})]});}
            var Q13;
            {var subQ0=sQuery(id+"F75.wireOp",EDGE,"E303.MirrorCS");Q13=makeQuery(id+"F84.opChamfer","BLEND_EDGE",EDGE,{"blendedFrom":[makeQuery(id+"F76.opExtrude","CAP_EDGE",EDGE,{"disambiguationData":[OSD([subQ0])],"isStart":false}),makeQuery(id+"F76.opExtrude","SWEPT_FACE",FACE,{"disambiguationData":[OSD([subQ0])]})],"blendedInto":[makeQuery(id+"F76.opExtrude","SWEPT_FACE",FACE,{"disambiguationData":[OSD([subQ0])]})]});}
            var Q14;
            {var subQ0=sQuery(id+"F75.wireOp",EDGE,"E302.MirrorCS");Q14=makeQuery(id+"F84.opChamfer","BLEND_EDGE",EDGE,{"blendedFrom":[makeQuery(id+"F76.opExtrude","CAP_EDGE",EDGE,{"disambiguationData":[OSD([subQ0])],"isStart":false}),makeQuery(id+"F78.boolean.opBoolean","MERGE",FACE,{"derivedFrom":[makeQuery(id+"F76.opExtrude","SWEPT_FACE",FACE,{"disambiguationData":[OSD([subQ0])]}),makeQuery(id+"F78.opExtrude","SWEPT_FACE",FACE,{"disambiguationData":[OSD([sQuery(id+"F77.wireOp",EDGE,"E328.MirrorCS")])]})]})],"blendedInto":[makeQuery(id+"F78.boolean.opBoolean","MERGE",FACE,{"derivedFrom":[makeQuery(id+"F76.opExtrude","SWEPT_FACE",FACE,{"disambiguationData":[OSD([subQ0])]}),makeQuery(id+"F78.opExtrude","SWEPT_FACE",FACE,{"disambiguationData":[OSD([sQuery(id+"F77.wireOp",EDGE,"E328.MirrorCS")])]})]})]});}
            var Q15;
            {var subQ0=sQuery(id+"F82.wireOp",EDGE,"E345");var subQ1=makeQuery(id+"F82.imprint","INTERSECT",VERTEX,{"derivedFrom":[subQ0,sQuery(id+"F82.wireOp",EDGE,"E347.left")]});var subQ2=makeQuery(id+"F82.imprint","IMPRINT",EDGE,{"disambiguationData":[TD([[subQ1,-1.0]])],"derivedFrom":subQ0});var subQ3=makeQuery(id+"F82.imprint","IMPRINT",EDGE,{"disambiguationData":[TD([[subQ1,1.0]])],"derivedFrom":subQ0});Q15=makeQuery(id+"F84.opChamfer","BLEND_EDGE",EDGE,{"blendedFrom":[makeQuery(id+"F83.boolean.opBoolean","TWEAK_EDGE",EDGE,{"derivedFrom":[makeQuery(id+"F83.opExtrude","CAP_EDGE",EDGE,{"disambiguationData":[OSD([subQ0]),TDD([subQ3])],"isStart":true}),makeQuery(id+"F83.opExtrude","CAP_EDGE",EDGE,{"disambiguationData":[OSD([subQ0]),TDD([subQ2])],"isStart":true})]}),makeQuery(id+"F83.boolean.opBoolean","TWEAK_FACE",FACE,{"derivedFrom":[makeQuery(id+"F83.opExtrude","SWEPT_FACE",FACE,{"disambiguationData":[OSD([subQ0]),TDD([subQ3])]}),makeQuery(id+"F83.opExtrude","SWEPT_FACE",FACE,{"disambiguationData":[OSD([subQ0]),TDD([subQ2])]})]})],"blendedInto":[makeQuery(id+"F83.boolean.opBoolean","TWEAK_FACE",FACE,{"derivedFrom":[makeQuery(id+"F83.opExtrude","SWEPT_FACE",FACE,{"disambiguationData":[OSD([subQ0]),TDD([subQ3])]}),makeQuery(id+"F83.opExtrude","SWEPT_FACE",FACE,{"disambiguationData":[OSD([subQ0]),TDD([subQ2])]})]})]});}
            fillet(context, id + "F85", {"entities" : qUnion([Q0, Q1, Q2, Q3, Q4, Q5, Q6, Q7, Q8, Q9, Q10, Q11, Q12, Q13, Q14, Q15]), "radius" : 10 * mm, "tangentPropagation" : true, "allowEdgeOverflow" : false});
        }
        {
            var Q0;
            Q0=makeQuery(id+"F83.boolean.opBoolean","COPY",EDGE,{"derivedFrom":makeQuery(id+"F83.opExtrude","SWEPT_EDGE",EDGE,{"disambiguationData":[OSD([sQuery(id+"F75.wireOp",EDGE,"E290"),sQuery(id+"F82.wireOp",EDGE,"E345")])]})});
            var Q1;
            Q1=makeQuery(id+"F83.boolean.opBoolean","COPY",EDGE,{"derivedFrom":makeQuery(id+"F83.opExtrude","SWEPT_EDGE",EDGE,{"disambiguationData":[OSD([sQuery(id+"F75.wireOp",EDGE,"E302.MirrorCS"),sQuery(id+"F82.wireOp",EDGE,"E345")])]})});
            var Q2;
            {var subQ0=sQuery(id+"F82.wireOp",EDGE,"E345");var subQ1=sQuery(id+"F75.wireOp",EDGE,"E296.MirrorCS");var subQ2=sQuery(id+"F75.wireOp",EDGE,"E284");Q2=makeQuery(id+"F83.boolean.opBoolean","COPY",EDGE,{"derivedFrom":makeQuery(id+"F83.opExtrude","SWEPT_EDGE",EDGE,{"disambiguationData":[OSD([subQ2,subQ1,subQ0]),TDD([makeQuery(id+"F82.imprint","INTERSECT",VERTEX,{"disambiguationData":[OD(1.0)],"derivedFrom":[makeQuery(id+"F76.opExtrude","CAP_EDGE",EDGE,{"disambiguationData":[OSD([subQ2,subQ1])],"isStart":false}),subQ0]})])]})});}
            var Q3;
            {var subQ0=sQuery(id+"F82.wireOp",EDGE,"E345");var subQ1=sQuery(id+"F75.wireOp",EDGE,"E296.MirrorCS");var subQ2=sQuery(id+"F75.wireOp",EDGE,"E284");Q3=makeQuery(id+"F83.boolean.opBoolean","COPY",EDGE,{"derivedFrom":makeQuery(id+"F83.opExtrude","SWEPT_EDGE",EDGE,{"disambiguationData":[OSD([subQ2,subQ1,subQ0]),TDD([makeQuery(id+"F82.imprint","INTERSECT",VERTEX,{"disambiguationData":[OD(0.0)],"derivedFrom":[makeQuery(id+"F76.opExtrude","CAP_EDGE",EDGE,{"disambiguationData":[OSD([subQ2,subQ1])],"isStart":false}),subQ0]})])]})});}
            var Q4;
            {var subQ0=sQuery(id+"F82.wireOp",EDGE,"E345");var subQ1=makeQuery(id+"F82.imprint","INTERSECT",VERTEX,{"derivedFrom":[subQ0,sQuery(id+"F82.wireOp",EDGE,"E347.right")]});Q4=makeQuery(id+"F83.boolean.opBoolean","INTERSECT",EDGE,{"derivedFrom":[makeQuery(id+"F76.opExtrude","SWEPT_FACE",FACE,{"disambiguationData":[OSD([sQuery(id+"F75.wireOp",EDGE,"E286")])]}),makeQuery(id+"F83.opExtrude","SWEPT_FACE",FACE,{"disambiguationData":[OSD([subQ0]),TDD([makeQuery(id+"F82.imprint","IMPRINT",EDGE,{"disambiguationData":[TD([[subQ1,1.0]])],"derivedFrom":subQ0})])]}),makeQuery(id+"F83.opExtrude","SWEPT_FACE",FACE,{"disambiguationData":[OSD([subQ0]),TDD([makeQuery(id+"F82.imprint","IMPRINT",EDGE,{"disambiguationData":[TD([[subQ1,-1.0]])],"derivedFrom":subQ0})])]})]});}
            var Q5;
            {var subQ0=sQuery(id+"F82.wireOp",EDGE,"E345");var subQ1=makeQuery(id+"F82.imprint","INTERSECT",VERTEX,{"derivedFrom":[subQ0,sQuery(id+"F82.wireOp",EDGE,"E347.right")]});var subQ2=sQuery(id+"F75.wireOp",EDGE,"E288");Q5=makeQuery(id+"F83.boolean.opBoolean","INTERSECT",EDGE,{"derivedFrom":[makeQuery(id+"F78.boolean.opBoolean","MERGE",FACE,{"derivedFrom":[makeQuery(id+"F76.opExtrude","SWEPT_FACE",FACE,{"disambiguationData":[OSD([subQ2])]}),makeQuery(id+"F78.opExtrude","SWEPT_FACE",FACE,{"disambiguationData":[OSD([subQ2])]})]}),makeQuery(id+"F83.opExtrude","SWEPT_FACE",FACE,{"disambiguationData":[OSD([subQ0]),TDD([makeQuery(id+"F82.imprint","IMPRINT",EDGE,{"disambiguationData":[TD([[subQ1,1.0]])],"derivedFrom":subQ0})])]}),makeQuery(id+"F83.opExtrude","SWEPT_FACE",FACE,{"disambiguationData":[OSD([subQ0]),TDD([makeQuery(id+"F82.imprint","IMPRINT",EDGE,{"disambiguationData":[TD([[subQ1,-1.0]])],"derivedFrom":subQ0})])]})]});}
            var Q6;
            {var subQ0=sQuery(id+"F82.wireOp",EDGE,"E345");var subQ1=makeQuery(id+"F82.imprint","INTERSECT",VERTEX,{"derivedFrom":[subQ0,sQuery(id+"F82.wireOp",EDGE,"E347.left")]});Q6=makeQuery(id+"F83.boolean.opBoolean","INTERSECT",EDGE,{"derivedFrom":[makeQuery(id+"F76.opExtrude","SWEPT_FACE",FACE,{"disambiguationData":[OSD([sQuery(id+"F75.wireOp",EDGE,"E298.MirrorCS")])]}),makeQuery(id+"F83.opExtrude","SWEPT_FACE",FACE,{"disambiguationData":[OSD([subQ0]),TDD([makeQuery(id+"F82.imprint","IMPRINT",EDGE,{"disambiguationData":[TD([[subQ1,1.0]])],"derivedFrom":subQ0})])]}),makeQuery(id+"F83.opExtrude","SWEPT_FACE",FACE,{"disambiguationData":[OSD([subQ0]),TDD([makeQuery(id+"F82.imprint","IMPRINT",EDGE,{"disambiguationData":[TD([[subQ1,-1.0]])],"derivedFrom":subQ0})])]})]});}
            var Q7;
            {var subQ0=sQuery(id+"F82.wireOp",EDGE,"E345");var subQ1=makeQuery(id+"F82.imprint","INTERSECT",VERTEX,{"derivedFrom":[subQ0,sQuery(id+"F82.wireOp",EDGE,"E347.left")]});var subQ2=sQuery(id+"F75.wireOp",EDGE,"E300.MirrorCS");Q7=makeQuery(id+"F83.boolean.opBoolean","INTERSECT",EDGE,{"derivedFrom":[makeQuery(id+"F78.boolean.opBoolean","MERGE",FACE,{"derivedFrom":[makeQuery(id+"F76.opExtrude","SWEPT_FACE",FACE,{"disambiguationData":[OSD([subQ2])]}),makeQuery(id+"F78.opExtrude","SWEPT_FACE",FACE,{"disambiguationData":[OSD([subQ2])]})]}),makeQuery(id+"F83.opExtrude","SWEPT_FACE",FACE,{"disambiguationData":[OSD([subQ0]),TDD([makeQuery(id+"F82.imprint","IMPRINT",EDGE,{"disambiguationData":[TD([[subQ1,1.0]])],"derivedFrom":subQ0})])]}),makeQuery(id+"F83.opExtrude","SWEPT_FACE",FACE,{"disambiguationData":[OSD([subQ0]),TDD([makeQuery(id+"F82.imprint","IMPRINT",EDGE,{"disambiguationData":[TD([[subQ1,-1.0]])],"derivedFrom":subQ0})])]})]});}
            var Q8;
            Q8=makeQuery(id+"F76.opExtrude","SWEPT_EDGE",EDGE,{"disambiguationData":[OSD([sQuery(id+"F75.wireOp",EDGE,"E290"),sQuery(id+"F75.wireOp",EDGE,"E291")])]});
            var Q9;
            Q9=makeQuery(id+"F76.opExtrude","SWEPT_EDGE",EDGE,{"disambiguationData":[OSD([sQuery(id+"F75.wireOp",EDGE,"E291"),sQuery(id+"F75.wireOp",EDGE,"E292")])]});
            var Q10;
            Q10=makeQuery(id+"F76.opExtrude","SWEPT_EDGE",EDGE,{"disambiguationData":[OSD([sQuery(id+"F75.wireOp",EDGE,"E303.MirrorCS"),sQuery(id+"F75.wireOp",EDGE,"E304.MirrorCS")])]});
            var Q11;
            Q11=makeQuery(id+"F76.opExtrude","SWEPT_EDGE",EDGE,{"disambiguationData":[OSD([sQuery(id+"F75.wireOp",EDGE,"E302.MirrorCS"),sQuery(id+"F75.wireOp",EDGE,"E303.MirrorCS")])]});
            fillet(context, id + "F86", {"entities" : qUnion([Q0, Q1, Q2, Q3, Q4, Q5, Q6, Q7, Q8, Q9, Q10, Q11]), "radius" : 5 * mm, "tangentPropagation" : true, "allowEdgeOverflow" : false});
        }
        {
            var Q0;
            Q0=qCreatedBy(id+"F79.planeOp",FACE);
            var sketch = newSketch(context, id + "F87", { "sketchPlane" : qUnion([Q0])});
            skCircle(sketch, "E348.0", {"center": v(-35, 60.07) * mm, "radius": 3 * mm, "construction": true});
            skCircle(sketch, "E348.1", {"center": v(35, 60.07) * mm, "radius": 3 * mm, "construction": true});
            skCircle(sketch, "E348.2", {"center": v(35, 4.33) * mm, "radius": 3 * mm, "construction": true});
            skCircle(sketch, "E348.3", {"center": v(-35, 4.33) * mm, "radius": 3 * mm, "construction": true});
            skCircle(sketch, "E349", {"center": v(35, 60.07) * mm, "radius": 7 * mm});
            skCircle(sketch, "E350", {"center": v(-35, 60.07) * mm, "radius": 7 * mm});
            skCircle(sketch, "E351", {"center": v(-35, 4.33) * mm, "radius": 7 * mm});
            skCircle(sketch, "E352", {"center": v(35, 4.33) * mm, "radius": 7 * mm});
            skSolve(sketch);
        }
        {
            var Q0;
            Q0 = qSketchRegion(id + "F87", true);
            extrude(context, id + "F88", {"entities" : qUnion([Q0]), "operationType" : NewBodyOperationType.REMOVE, "endBound" : BoundingType.THROUGH_ALL, "oppositeDirection" : true, "depth" : 25 * mm});
        }
        {
            var Q0;
            Q0=makeQuery(id+"F76.opExtrude","SWEPT_BODY",BODY,{"disambiguationData":[OSD([sQuery(id+"F75.wireOp",EDGE,"E284"),sQuery(id+"F75.wireOp",EDGE,"E285"),sQuery(id+"F75.wireOp",EDGE,"E286"),sQuery(id+"F75.wireOp",EDGE,"E287"),sQuery(id+"F75.wireOp",EDGE,"E288"),sQuery(id+"F75.wireOp",EDGE,"E289"),sQuery(id+"F75.wireOp",EDGE,"E290"),sQuery(id+"F75.wireOp",EDGE,"E291"),sQuery(id+"F75.wireOp",EDGE,"E292"),sQuery(id+"F75.wireOp",EDGE,"E296.MirrorCS"),sQuery(id+"F75.wireOp",EDGE,"E297.MirrorCS"),sQuery(id+"F75.wireOp",EDGE,"E298.MirrorCS"),sQuery(id+"F75.wireOp",EDGE,"E299.MirrorCS"),sQuery(id+"F75.wireOp",EDGE,"E300.MirrorCS"),sQuery(id+"F75.wireOp",EDGE,"E301.MirrorCS"),sQuery(id+"F75.wireOp",EDGE,"E302.MirrorCS"),sQuery(id+"F75.wireOp",EDGE,"E303.MirrorCS"),sQuery(id+"F75.wireOp",EDGE,"E304.MirrorCS"),sQuery(id+"F75.wireOp",EDGE,"E307.0"),sQuery(id+"F75.wireOp",EDGE,"E307.1"),sQuery(id+"F75.wireOp",EDGE,"E308.MirrorC"),sQuery(id+"F75.wireOp",EDGE,"E309.MirrorC")])]});
            var Q1;
            Q1=qCreatedBy(makeId("Right.planeOp"),FACE);
            mirror(context, id + "F89", {"entities" : qUnion([Q0]), "mirrorPlane" : qUnion([Q1])});
        }
    });
